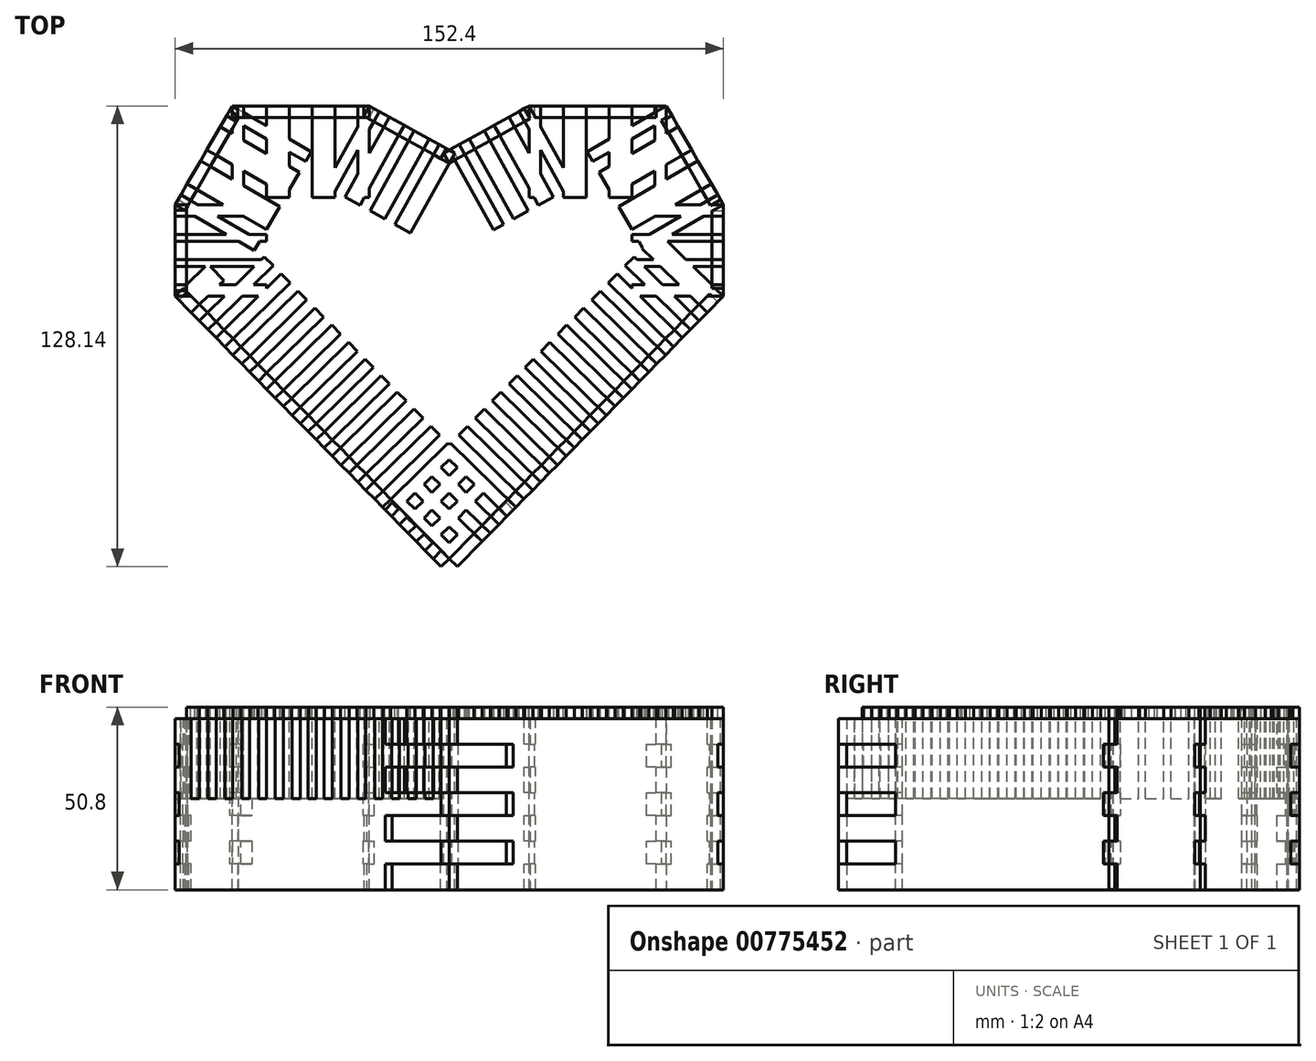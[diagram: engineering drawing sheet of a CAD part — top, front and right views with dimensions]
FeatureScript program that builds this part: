
annotation { "Feature Type Name" : "Feature", "Feature Type Description" : "" }
export const myFeature = defineFeature(function(context is Context, id is Id, definition is map)
    precondition{}
    {
        {
            var Q0;
            Q0=qCreatedBy(makeId("Top.planeOp"),FACE);
            var sketch = newSketch(context, id + "F0", { "sketchPlane" : qUnion([Q0])});
            skLineSegment(sketch, "E0", {"start": v(-76.2, 0) * mm, "end": v(0, -77.54) * mm});
            skLineSegment(sketch, "E1", {"start": v(0, -77.54) * mm, "end": v(76.2, 0) * mm});
            skLineSegment(sketch, "E2", {"start": v(76.2, 0) * mm, "end": v(76.2, 25.4) * mm});
            skLineSegment(sketch, "E3", {"start": v(76.2, 25.4) * mm, "end": v(60.32, 52.9) * mm});
            skLineSegment(sketch, "E4", {"start": v(60.32, 52.9) * mm, "end": v(22.23, 52.9) * mm});
            skLineSegment(sketch, "E5", {"start": v(22.23, 52.9) * mm, "end": v(0, 40.6) * mm});
            skLineSegment(sketch, "E6", {"start": v(0, 40.6) * mm, "end": v(-22.23, 52.9) * mm});
            skLineSegment(sketch, "E7", {"start": v(-22.23, 52.9) * mm, "end": v(-60.33, 52.9) * mm});
            skLineSegment(sketch, "E8", {"start": v(-60.32, 52.9) * mm, "end": v(-76.2, 25.4) * mm});
            skLineSegment(sketch, "E9", {"start": v(-76.2, 25.4) * mm, "end": v(-76.2, 0) * mm});
            skSolve(sketch);
        }
        {
            var Q0;
            Q0=makeQuery(id+"F0.imprint","IMPRINT",FACE,{"disambiguationData":[TD([[makeQuery(id+"F0.imprint","IMPRINT",EDGE,{"derivedFrom":sQuery(id+"F0.wireOp",EDGE,"E0")}),1.0]])]});
            extrude(context, id + "F1", {"entities" : qUnion([Q0]), "depth" : 3.17 * mm, "offsetDistance" : 25.4 * mm});
        }
        {
            var Q0;
            Q0=makeQuery(id+"F1.opExtrude","CAP_FACE",FACE,{"disambiguationData":[OSD([sQuery(id+"F0.wireOp",EDGE,"E0"),sQuery(id+"F0.wireOp",EDGE,"E1"),sQuery(id+"F0.wireOp",EDGE,"E2"),sQuery(id+"F0.wireOp",EDGE,"E3"),sQuery(id+"F0.wireOp",EDGE,"E4"),sQuery(id+"F0.wireOp",EDGE,"E5"),sQuery(id+"F0.wireOp",EDGE,"E6"),sQuery(id+"F0.wireOp",EDGE,"E7"),sQuery(id+"F0.wireOp",EDGE,"E8"),sQuery(id+"F0.wireOp",EDGE,"E9")])],"isStart":false});
            var sketch = newSketch(context, id + "F2", { "sketchPlane" : qUnion([Q0])});
            skLineSegment(sketch, "E10", {"start": v(-22.23, 52.9) * mm, "end": v(-23.76, 50.12) * mm});
            skLineSegment(sketch, "E11", {"start": v(-23.76, 50.12) * mm, "end": v(-1.54, 37.82) * mm});
            skLineSegment(sketch, "E12", {"start": v(-1.54, 37.82) * mm, "end": v(0, 40.6) * mm});
            skLineSegment(sketch, "E13", {"start": v(-76.2, 0) * mm, "end": v(-73.94, 2.23) * mm});
            skLineSegment(sketch, "E14", {"start": v(-73.94, 2.23) * mm, "end": v(2.26, -75.32) * mm});
            skLineSegment(sketch, "E15", {"start": v(2.26, -75.32) * mm, "end": v(0, -77.54) * mm});
            skLineSegment(sketch, "E16", {"start": v(76.2, 25.4) * mm, "end": v(73.03, 25.4) * mm});
            skLineSegment(sketch, "E17", {"start": v(73.03, 25.4) * mm, "end": v(73.03, 0) * mm});
            skLineSegment(sketch, "E18", {"start": v(73.03, 0) * mm, "end": v(76.2, 0) * mm});
            skLineSegment(sketch, "E19", {"start": v(-76.2, 25.4) * mm, "end": v(-73.03, 25.4) * mm});
            skLineSegment(sketch, "E20", {"start": v(-73.03, 25.4) * mm, "end": v(-73.03, 0) * mm});
            skLineSegment(sketch, "E21", {"start": v(-73.03, 0) * mm, "end": v(-76.2, 0) * mm});
            skLineSegment(sketch, "E22", {"start": v(-76.2, 25.4) * mm, "end": v(-73.45, 23.81) * mm});
            skPoint(sketch, "E22.endSnap0", {"position": v(-73.03, 12.7) * mm});
            skLineSegment(sketch, "E23", {"start": v(-73.45, 23.81) * mm, "end": v(-57.58, 51.3) * mm});
            skLineSegment(sketch, "E24", {"start": v(-57.58, 51.3) * mm, "end": v(-60.33, 52.9) * mm});
            skLineSegment(sketch, "E25", {"start": v(-60.33, 52.9) * mm, "end": v(-60.33, 49.72) * mm});
            skLineSegment(sketch, "E26", {"start": v(-60.33, 49.72) * mm, "end": v(-22.23, 49.72) * mm});
            skLineSegment(sketch, "E27", {"start": v(-22.23, 49.72) * mm, "end": v(-22.23, 52.9) * mm});
            skLineSegment(sketch, "E28", {"start": v(0, 40.6) * mm, "end": v(1.54, 37.82) * mm});
            skLineSegment(sketch, "E29", {"start": v(1.54, 37.82) * mm, "end": v(23.76, 50.12) * mm});
            skLineSegment(sketch, "E30", {"start": v(23.76, 50.12) * mm, "end": v(22.23, 52.9) * mm});
            skLineSegment(sketch, "E31", {"start": v(22.23, 52.9) * mm, "end": v(22.23, 49.72) * mm});
            skLineSegment(sketch, "E32", {"start": v(60.32, 49.72) * mm, "end": v(22.23, 49.72) * mm});
            skLineSegment(sketch, "E33", {"start": v(60.32, 49.72) * mm, "end": v(60.32, 52.9) * mm});
            skLineSegment(sketch, "E34", {"start": v(0, -77.54) * mm, "end": v(-2.26, -75.32) * mm});
            skLineSegment(sketch, "E35", {"start": v(-2.26, -75.32) * mm, "end": v(73.94, 2.23) * mm});
            skLineSegment(sketch, "E36", {"start": v(73.94, 2.23) * mm, "end": v(76.2, 0) * mm});
            skLineSegment(sketch, "E37", {"start": v(60.32, 52.9) * mm, "end": v(57.58, 51.3) * mm});
            skLineSegment(sketch, "E38", {"start": v(57.58, 51.3) * mm, "end": v(73.45, 23.81) * mm});
            skLineSegment(sketch, "E39", {"start": v(73.45, 23.81) * mm, "end": v(76.2, 25.4) * mm});
            skLineSegment(sketch, "E40", {"start": v(0, 40.6) * mm, "end": v(1.54, 39.75) * mm});
            skLineSegment(sketch, "E41", {"start": v(1.54, 39.75) * mm, "end": v(0, 36.97) * mm});
            skLineSegment(sketch, "E42", {"start": v(0, 36.97) * mm, "end": v(-1.54, 37.82) * mm});
            skLineSegment(sketch, "E43", {"start": v(1.54, 37.82) * mm, "end": v(0, 36.97) * mm});
            skLineSegment(sketch, "E44", {"start": v(0, 36.97) * mm, "end": v(-1.54, 39.75) * mm});
            skLineSegment(sketch, "E45", {"start": v(-1.54, 39.75) * mm, "end": v(0, 40.6) * mm});
            skSolve(sketch);
        }
        {
            var Q0;
            {var subQ0=sQuery(id+"F2.wireOp",EDGE,"E24");Q0=makeQuery(id+"F2.imprint","IMPRINT",FACE,{"disambiguationData":[TD([[makeQuery(id+"F2.imprint","IMPRINT",EDGE,{"derivedFrom":subQ0}),1.0]])]});}
            var Q1;
            {var subQ5=sQuery(id+"F2.wireOp",EDGE,"E10");Q1=makeQuery(id+"F2.imprint","IMPRINT",FACE,{"disambiguationData":[TD([[makeQuery(id+"F2.imprint","IMPRINT",EDGE,{"derivedFrom":subQ5}),-1.0]])]});}
            var Q2;
            {var subQ0=sQuery(id+"F2.wireOp",EDGE,"E10");Q2=makeQuery(id+"F2.imprint","IMPRINT",FACE,{"disambiguationData":[TD([[makeQuery(id+"F2.imprint","IMPRINT",EDGE,{"derivedFrom":subQ0}),1.0]])]});}
            extrude(context, id + "F3", {"entities" : qUnion([Q0, Q1, Q2]), "oppositeDirection" : true, "depth" : 50.8 * mm, "offsetDistance" : 25.4 * mm});
        }
        {
            var Q0;
            {var subQ5=sQuery(id+"F2.wireOp",EDGE,"E19");Q0=makeQuery(id+"F2.imprint","IMPRINT",FACE,{"disambiguationData":[TD([[makeQuery(id+"F2.imprint","IMPRINT",EDGE,{"derivedFrom":subQ5}),1.0]])]});}
            var Q1;
            {var subQ0=sQuery(id+"F2.wireOp",EDGE,"E19");Q1=makeQuery(id+"F2.imprint","IMPRINT",FACE,{"disambiguationData":[TD([[makeQuery(id+"F2.imprint","IMPRINT",EDGE,{"derivedFrom":subQ0}),-1.0]])]});}
            var Q2;
            Q2=makeQuery(id+"F3.opExtrude","CAP_VERTEX",VERTEX,{"disambiguationData":[OSD([sQuery(id+"F2.wireOp",EDGE,"E25"),sQuery(id+"F2.wireOp",EDGE,"E26")])],"isStart":false});
            extrude(context, id + "F4", {"entities" : qUnion([Q0, Q1]), "endBound" : BoundingType.UP_TO_VERTEX, "oppositeDirection" : true, "depth" : 25.4 * mm, "endBoundEntityVertex" : qUnion([Q2]), "offsetDistance" : 25.4 * mm});
        }
        {
            var Q0;
            {var subQ6=sQuery(id+"F2.wireOp",EDGE,"E13");Q0=makeQuery(id+"F2.imprint","IMPRINT",FACE,{"disambiguationData":[TD([[makeQuery(id+"F2.imprint","IMPRINT",EDGE,{"derivedFrom":subQ6}),1.0]])]});}
            var Q1;
            {var subQ0=sQuery(id+"F2.wireOp",EDGE,"E13");Q1=makeQuery(id+"F2.imprint","IMPRINT",FACE,{"disambiguationData":[TD([[makeQuery(id+"F2.imprint","IMPRINT",EDGE,{"derivedFrom":subQ0}),-1.0]])]});}
            var Q2;
            {var subQ0=sQuery(id+"F2.wireOp",EDGE,"E19");Q2=makeQuery(id+"F2.imprint","IMPRINT",FACE,{"disambiguationData":[TD([[makeQuery(id+"F2.imprint","IMPRINT",EDGE,{"derivedFrom":subQ0}),-1.0]])]});}
            var Q3;
            Q3=makeQuery(id+"F4.opExtrude","CAP_VERTEX",VERTEX,{"disambiguationData":[OSD([sQuery(id+"F0.wireOp",EDGE,"E8"),sQuery(id+"F2.wireOp",EDGE,"E22")])],"isStart":false});
            extrude(context, id + "F5", {"entities" : qUnion([Q0, Q1, Q2]), "endBound" : BoundingType.UP_TO_VERTEX, "oppositeDirection" : true, "depth" : 25.4 * mm, "endBoundEntityVertex" : qUnion([Q3]), "offsetDistance" : 25.4 * mm});
        }
        {
            var Q0;
            {var subQ0=sQuery(id+"F2.wireOp",EDGE,"E21");Q0=makeQuery(id+"F2.imprint","IMPRINT",FACE,{"disambiguationData":[TD([[makeQuery(id+"F2.imprint","IMPRINT",EDGE,{"derivedFrom":subQ0}),1.0]])]});}
            var Q1;
            {var subQ0=sQuery(id+"F2.wireOp",EDGE,"E13");Q1=makeQuery(id+"F2.imprint","IMPRINT",FACE,{"disambiguationData":[TD([[makeQuery(id+"F2.imprint","IMPRINT",EDGE,{"derivedFrom":subQ0}),-1.0]])]});}
            var Q2;
            {var subQ0=sQuery(id+"F2.wireOp",EDGE,"E35");var subQ1=sQuery(id+"F2.wireOp",EDGE,"E14");var subQ2=makeQuery(id+"F2.imprint","INTERSECT",VERTEX,{"derivedFrom":[subQ1,subQ0]});Q2=makeQuery(id+"F2.imprint","IMPRINT",FACE,{"disambiguationData":[TD([[makeQuery(id+"F2.imprint","IMPRINT",EDGE,{"disambiguationData":[TD([[subQ2,-1.0]])],"derivedFrom":subQ1}),-1.0]])]});}
            var Q3;
            Q3=makeQuery(id+"F5.opExtrude","CAP_VERTEX",VERTEX,{"disambiguationData":[OSD([sQuery(id+"F0.wireOp",EDGE,"E9"),sQuery(id+"F2.wireOp",EDGE,"E21")])],"isStart":false});
            extrude(context, id + "F6", {"entities" : qUnion([Q0, Q1, Q2]), "endBound" : BoundingType.UP_TO_VERTEX, "oppositeDirection" : true, "depth" : 25.4 * mm, "endBoundEntityVertex" : qUnion([Q3]), "offsetDistance" : 25.4 * mm});
        }
        {
            var Q0;
            {var subQ0=sQuery(id+"F2.wireOp",EDGE,"E18");Q0=makeQuery(id+"F2.imprint","IMPRINT",FACE,{"disambiguationData":[TD([[makeQuery(id+"F2.imprint","IMPRINT",EDGE,{"derivedFrom":subQ0}),-1.0]])]});}
            var Q1;
            {var subQ0=sQuery(id+"F2.wireOp",EDGE,"E35");var subQ1=sQuery(id+"F2.wireOp",EDGE,"E14");var subQ2=makeQuery(id+"F2.imprint","INTERSECT",VERTEX,{"derivedFrom":[subQ1,subQ0]});Q1=makeQuery(id+"F2.imprint","IMPRINT",FACE,{"disambiguationData":[TD([[makeQuery(id+"F2.imprint","IMPRINT",EDGE,{"disambiguationData":[TD([[subQ2,-1.0]])],"derivedFrom":subQ1}),-1.0]])]});}
            var Q2;
            {var subQ0=sQuery(id+"F2.wireOp",EDGE,"E18");Q2=makeQuery(id+"F2.imprint","IMPRINT",FACE,{"disambiguationData":[TD([[makeQuery(id+"F2.imprint","IMPRINT",EDGE,{"derivedFrom":subQ0}),1.0]])]});}
            var Q3;
            Q3=makeQuery(id+"F6.opExtrude","CAP_VERTEX",VERTEX,{"disambiguationData":[OSD([sQuery(id+"F0.wireOp",EDGE,"E0"),sQuery(id+"F0.wireOp",EDGE,"E1")])],"isStart":false});
            extrude(context, id + "F7", {"entities" : qUnion([Q0, Q1, Q2]), "endBound" : BoundingType.UP_TO_VERTEX, "oppositeDirection" : true, "depth" : 25.4 * mm, "endBoundEntityVertex" : qUnion([Q3]), "offsetDistance" : 25.4 * mm});
        }
        {
            var Q0;
            {var subQ0=sQuery(id+"F2.wireOp",EDGE,"E36");Q0=makeQuery(id+"F2.imprint","IMPRINT",FACE,{"disambiguationData":[TD([[makeQuery(id+"F2.imprint","IMPRINT",EDGE,{"derivedFrom":subQ0}),1.0]])]});}
            var Q1;
            {var subQ0=sQuery(id+"F2.wireOp",EDGE,"E16");Q1=makeQuery(id+"F2.imprint","IMPRINT",FACE,{"disambiguationData":[TD([[makeQuery(id+"F2.imprint","IMPRINT",EDGE,{"derivedFrom":subQ0}),1.0]])]});}
            var Q2;
            {var subQ0=sQuery(id+"F2.wireOp",EDGE,"E18");Q2=makeQuery(id+"F2.imprint","IMPRINT",FACE,{"disambiguationData":[TD([[makeQuery(id+"F2.imprint","IMPRINT",EDGE,{"derivedFrom":subQ0}),1.0]])]});}
            var Q3;
            Q3=makeQuery(id+"F7.opExtrude","CAP_VERTEX",VERTEX,{"disambiguationData":[OSD([sQuery(id+"F2.wireOp",EDGE,"E35"),sQuery(id+"F2.wireOp",EDGE,"E36")])],"isStart":false});
            extrude(context, id + "F8", {"entities" : qUnion([Q0, Q1, Q2]), "endBound" : BoundingType.UP_TO_VERTEX, "oppositeDirection" : true, "depth" : 25.4 * mm, "endBoundEntityVertex" : qUnion([Q3]), "offsetDistance" : 25.4 * mm});
        }
        {
            var Q0;
            {var subQ2=sQuery(id+"F2.wireOp",EDGE,"E16");Q0=makeQuery(id+"F2.imprint","IMPRINT",FACE,{"disambiguationData":[TD([[makeQuery(id+"F2.imprint","IMPRINT",EDGE,{"derivedFrom":subQ2}),-1.0]])]});}
            var Q1;
            {var subQ0=sQuery(id+"F2.wireOp",EDGE,"E16");Q1=makeQuery(id+"F2.imprint","IMPRINT",FACE,{"disambiguationData":[TD([[makeQuery(id+"F2.imprint","IMPRINT",EDGE,{"derivedFrom":subQ0}),1.0]])]});}
            var Q2;
            {var subQ0=sQuery(id+"F2.wireOp",EDGE,"E33");Q2=makeQuery(id+"F2.imprint","IMPRINT",FACE,{"disambiguationData":[TD([[makeQuery(id+"F2.imprint","IMPRINT",EDGE,{"derivedFrom":subQ0}),1.0]])]});}
            var Q3;
            Q3=makeQuery(id+"F8.opExtrude","CAP_VERTEX",VERTEX,{"disambiguationData":[OSD([sQuery(id+"F2.wireOp",EDGE,"E16"),sQuery(id+"F2.wireOp",EDGE,"E17")])],"isStart":false});
            extrude(context, id + "F9", {"entities" : qUnion([Q0, Q1, Q2]), "endBound" : BoundingType.UP_TO_VERTEX, "oppositeDirection" : true, "depth" : 25.4 * mm, "endBoundEntityVertex" : qUnion([Q3]), "offsetDistance" : 25.4 * mm});
        }
        {
            var Q0;
            {var subQ6=sQuery(id+"F2.wireOp",EDGE,"E30");Q0=makeQuery(id+"F2.imprint","IMPRINT",FACE,{"disambiguationData":[TD([[makeQuery(id+"F2.imprint","IMPRINT",EDGE,{"derivedFrom":subQ6}),-1.0]])]});}
            var Q1;
            {var subQ0=sQuery(id+"F2.wireOp",EDGE,"E30");Q1=makeQuery(id+"F2.imprint","IMPRINT",FACE,{"disambiguationData":[TD([[makeQuery(id+"F2.imprint","IMPRINT",EDGE,{"derivedFrom":subQ0}),1.0]])]});}
            var Q2;
            {var subQ0=sQuery(id+"F2.wireOp",EDGE,"E33");Q2=makeQuery(id+"F2.imprint","IMPRINT",FACE,{"disambiguationData":[TD([[makeQuery(id+"F2.imprint","IMPRINT",EDGE,{"derivedFrom":subQ0}),1.0]])]});}
            var Q3;
            Q3=makeQuery(id+"F9.opExtrude","CAP_VERTEX",VERTEX,{"disambiguationData":[OSD([sQuery(id+"F0.wireOp",EDGE,"E3"),sQuery(id+"F2.wireOp",EDGE,"E37")])],"isStart":false});
            extrude(context, id + "F10", {"entities" : qUnion([Q0, Q1, Q2]), "endBound" : BoundingType.UP_TO_VERTEX, "oppositeDirection" : true, "depth" : 25.4 * mm, "endBoundEntityVertex" : qUnion([Q3]), "offsetDistance" : 25.4 * mm});
        }
        {
            var Q0;
            {var subQ4=sQuery(id+"F2.wireOp",EDGE,"E28");Q0=makeQuery(id+"F2.imprint","IMPRINT",FACE,{"disambiguationData":[TD([[makeQuery(id+"F2.imprint","IMPRINT",EDGE,{"derivedFrom":subQ4}),1.0]])]});}
            var Q1;
            {var subQ0=sQuery(id+"F2.wireOp",EDGE,"E30");Q1=makeQuery(id+"F2.imprint","IMPRINT",FACE,{"disambiguationData":[TD([[makeQuery(id+"F2.imprint","IMPRINT",EDGE,{"derivedFrom":subQ0}),1.0]])]});}
            var Q2;
            {var subQ0=sQuery(id+"F2.wireOp",EDGE,"E28");var subQ5=sQuery(id+"F2.wireOp",EDGE,"E41");var subQ7=makeQuery(id+"F2.imprint","INTERSECT",VERTEX,{"derivedFrom":[subQ0,subQ5]});Q2=makeQuery(id+"F2.imprint","IMPRINT",FACE,{"disambiguationData":[TD([[makeQuery(id+"F2.imprint","IMPRINT",EDGE,{"disambiguationData":[TD([[subQ7,-1.0]])],"derivedFrom":subQ5}),-1.0]])]});}
            var Q3;
            {var subQ0=sQuery(id+"F2.wireOp",EDGE,"E45");Q3=makeQuery(id+"F2.imprint","IMPRINT",FACE,{"disambiguationData":[TD([[makeQuery(id+"F2.imprint","IMPRINT",EDGE,{"derivedFrom":subQ0}),-1.0]])]});}
            var Q4;
            {var subQ0=sQuery(id+"F2.wireOp",EDGE,"E43");Q4=makeQuery(id+"F2.imprint","IMPRINT",FACE,{"disambiguationData":[TD([[makeQuery(id+"F2.imprint","IMPRINT",EDGE,{"derivedFrom":subQ0}),-1.0]])]});}
            var Q5;
            {var subQ1=sQuery(id+"F2.wireOp",EDGE,"E31");Q5=makeQuery(id+"F2.imprint","IMPRINT",FACE,{"disambiguationData":[TD([[makeQuery(id+"F2.imprint","IMPRINT",EDGE,{"derivedFrom":subQ1}),-1.0]])]});}
            var Q6;
            Q6=makeQuery(id+"F10.opExtrude","CAP_VERTEX",VERTEX,{"disambiguationData":[OSD([sQuery(id+"F2.wireOp",EDGE,"E31"),sQuery(id+"F2.wireOp",EDGE,"E32")])],"isStart":false});
            extrude(context, id + "F11", {"entities" : qUnion([Q0, Q1, Q2, Q3, Q4, Q5]), "endBound" : BoundingType.UP_TO_VERTEX, "oppositeDirection" : true, "depth" : 25.4 * mm, "endBoundEntityVertex" : qUnion([Q6]), "offsetDistance" : 25.4 * mm});
        }
        {
            var Q0;
            {var subQ4=sQuery(id+"F2.wireOp",EDGE,"E12");Q0=makeQuery(id+"F2.imprint","IMPRINT",FACE,{"disambiguationData":[TD([[makeQuery(id+"F2.imprint","IMPRINT",EDGE,{"derivedFrom":subQ4}),1.0]])]});}
            var Q1;
            {var subQ0=sQuery(id+"F2.wireOp",EDGE,"E10");Q1=makeQuery(id+"F2.imprint","IMPRINT",FACE,{"disambiguationData":[TD([[makeQuery(id+"F2.imprint","IMPRINT",EDGE,{"derivedFrom":subQ0}),1.0]])]});}
            var Q2;
            {var subQ0=sQuery(id+"F2.wireOp",EDGE,"E27");Q2=makeQuery(id+"F2.imprint","IMPRINT",FACE,{"disambiguationData":[TD([[makeQuery(id+"F2.imprint","IMPRINT",EDGE,{"derivedFrom":subQ0}),-1.0]])]});}
            var Q3;
            {var subQ0=sQuery(id+"F2.wireOp",EDGE,"E28");var subQ5=sQuery(id+"F2.wireOp",EDGE,"E41");var subQ7=makeQuery(id+"F2.imprint","INTERSECT",VERTEX,{"derivedFrom":[subQ0,subQ5]});Q3=makeQuery(id+"F2.imprint","IMPRINT",FACE,{"disambiguationData":[TD([[makeQuery(id+"F2.imprint","IMPRINT",EDGE,{"disambiguationData":[TD([[subQ7,-1.0]])],"derivedFrom":subQ5}),-1.0]])]});}
            var Q4;
            {var subQ0=sQuery(id+"F2.wireOp",EDGE,"E42");Q4=makeQuery(id+"F2.imprint","IMPRINT",FACE,{"disambiguationData":[TD([[makeQuery(id+"F2.imprint","IMPRINT",EDGE,{"derivedFrom":subQ0}),-1.0]])]});}
            var Q5;
            {var subQ0=sQuery(id+"F2.wireOp",EDGE,"E40");Q5=makeQuery(id+"F2.imprint","IMPRINT",FACE,{"disambiguationData":[TD([[makeQuery(id+"F2.imprint","IMPRINT",EDGE,{"derivedFrom":subQ0}),-1.0]])]});}
            var Q6;
            Q6=makeQuery(id+"F11.opExtrude","CAP_VERTEX",VERTEX,{"disambiguationData":[OSD([sQuery(id+"F0.wireOp",EDGE,"E5"),sQuery(id+"F2.wireOp",EDGE,"E44"),sQuery(id+"F2.wireOp",EDGE,"E45")])],"isStart":false});
            extrude(context, id + "F12", {"entities" : qUnion([Q0, Q1, Q2, Q3, Q4, Q5]), "endBound" : BoundingType.UP_TO_VERTEX, "oppositeDirection" : true, "depth" : 25.4 * mm, "endBoundEntityVertex" : qUnion([Q6]), "offsetDistance" : 25.4 * mm});
        }
        {
            var Q0;
            Q0=makeQuery(id+"F1.opExtrude","CAP_FACE",FACE,{"disambiguationData":[OSD([sQuery(id+"F0.wireOp",EDGE,"E0"),sQuery(id+"F0.wireOp",EDGE,"E1"),sQuery(id+"F0.wireOp",EDGE,"E2"),sQuery(id+"F0.wireOp",EDGE,"E3"),sQuery(id+"F0.wireOp",EDGE,"E4"),sQuery(id+"F0.wireOp",EDGE,"E5"),sQuery(id+"F0.wireOp",EDGE,"E6"),sQuery(id+"F0.wireOp",EDGE,"E7"),sQuery(id+"F0.wireOp",EDGE,"E8"),sQuery(id+"F0.wireOp",EDGE,"E9")])],"isStart":false});
            var sketch = newSketch(context, id + "F13", { "sketchPlane" : qUnion([Q0])});
            skCircle(sketch, "E46", {"center": v(-22.23, 52.9) * mm, "radius": 3.18 * mm});
            skCircle(sketch, "E47", {"center": v(0, 40.6) * mm, "radius": 3.18 * mm});
            skLineSegment(sketch, "E48", {"start": v(-19.45, 51.36) * mm, "end": v(-20.98, 48.58) * mm});
            skLineSegment(sketch, "E49", {"start": v(-20.98, 48.58) * mm, "end": v(-18.2, 47.04) * mm});
            skLineSegment(sketch, "E50", {"start": v(-18.2, 47.04) * mm, "end": v(-16.67, 49.82) * mm});
            skLineSegment(sketch, "E51", {"start": v(-12.5, 47.52) * mm, "end": v(-14.04, 44.74) * mm});
            skLineSegment(sketch, "E52", {"start": v(-14.04, 44.74) * mm, "end": v(-11.26, 43.2) * mm});
            skLineSegment(sketch, "E53", {"start": v(-11.26, 43.2) * mm, "end": v(-9.72, 45.98) * mm});
            skLineSegment(sketch, "E54", {"start": v(-5.56, 43.67) * mm, "end": v(-7.1, 40.9) * mm});
            skLineSegment(sketch, "E55", {"start": v(-7.1, 40.9) * mm, "end": v(-4.32, 39.36) * mm});
            skLineSegment(sketch, "E56", {"start": v(-4.32, 39.36) * mm, "end": v(-2.78, 42.14) * mm});
            skLineSegment(sketch, "E57", {"start": v(-17.44, 48.43) * mm, "end": v(-13.27, 46.13) * mm, "construction": true});
            skLineSegment(sketch, "E58", {"start": v(-10.5, 44.6) * mm, "end": v(-6.32, 42.28) * mm, "construction": true});
            skSolve(sketch);
        }
        {
            var Q0;
            {var subQ0=sQuery(id+"F13.wireOp",EDGE,"E48");Q0=makeQuery(id+"F13.imprint","IMPRINT",FACE,{"disambiguationData":[TD([[makeQuery(id+"F13.imprint","IMPRINT",EDGE,{"derivedFrom":subQ0}),1.0]])]});}
            var Q1;
            {var subQ0=sQuery(id+"F13.wireOp",EDGE,"E51");Q1=makeQuery(id+"F13.imprint","IMPRINT",FACE,{"disambiguationData":[TD([[makeQuery(id+"F13.imprint","IMPRINT",EDGE,{"derivedFrom":subQ0}),1.0]])]});}
            var Q2;
            {var subQ0=sQuery(id+"F13.wireOp",EDGE,"E54");Q2=makeQuery(id+"F13.imprint","IMPRINT",FACE,{"disambiguationData":[TD([[makeQuery(id+"F13.imprint","IMPRINT",EDGE,{"derivedFrom":subQ0}),1.0]])]});}
            extrude(context, id + "F14", {"entities" : qUnion([Q0, Q1, Q2]), "operationType" : NewBodyOperationType.REMOVE, "oppositeDirection" : true, "depth" : 25.4 * mm, "offsetDistance" : 25.4 * mm});
        }
        {
            var Q0;
            Q0=makeQuery(id+"F1.opExtrude","CAP_FACE",FACE,{"disambiguationData":[OSD([sQuery(id+"F0.wireOp",EDGE,"E0"),sQuery(id+"F0.wireOp",EDGE,"E1"),sQuery(id+"F0.wireOp",EDGE,"E2"),sQuery(id+"F0.wireOp",EDGE,"E3"),sQuery(id+"F0.wireOp",EDGE,"E4"),sQuery(id+"F0.wireOp",EDGE,"E5"),sQuery(id+"F0.wireOp",EDGE,"E6"),sQuery(id+"F0.wireOp",EDGE,"E7"),sQuery(id+"F0.wireOp",EDGE,"E8"),sQuery(id+"F0.wireOp",EDGE,"E9")])],"isStart":false});
            var sketch = newSketch(context, id + "F15", { "sketchPlane" : qUnion([Q0])});
            skCircle(sketch, "E59", {"center": v(-60.33, 52.9) * mm, "radius": 3.18 * mm});
            skCircle(sketch, "E60", {"center": v(-22.23, 52.9) * mm, "radius": 3.18 * mm});
            skLineSegment(sketch, "E61", {"start": v(-57.15, 52.9) * mm, "end": v(-57.15, 49.72) * mm});
            skLineSegment(sketch, "E62", {"start": v(-57.15, 49.72) * mm, "end": v(-50.8, 49.72) * mm});
            skLineSegment(sketch, "E63", {"start": v(-50.8, 49.72) * mm, "end": v(-50.8, 52.9) * mm});
            skLineSegment(sketch, "E64", {"start": v(-44.45, 52.9) * mm, "end": v(-44.45, 49.72) * mm});
            skLineSegment(sketch, "E65", {"start": v(-44.45, 49.72) * mm, "end": v(-38.1, 49.72) * mm});
            skLineSegment(sketch, "E66", {"start": v(-38.1, 49.72) * mm, "end": v(-38.1, 52.9) * mm});
            skLineSegment(sketch, "E67", {"start": v(-31.75, 52.9) * mm, "end": v(-31.75, 49.72) * mm});
            skLineSegment(sketch, "E68", {"start": v(-31.75, 49.72) * mm, "end": v(-25.4, 49.72) * mm});
            skLineSegment(sketch, "E69", {"start": v(-25.4, 49.72) * mm, "end": v(-25.4, 52.9) * mm});
            skLineSegment(sketch, "E70", {"start": v(-50.8, 51.3) * mm, "end": v(-44.45, 51.3) * mm, "construction": true});
            skPoint(sketch, "E70.startSnap0", {"position": v(-50.8, 51.3) * mm});
            skLineSegment(sketch, "E71", {"start": v(-38.1, 51.3) * mm, "end": v(-31.75, 51.3) * mm, "construction": true});
            skSolve(sketch);
        }
        {
            var Q0;
            {var subQ0=sQuery(id+"F15.wireOp",EDGE,"E61");Q0=makeQuery(id+"F15.imprint","IMPRINT",FACE,{"disambiguationData":[TD([[makeQuery(id+"F15.imprint","IMPRINT",EDGE,{"derivedFrom":subQ0}),1.0]])]});}
            var Q1;
            {var subQ0=sQuery(id+"F15.wireOp",EDGE,"E64");Q1=makeQuery(id+"F15.imprint","IMPRINT",FACE,{"disambiguationData":[TD([[makeQuery(id+"F15.imprint","IMPRINT",EDGE,{"derivedFrom":subQ0}),1.0]])]});}
            var Q2;
            {var subQ0=sQuery(id+"F15.wireOp",EDGE,"E67");Q2=makeQuery(id+"F15.imprint","IMPRINT",FACE,{"disambiguationData":[TD([[makeQuery(id+"F15.imprint","IMPRINT",EDGE,{"derivedFrom":subQ0}),1.0]])]});}
            extrude(context, id + "F16", {"entities" : qUnion([Q0, Q1, Q2]), "operationType" : NewBodyOperationType.REMOVE, "oppositeDirection" : true, "depth" : 25.4 * mm, "offsetDistance" : 25.4 * mm});
        }
        {
            var Q0;
            Q0=makeQuery(id+"F1.opExtrude","CAP_FACE",FACE,{"disambiguationData":[OSD([sQuery(id+"F0.wireOp",EDGE,"E0"),sQuery(id+"F0.wireOp",EDGE,"E1"),sQuery(id+"F0.wireOp",EDGE,"E2"),sQuery(id+"F0.wireOp",EDGE,"E3"),sQuery(id+"F0.wireOp",EDGE,"E4"),sQuery(id+"F0.wireOp",EDGE,"E5"),sQuery(id+"F0.wireOp",EDGE,"E6"),sQuery(id+"F0.wireOp",EDGE,"E7"),sQuery(id+"F0.wireOp",EDGE,"E8"),sQuery(id+"F0.wireOp",EDGE,"E9")])],"isStart":false});
            var sketch = newSketch(context, id + "F17", { "sketchPlane" : qUnion([Q0])});
            skCircle(sketch, "E72", {"center": v(-76.2, 25.4) * mm, "radius": 3.18 * mm});
            skCircle(sketch, "E73", {"center": v(-60.33, 52.9) * mm, "radius": 3.18 * mm});
            skLineSegment(sketch, "E74", {"start": v(-74.61, 28.15) * mm, "end": v(-71.86, 26.56) * mm});
            skLineSegment(sketch, "E75", {"start": v(-71.86, 26.56) * mm, "end": v(-70.1, 29.6) * mm});
            skLineSegment(sketch, "E76", {"start": v(-70.1, 29.6) * mm, "end": v(-72.86, 31.19) * mm});
            skLineSegment(sketch, "E77", {"start": v(-69.14, 37.63) * mm, "end": v(-66.4, 36.04) * mm});
            skLineSegment(sketch, "E78", {"start": v(-66.4, 36.04) * mm, "end": v(-64.64, 39.08) * mm});
            skLineSegment(sketch, "E79", {"start": v(-64.64, 39.08) * mm, "end": v(-67.39, 40.67) * mm});
            skLineSegment(sketch, "E80", {"start": v(-63.67, 47.1) * mm, "end": v(-60.92, 45.52) * mm});
            skLineSegment(sketch, "E81", {"start": v(-60.92, 45.52) * mm, "end": v(-59.16, 48.56) * mm});
            skLineSegment(sketch, "E82", {"start": v(-59.16, 48.56) * mm, "end": v(-61.91, 50.15) * mm});
            skLineSegment(sketch, "E83", {"start": v(-71.48, 30.4) * mm, "end": v(-67.76, 36.83) * mm, "construction": true});
            skLineSegment(sketch, "E84", {"start": v(-66.01, 39.87) * mm, "end": v(-62.3, 46.31) * mm, "construction": true});
            skSolve(sketch);
        }
        {
            var Q0;
            {var subQ0=sQuery(id+"F17.wireOp",EDGE,"E74");Q0=makeQuery(id+"F17.imprint","IMPRINT",FACE,{"disambiguationData":[TD([[makeQuery(id+"F17.imprint","IMPRINT",EDGE,{"derivedFrom":subQ0}),1.0]])]});}
            var Q1;
            {var subQ0=sQuery(id+"F17.wireOp",EDGE,"E77");Q1=makeQuery(id+"F17.imprint","IMPRINT",FACE,{"disambiguationData":[TD([[makeQuery(id+"F17.imprint","IMPRINT",EDGE,{"derivedFrom":subQ0}),1.0]])]});}
            var Q2;
            {var subQ0=sQuery(id+"F17.wireOp",EDGE,"E80");Q2=makeQuery(id+"F17.imprint","IMPRINT",FACE,{"disambiguationData":[TD([[makeQuery(id+"F17.imprint","IMPRINT",EDGE,{"derivedFrom":subQ0}),1.0]])]});}
            extrude(context, id + "F18", {"entities" : qUnion([Q0, Q1, Q2]), "operationType" : NewBodyOperationType.REMOVE, "oppositeDirection" : true, "depth" : 25.4 * mm, "offsetDistance" : 25.4 * mm});
        }
        {
            var Q0;
            Q0=makeQuery(id+"F1.opExtrude","CAP_FACE",FACE,{"disambiguationData":[OSD([sQuery(id+"F0.wireOp",EDGE,"E0"),sQuery(id+"F0.wireOp",EDGE,"E1"),sQuery(id+"F0.wireOp",EDGE,"E2"),sQuery(id+"F0.wireOp",EDGE,"E3"),sQuery(id+"F0.wireOp",EDGE,"E4"),sQuery(id+"F0.wireOp",EDGE,"E5"),sQuery(id+"F0.wireOp",EDGE,"E6"),sQuery(id+"F0.wireOp",EDGE,"E7"),sQuery(id+"F0.wireOp",EDGE,"E8"),sQuery(id+"F0.wireOp",EDGE,"E9")])],"isStart":false});
            var sketch = newSketch(context, id + "F19", { "sketchPlane" : qUnion([Q0])});
            skCircle(sketch, "E85", {"center": v(-76.2, 25.4) * mm, "radius": 3.18 * mm});
            skCircle(sketch, "E86", {"center": v(-76.2, 0) * mm, "radius": 3.18 * mm});
            skLineSegment(sketch, "E87", {"start": v(-76.2, 3.18) * mm, "end": v(-73.03, 3.18) * mm});
            skLineSegment(sketch, "E88", {"start": v(-73.03, 3.18) * mm, "end": v(-73.03, 8.22) * mm});
            skLineSegment(sketch, "E89", {"start": v(-73.03, 8.22) * mm, "end": v(-76.2, 8.22) * mm});
            skLineSegment(sketch, "E90", {"start": v(-76.2, 10.18) * mm, "end": v(-73.03, 10.18) * mm});
            skLineSegment(sketch, "E91", {"start": v(-73.03, 10.18) * mm, "end": v(-73.03, 15.22) * mm});
            skLineSegment(sketch, "E92", {"start": v(-73.03, 15.22) * mm, "end": v(-76.2, 15.22) * mm});
            skLineSegment(sketch, "E93", {"start": v(-76.2, 17.18) * mm, "end": v(-73.03, 17.18) * mm});
            skLineSegment(sketch, "E94", {"start": v(-73.03, 17.18) * mm, "end": v(-73.03, 22.22) * mm});
            skLineSegment(sketch, "E95", {"start": v(-73.03, 22.22) * mm, "end": v(-76.2, 22.22) * mm});
            skLineSegment(sketch, "E96", {"start": v(-74.61, 8.22) * mm, "end": v(-74.61, 10.18) * mm, "construction": true});
            skLineSegment(sketch, "E97", {"start": v(-74.61, 15.22) * mm, "end": v(-74.61, 17.18) * mm, "construction": true});
            skSolve(sketch);
        }
        {
            var Q0;
            {var subQ0=sQuery(id+"F19.wireOp",EDGE,"E87");Q0=makeQuery(id+"F19.imprint","IMPRINT",FACE,{"disambiguationData":[TD([[makeQuery(id+"F19.imprint","IMPRINT",EDGE,{"derivedFrom":subQ0}),1.0]])]});}
            var Q1;
            {var subQ0=sQuery(id+"F19.wireOp",EDGE,"E90");Q1=makeQuery(id+"F19.imprint","IMPRINT",FACE,{"disambiguationData":[TD([[makeQuery(id+"F19.imprint","IMPRINT",EDGE,{"derivedFrom":subQ0}),1.0]])]});}
            var Q2;
            {var subQ0=sQuery(id+"F19.wireOp",EDGE,"E93");Q2=makeQuery(id+"F19.imprint","IMPRINT",FACE,{"disambiguationData":[TD([[makeQuery(id+"F19.imprint","IMPRINT",EDGE,{"derivedFrom":subQ0}),1.0]])]});}
            extrude(context, id + "F20", {"entities" : qUnion([Q0, Q1, Q2]), "operationType" : NewBodyOperationType.REMOVE, "oppositeDirection" : true, "depth" : 25.4 * mm, "offsetDistance" : 25.4 * mm});
        }
        {
            var Q0;
            {var subQ8=sQuery(id+"F13.wireOp",EDGE,"E48");Q0=makeQuery(id+"F13.imprint","IMPRINT",FACE,{"disambiguationData":[TD([[makeQuery(id+"F13.imprint","IMPRINT",EDGE,{"derivedFrom":subQ8}),-1.0]])]});}
            var sketch = newSketch(context, id + "F21", { "sketchPlane" : qUnion([Q0])});
            skCircle(sketch, "E98", {"center": v(-76.2, 0) * mm, "radius": 3.18 * mm});
            skCircle(sketch, "E99", {"center": v(0, -77.54) * mm, "radius": 3.18 * mm});
            skLineSegment(sketch, "E100", {"start": v(-76.2, 0) * mm, "end": v(0, -77.54) * mm});
            skLineSegment(sketch, "E101", {"start": v(-38.1, -38.77) * mm, "end": v(-24.6, -25.5) * mm, "construction": true});
            skLineSegment(sketch, "E102", {"start": v(-39.21, -37.64) * mm, "end": v(-36.95, -35.41) * mm});
            skLineSegment(sketch, "E103", {"start": v(-36.95, -35.41) * mm, "end": v(-34.72, -37.68) * mm});
            skLineSegment(sketch, "E104", {"start": v(-34.72, -37.68) * mm, "end": v(-36.99, -39.9) * mm});
            skLineSegment(sketch, "E105", {"start": v(-34.76, -42.17) * mm, "end": v(-32.5, -39.94) * mm});
            skLineSegment(sketch, "E106", {"start": v(-32.5, -39.94) * mm, "end": v(-30.27, -42.2) * mm});
            skLineSegment(sketch, "E107", {"start": v(-30.27, -42.2) * mm, "end": v(-32.54, -44.43) * mm});
            skLineSegment(sketch, "E108.1.0.0", {"start": v(-30.09, -46.93) * mm, "end": v(-27.82, -44.7) * mm});
            skLineSegment(sketch, "E108.1.0.1", {"start": v(-27.82, -44.7) * mm, "end": v(-25.6, -46.97) * mm});
            skLineSegment(sketch, "E108.1.0.2", {"start": v(-25.6, -46.97) * mm, "end": v(-27.86, -49.2) * mm});
            skLineSegment(sketch, "E108.2.0.0", {"start": v(-25.41, -51.68) * mm, "end": v(-23.15, -49.46) * mm});
            skLineSegment(sketch, "E108.2.0.1", {"start": v(-23.15, -49.46) * mm, "end": v(-20.92, -51.72) * mm});
            skLineSegment(sketch, "E108.2.0.2", {"start": v(-20.92, -51.72) * mm, "end": v(-23.18, -53.95) * mm});
            skLineSegment(sketch, "E108.direction1", {"start": v(-34.76, -42.17) * mm, "end": v(-30.09, -46.93) * mm, "construction": true});
            skLineSegment(sketch, "E109.0.3.0", {"start": v(-20.73, -56.44) * mm, "end": v(-18.47, -54.22) * mm});
            skLineSegment(sketch, "E109.3.3.0", {"start": v(-18.47, -54.22) * mm, "end": v(-16.24, -56.48) * mm});
            skLineSegment(sketch, "E109.6.3.0", {"start": v(-16.24, -56.48) * mm, "end": v(-18.5, -58.7) * mm});
            skLineSegment(sketch, "E109.0.4.0", {"start": v(-16.06, -61.2) * mm, "end": v(-13.8, -58.98) * mm});
            skLineSegment(sketch, "E109.3.4.0", {"start": v(-13.8, -58.98) * mm, "end": v(-11.57, -61.24) * mm});
            skLineSegment(sketch, "E109.6.4.0", {"start": v(-11.57, -61.24) * mm, "end": v(-13.83, -63.47) * mm});
            skLineSegment(sketch, "E109.0.5.0", {"start": v(-11.38, -65.96) * mm, "end": v(-9.12, -63.73) * mm});
            skLineSegment(sketch, "E109.3.5.0", {"start": v(-9.12, -63.73) * mm, "end": v(-6.9, -66) * mm});
            skLineSegment(sketch, "E109.6.5.0", {"start": v(-6.9, -66) * mm, "end": v(-9.16, -68.22) * mm});
            skLineSegment(sketch, "E109.0.6.0", {"start": v(-6.7, -70.72) * mm, "end": v(-4.44, -68.5) * mm});
            skLineSegment(sketch, "E109.3.6.0", {"start": v(-4.44, -68.5) * mm, "end": v(-2.22, -70.76) * mm});
            skLineSegment(sketch, "E109.6.6.0", {"start": v(-2.22, -70.76) * mm, "end": v(-4.48, -72.98) * mm});
            skLineSegment(sketch, "E110.MirrorCS", {"start": v(-41.44, -35.37) * mm, "end": v(-39.17, -33.15) * mm});
            skLineSegment(sketch, "E111.MirrorCS", {"start": v(-39.17, -33.15) * mm, "end": v(-41.4, -30.88) * mm});
            skLineSegment(sketch, "E112.MirrorCS", {"start": v(-41.4, -30.88) * mm, "end": v(-43.66, -33.1) * mm});
            skLineSegment(sketch, "E113.MirrorCS", {"start": v(-46.11, -30.62) * mm, "end": v(-43.85, -28.4) * mm});
            skLineSegment(sketch, "E114.MirrorCS", {"start": v(-43.85, -28.4) * mm, "end": v(-46.07, -26.13) * mm});
            skLineSegment(sketch, "E115.MirrorCS", {"start": v(-46.07, -26.13) * mm, "end": v(-48.34, -28.35) * mm});
            skLineSegment(sketch, "E116.MirrorCS", {"start": v(-50.79, -25.86) * mm, "end": v(-48.53, -23.63) * mm});
            skLineSegment(sketch, "E117.MirrorCS", {"start": v(-48.53, -23.63) * mm, "end": v(-50.75, -21.37) * mm});
            skLineSegment(sketch, "E118.MirrorCS", {"start": v(-50.75, -21.37) * mm, "end": v(-53.02, -23.6) * mm});
            skLineSegment(sketch, "E119.MirrorCS", {"start": v(-55.47, -21.1) * mm, "end": v(-53.2, -18.87) * mm});
            skLineSegment(sketch, "E120.MirrorCS", {"start": v(-53.2, -18.87) * mm, "end": v(-55.43, -16.6) * mm});
            skLineSegment(sketch, "E121.MirrorCS", {"start": v(-55.43, -16.6) * mm, "end": v(-57.7, -18.83) * mm});
            skLineSegment(sketch, "E122.MirrorCS", {"start": v(-60.14, -16.34) * mm, "end": v(-57.88, -14.12) * mm});
            skLineSegment(sketch, "E123.MirrorCS", {"start": v(-57.88, -14.12) * mm, "end": v(-60.1, -11.85) * mm});
            skLineSegment(sketch, "E124.MirrorCS", {"start": v(-60.1, -11.85) * mm, "end": v(-62.37, -14.08) * mm});
            skLineSegment(sketch, "E125.MirrorCS", {"start": v(-64.82, -11.58) * mm, "end": v(-62.55, -9.36) * mm});
            skLineSegment(sketch, "E126.MirrorCS", {"start": v(-62.55, -9.36) * mm, "end": v(-64.78, -7.1) * mm});
            skLineSegment(sketch, "E127.MirrorCS", {"start": v(-64.78, -7.1) * mm, "end": v(-67.04, -9.32) * mm});
            skLineSegment(sketch, "E128.MirrorCS", {"start": v(-69.5, -6.82) * mm, "end": v(-67.23, -4.6) * mm});
            skLineSegment(sketch, "E129.MirrorCS", {"start": v(-67.23, -4.6) * mm, "end": v(-69.45, -2.33) * mm});
            skLineSegment(sketch, "E130.MirrorCS", {"start": v(-69.45, -2.33) * mm, "end": v(-71.72, -4.56) * mm});
            skSolve(sketch);
        }
        {
            var Q0;
            {var subQ0=sQuery(id+"F21.wireOp",EDGE,"E128.MirrorCS");Q0=makeQuery(id+"F21.imprint","IMPRINT",FACE,{"disambiguationData":[TD([[makeQuery(id+"F21.imprint","IMPRINT",EDGE,{"derivedFrom":subQ0}),1.0]])]});}
            var Q1;
            {var subQ0=sQuery(id+"F21.wireOp",EDGE,"E125.MirrorCS");Q1=makeQuery(id+"F21.imprint","IMPRINT",FACE,{"disambiguationData":[TD([[makeQuery(id+"F21.imprint","IMPRINT",EDGE,{"derivedFrom":subQ0}),1.0]])]});}
            var Q2;
            {var subQ0=sQuery(id+"F21.wireOp",EDGE,"E122.MirrorCS");Q2=makeQuery(id+"F21.imprint","IMPRINT",FACE,{"disambiguationData":[TD([[makeQuery(id+"F21.imprint","IMPRINT",EDGE,{"derivedFrom":subQ0}),1.0]])]});}
            var Q3;
            {var subQ0=sQuery(id+"F21.wireOp",EDGE,"E119.MirrorCS");Q3=makeQuery(id+"F21.imprint","IMPRINT",FACE,{"disambiguationData":[TD([[makeQuery(id+"F21.imprint","IMPRINT",EDGE,{"derivedFrom":subQ0}),1.0]])]});}
            var Q4;
            {var subQ0=sQuery(id+"F21.wireOp",EDGE,"E116.MirrorCS");Q4=makeQuery(id+"F21.imprint","IMPRINT",FACE,{"disambiguationData":[TD([[makeQuery(id+"F21.imprint","IMPRINT",EDGE,{"derivedFrom":subQ0}),1.0]])]});}
            var Q5;
            {var subQ0=sQuery(id+"F21.wireOp",EDGE,"E113.MirrorCS");Q5=makeQuery(id+"F21.imprint","IMPRINT",FACE,{"disambiguationData":[TD([[makeQuery(id+"F21.imprint","IMPRINT",EDGE,{"derivedFrom":subQ0}),1.0]])]});}
            var Q6;
            {var subQ0=sQuery(id+"F21.wireOp",EDGE,"E110.MirrorCS");Q6=makeQuery(id+"F21.imprint","IMPRINT",FACE,{"disambiguationData":[TD([[makeQuery(id+"F21.imprint","IMPRINT",EDGE,{"derivedFrom":subQ0}),1.0]])]});}
            var Q7;
            {var subQ0=sQuery(id+"F21.wireOp",EDGE,"E102");Q7=makeQuery(id+"F21.imprint","IMPRINT",FACE,{"disambiguationData":[TD([[makeQuery(id+"F21.imprint","IMPRINT",EDGE,{"derivedFrom":subQ0}),-1.0]])]});}
            var Q8;
            {var subQ0=sQuery(id+"F21.wireOp",EDGE,"E105");Q8=makeQuery(id+"F21.imprint","IMPRINT",FACE,{"disambiguationData":[TD([[makeQuery(id+"F21.imprint","IMPRINT",EDGE,{"derivedFrom":subQ0}),-1.0]])]});}
            var Q9;
            {var subQ0=sQuery(id+"F21.wireOp",EDGE,"E108.1.0.0");Q9=makeQuery(id+"F21.imprint","IMPRINT",FACE,{"disambiguationData":[TD([[makeQuery(id+"F21.imprint","IMPRINT",EDGE,{"derivedFrom":subQ0}),-1.0]])]});}
            var Q10;
            {var subQ0=sQuery(id+"F21.wireOp",EDGE,"E108.2.0.0");Q10=makeQuery(id+"F21.imprint","IMPRINT",FACE,{"disambiguationData":[TD([[makeQuery(id+"F21.imprint","IMPRINT",EDGE,{"derivedFrom":subQ0}),-1.0]])]});}
            var Q11;
            {var subQ0=sQuery(id+"F21.wireOp",EDGE,"E109.0.3.0");Q11=makeQuery(id+"F21.imprint","IMPRINT",FACE,{"disambiguationData":[TD([[makeQuery(id+"F21.imprint","IMPRINT",EDGE,{"derivedFrom":subQ0}),-1.0]])]});}
            var Q12;
            {var subQ0=sQuery(id+"F21.wireOp",EDGE,"E109.0.4.0");Q12=makeQuery(id+"F21.imprint","IMPRINT",FACE,{"disambiguationData":[TD([[makeQuery(id+"F21.imprint","IMPRINT",EDGE,{"derivedFrom":subQ0}),-1.0]])]});}
            var Q13;
            {var subQ0=sQuery(id+"F21.wireOp",EDGE,"E109.0.5.0");Q13=makeQuery(id+"F21.imprint","IMPRINT",FACE,{"disambiguationData":[TD([[makeQuery(id+"F21.imprint","IMPRINT",EDGE,{"derivedFrom":subQ0}),-1.0]])]});}
            var Q14;
            {var subQ0=sQuery(id+"F21.wireOp",EDGE,"E109.0.6.0");Q14=makeQuery(id+"F21.imprint","IMPRINT",FACE,{"disambiguationData":[TD([[makeQuery(id+"F21.imprint","IMPRINT",EDGE,{"derivedFrom":subQ0}),-1.0]])]});}
            extrude(context, id + "F22", {"entities" : qUnion([Q0, Q1, Q2, Q3, Q4, Q5, Q6, Q7, Q8, Q9, Q10, Q11, Q12, Q13, Q14]), "operationType" : NewBodyOperationType.REMOVE, "oppositeDirection" : true, "depth" : 25.4 * mm, "offsetDistance" : 25.4 * mm});
        }
        {
            var Q0;
            Q0=makeQuery(id+"F1.opExtrude","CAP_VERTEX",VERTEX,{"disambiguationData":[OSD([sQuery(id+"F0.wireOp",EDGE,"E5"),sQuery(id+"F0.wireOp",EDGE,"E6")])],"isStart":false});
            var Q1;
            Q1=makeQuery(id+"F1.opExtrude","CAP_VERTEX",VERTEX,{"disambiguationData":[OSD([sQuery(id+"F0.wireOp",EDGE,"E0"),sQuery(id+"F0.wireOp",EDGE,"E1")])],"isStart":false});
            var Q2;
            Q2=makeQuery(id+"F1.opExtrude","CAP_VERTEX",VERTEX,{"disambiguationData":[OSD([sQuery(id+"F0.wireOp",EDGE,"E0"),sQuery(id+"F0.wireOp",EDGE,"E1")])],"isStart":true});
            cPlane(context, id + "F23", {"entities" : qUnion([Q0, Q1, Q2]), "cplaneType" : CPlaneType.THREE_POINT, "offset" : 25.4 * mm, "width" : 152.4 * mm, "height" : 152.4 * mm});
        }
        {
            var Q0;
            Q0=makeQuery(id+"F6.opExtrude","SWEPT_FACE",FACE,{"disambiguationData":[OSD([sQuery(id+"F0.wireOp",EDGE,"E0")])]});
            var sketch = newSketch(context, id + "F24", { "sketchPlane" : qUnion([Q0])});
            skLineSegment(sketch, "E131.0.0", {"start": v(48.91, 3.17) * mm, "end": v(48.91, 0) * mm});
            skLineSegment(sketch, "E131.0.1", {"start": v(48.91, 0) * mm, "end": v(55.3, 0) * mm});
            skLineSegment(sketch, "E131.0.2", {"start": v(55.3, 0) * mm, "end": v(55.3, 3.18) * mm});
            skLineSegment(sketch, "E131.0.3", {"start": v(55.3, 3.18) * mm, "end": v(48.91, 3.18) * mm});
            skPoint(sketch, "E132.0", {"position": v(43.99, 0) * mm});
            skLineSegment(sketch, "E133.0.0", {"start": v(42.24, 3.17) * mm, "end": v(42.24, 0) * mm});
            skLineSegment(sketch, "E133.0.1", {"start": v(42.24, 0) * mm, "end": v(45.74, 0) * mm});
            skLineSegment(sketch, "E133.0.2", {"start": v(45.74, 0) * mm, "end": v(45.74, 3.17) * mm});
            skLineSegment(sketch, "E133.0.3", {"start": v(45.74, 3.18) * mm, "end": v(42.24, 3.18) * mm});
            skLineSegment(sketch, "E134.0.0", {"start": v(35.57, 3.17) * mm, "end": v(35.57, 0) * mm});
            skLineSegment(sketch, "E134.0.1", {"start": v(35.57, 0) * mm, "end": v(39.07, 0) * mm});
            skLineSegment(sketch, "E134.0.2", {"start": v(39.07, 0) * mm, "end": v(39.07, 3.17) * mm});
            skLineSegment(sketch, "E134.0.3", {"start": v(39.07, 3.18) * mm, "end": v(35.57, 3.18) * mm});
            skLineSegment(sketch, "E135.0.0", {"start": v(28.9, 3.17) * mm, "end": v(28.9, 0) * mm});
            skLineSegment(sketch, "E135.0.1", {"start": v(28.9, 0) * mm, "end": v(32.4, 0) * mm});
            skLineSegment(sketch, "E135.0.2", {"start": v(32.4, 0) * mm, "end": v(32.4, 3.17) * mm});
            skLineSegment(sketch, "E135.0.3", {"start": v(32.4, 3.18) * mm, "end": v(28.9, 3.18) * mm});
            skLineSegment(sketch, "E136.0.0", {"start": v(22.23, 3.17) * mm, "end": v(22.23, 0) * mm});
            skLineSegment(sketch, "E136.0.1", {"start": v(22.23, 0) * mm, "end": v(25.72, 0) * mm});
            skLineSegment(sketch, "E136.0.2", {"start": v(25.72, 0) * mm, "end": v(25.72, 3.17) * mm});
            skLineSegment(sketch, "E136.0.3", {"start": v(25.72, 3.18) * mm, "end": v(22.23, 3.18) * mm});
            skLineSegment(sketch, "E137.0.0", {"start": v(15.56, 3.17) * mm, "end": v(15.56, 0) * mm});
            skLineSegment(sketch, "E137.0.1", {"start": v(15.56, 0) * mm, "end": v(19.05, 0) * mm});
            skLineSegment(sketch, "E137.0.2", {"start": v(19.05, 0) * mm, "end": v(19.05, 3.17) * mm});
            skLineSegment(sketch, "E137.0.3", {"start": v(19.05, 3.18) * mm, "end": v(15.56, 3.18) * mm});
            skLineSegment(sketch, "E138.0.0", {"start": v(8.89, 3.17) * mm, "end": v(8.89, 0) * mm});
            skLineSegment(sketch, "E138.0.1", {"start": v(8.89, 0) * mm, "end": v(12.38, 0) * mm});
            skLineSegment(sketch, "E138.0.2", {"start": v(12.38, 0) * mm, "end": v(12.38, 3.17) * mm});
            skLineSegment(sketch, "E138.0.3", {"start": v(12.38, 3.18) * mm, "end": v(8.89, 3.18) * mm});
            skLineSegment(sketch, "E139.0.0", {"start": v(2.54, 3.17) * mm, "end": v(2.54, 0) * mm});
            skLineSegment(sketch, "E139.0.1", {"start": v(2.54, 0) * mm, "end": v(5.71, 0) * mm});
            skLineSegment(sketch, "E139.0.2", {"start": v(5.71, 0) * mm, "end": v(5.71, 3.17) * mm});
            skLineSegment(sketch, "E139.0.3", {"start": v(5.71, 3.18) * mm, "end": v(2.54, 3.18) * mm});
            skLineSegment(sketch, "E140.0.0", {"start": v(-3.81, 3.17) * mm, "end": v(-3.81, 0) * mm});
            skLineSegment(sketch, "E140.0.1", {"start": v(-3.81, 0) * mm, "end": v(-0.64, 0) * mm});
            skLineSegment(sketch, "E140.0.2", {"start": v(-0.64, 0) * mm, "end": v(-0.64, 3.17) * mm});
            skLineSegment(sketch, "E140.0.3", {"start": v(-0.64, 3.18) * mm, "end": v(-3.81, 3.18) * mm});
            skLineSegment(sketch, "E141.0.0", {"start": v(-10.48, 3.17) * mm, "end": v(-10.48, 0) * mm});
            skLineSegment(sketch, "E141.0.1", {"start": v(-10.48, 0) * mm, "end": v(-6.99, 0) * mm});
            skLineSegment(sketch, "E141.0.2", {"start": v(-6.99, 0) * mm, "end": v(-6.99, 3.17) * mm});
            skLineSegment(sketch, "E141.0.3", {"start": v(-6.99, 3.18) * mm, "end": v(-10.48, 3.18) * mm});
            skLineSegment(sketch, "E142.0.0", {"start": v(-17.16, 3.17) * mm, "end": v(-17.16, 0) * mm});
            skLineSegment(sketch, "E142.0.1", {"start": v(-17.16, 0) * mm, "end": v(-13.66, 0) * mm});
            skLineSegment(sketch, "E142.0.2", {"start": v(-13.66, 0) * mm, "end": v(-13.66, 3.17) * mm});
            skLineSegment(sketch, "E142.0.3", {"start": v(-13.66, 3.18) * mm, "end": v(-17.16, 3.18) * mm});
            skLineSegment(sketch, "E143.0.0", {"start": v(-23.83, 3.17) * mm, "end": v(-23.83, 0) * mm});
            skLineSegment(sketch, "E143.0.1", {"start": v(-23.83, 0) * mm, "end": v(-20.33, 0) * mm});
            skLineSegment(sketch, "E143.0.2", {"start": v(-20.33, 0) * mm, "end": v(-20.33, 3.17) * mm});
            skLineSegment(sketch, "E143.0.3", {"start": v(-20.33, 3.18) * mm, "end": v(-23.83, 3.18) * mm});
            skLineSegment(sketch, "E144.0.0", {"start": v(-43.84, 3.17) * mm, "end": v(-43.84, 0) * mm});
            skLineSegment(sketch, "E144.0.1", {"start": v(-43.84, 0) * mm, "end": v(-40.34, 0) * mm});
            skLineSegment(sketch, "E144.0.2", {"start": v(-40.34, 0) * mm, "end": v(-40.34, 3.17) * mm});
            skLineSegment(sketch, "E144.0.3", {"start": v(-40.34, 3.18) * mm, "end": v(-43.84, 3.18) * mm});
            skLineSegment(sketch, "E145.0.0", {"start": v(-37.17, 3.17) * mm, "end": v(-37.17, 0) * mm});
            skLineSegment(sketch, "E145.0.1", {"start": v(-37.17, 0) * mm, "end": v(-33.67, 0) * mm});
            skLineSegment(sketch, "E145.0.2", {"start": v(-33.67, 0) * mm, "end": v(-33.67, 3.17) * mm});
            skLineSegment(sketch, "E145.0.3", {"start": v(-33.67, 3.18) * mm, "end": v(-37.17, 3.18) * mm});
            skLineSegment(sketch, "E146.0.0", {"start": v(-30.5, 3.17) * mm, "end": v(-30.5, 0) * mm});
            skLineSegment(sketch, "E146.0.1", {"start": v(-30.5, 0) * mm, "end": v(-27, 0) * mm});
            skLineSegment(sketch, "E146.0.2", {"start": v(-27, 0) * mm, "end": v(-27, 3.17) * mm});
            skLineSegment(sketch, "E146.0.3", {"start": v(-27, 3.18) * mm, "end": v(-30.5, 3.18) * mm});
            skLineSegment(sketch, "E147.0.0", {"start": v(-53.4, 0) * mm, "end": v(-47.02, 0) * mm});
            skLineSegment(sketch, "E147.0.1", {"start": v(-47.02, 0) * mm, "end": v(-47.02, 3.17) * mm});
            skLineSegment(sketch, "E147.0.2", {"start": v(-47.02, 3.18) * mm, "end": v(-53.4, 3.18) * mm});
            skLineSegment(sketch, "E147.0.3", {"start": v(-53.4, 3.18) * mm, "end": v(-53.4, 0) * mm});
            skSolve(sketch);
        }
        {
            var Q0;
            Q0=qSketchRegion(id+"F24",true);
            extrude(context, id + "F25", {"entities" : qUnion([Q0]), "operationType" : NewBodyOperationType.REMOVE, "endBound" : BoundingType.SYMMETRIC, "oppositeDirection" : true, "depth" : 25.4 * mm, "offsetDistance" : 25.4 * mm});
        }
        {
            var Q0;
            Q0=makeQuery(id+"F3.opExtrude","SWEPT_FACE",FACE,{"disambiguationData":[OSD([sQuery(id+"F0.wireOp",EDGE,"E7")])]});
            var sketch = newSketch(context, id + "F26", { "sketchPlane" : qUnion([Q0])});
            skLineSegment(sketch, "E148.0.0", {"start": v(57.15, 3.17) * mm, "end": v(57.15, 0) * mm});
            skLineSegment(sketch, "E148.0.1", {"start": v(57.15, 0) * mm, "end": v(60.32, 0) * mm});
            skLineSegment(sketch, "E148.0.2", {"start": v(60.32, 0) * mm, "end": v(60.32, 3.18) * mm});
            skLineSegment(sketch, "E148.0.3", {"start": v(60.32, 3.18) * mm, "end": v(57.15, 3.18) * mm});
            skLineSegment(sketch, "E149.0.0", {"start": v(44.45, 0) * mm, "end": v(50.8, 0) * mm});
            skLineSegment(sketch, "E149.0.1", {"start": v(50.8, 0) * mm, "end": v(50.8, 3.17) * mm});
            skLineSegment(sketch, "E149.0.2", {"start": v(50.8, 3.18) * mm, "end": v(44.45, 3.18) * mm});
            skLineSegment(sketch, "E149.0.3", {"start": v(44.45, 3.17) * mm, "end": v(44.45, 0) * mm});
            skLineSegment(sketch, "E150.0.0", {"start": v(31.75, 0) * mm, "end": v(38.1, 0) * mm});
            skLineSegment(sketch, "E150.0.1", {"start": v(38.1, 0) * mm, "end": v(38.1, 3.17) * mm});
            skLineSegment(sketch, "E150.0.2", {"start": v(38.1, 3.18) * mm, "end": v(31.75, 3.18) * mm});
            skLineSegment(sketch, "E150.0.3", {"start": v(31.75, 3.17) * mm, "end": v(31.75, 0) * mm});
            skLineSegment(sketch, "E151.0.0", {"start": v(22.23, 0) * mm, "end": v(25.4, 0) * mm});
            skLineSegment(sketch, "E151.0.1", {"start": v(25.4, 0) * mm, "end": v(25.4, 3.17) * mm});
            skLineSegment(sketch, "E151.0.2", {"start": v(25.4, 3.18) * mm, "end": v(22.23, 3.18) * mm});
            skLineSegment(sketch, "E151.0.3", {"start": v(22.23, 3.18) * mm, "end": v(22.23, 0) * mm});
            skSolve(sketch);
        }
        {
            var Q0;
            Q0=qSketchRegion(id+"F26",true);
            extrude(context, id + "F27", {"entities" : qUnion([Q0]), "operationType" : NewBodyOperationType.REMOVE, "oppositeDirection" : true, "depth" : 25.4 * mm, "offsetDistance" : 25.4 * mm});
        }
        {
            var Q0;
            Q0=makeQuery(id+"F4.opExtrude","SWEPT_FACE",FACE,{"disambiguationData":[OSD([sQuery(id+"F0.wireOp",EDGE,"E8")])]});
            var sketch = newSketch(context, id + "F28", { "sketchPlane" : qUnion([Q0])});
            skLineSegment(sketch, "E152.0.0", {"start": v(12.93, 3.17) * mm, "end": v(12.93, 0) * mm});
            skLineSegment(sketch, "E152.0.1", {"start": v(12.93, 0) * mm, "end": v(16.1, 0) * mm});
            skLineSegment(sketch, "E152.0.2", {"start": v(16.1, 0) * mm, "end": v(16.1, 3.18) * mm});
            skLineSegment(sketch, "E152.0.3", {"start": v(16.1, 3.18) * mm, "end": v(12.93, 3.18) * mm});
            skLineSegment(sketch, "E153.0.0", {"start": v(1.98, 0) * mm, "end": v(9.42, 0) * mm});
            skLineSegment(sketch, "E153.0.1", {"start": v(9.42, 0) * mm, "end": v(9.42, 3.17) * mm});
            skLineSegment(sketch, "E153.0.2", {"start": v(9.42, 3.18) * mm, "end": v(1.98, 3.18) * mm});
            skLineSegment(sketch, "E153.0.3", {"start": v(1.98, 3.17) * mm, "end": v(1.98, 0) * mm});
            skLineSegment(sketch, "E154.0.0", {"start": v(-8.96, 0) * mm, "end": v(-1.53, 0) * mm});
            skLineSegment(sketch, "E154.0.1", {"start": v(-1.53, 0) * mm, "end": v(-1.53, 3.17) * mm});
            skLineSegment(sketch, "E154.0.2", {"start": v(-1.53, 3.18) * mm, "end": v(-8.96, 3.18) * mm});
            skLineSegment(sketch, "E154.0.3", {"start": v(-8.96, 3.17) * mm, "end": v(-8.96, 0) * mm});
            skLineSegment(sketch, "E155.0.0", {"start": v(-15.65, 0) * mm, "end": v(-12.47, 0) * mm});
            skLineSegment(sketch, "E155.0.1", {"start": v(-12.47, 0) * mm, "end": v(-12.47, 3.17) * mm});
            skLineSegment(sketch, "E155.0.2", {"start": v(-12.47, 3.18) * mm, "end": v(-15.65, 3.18) * mm});
            skLineSegment(sketch, "E155.0.3", {"start": v(-15.65, 3.18) * mm, "end": v(-15.65, 0) * mm});
            skSolve(sketch);
        }
        {
            var Q0;
            Q0=qSketchRegion(id+"F28",true);
            extrude(context, id + "F29", {"entities" : qUnion([Q0]), "operationType" : NewBodyOperationType.REMOVE, "oppositeDirection" : true, "depth" : 25.4 * mm, "offsetDistance" : 25.4 * mm});
        }
        {
            var Q0;
            Q0=makeQuery(id+"F5.opExtrude","SWEPT_FACE",FACE,{"disambiguationData":[OSD([sQuery(id+"F0.wireOp",EDGE,"E9")])]});
            var sketch = newSketch(context, id + "F30", { "sketchPlane" : qUnion([Q0])});
            skLineSegment(sketch, "E156.0.0", {"start": v(-3.17, 3.17) * mm, "end": v(-3.17, 0) * mm});
            skLineSegment(sketch, "E156.0.1", {"start": v(-3.17, 0) * mm, "end": v(0, 0) * mm});
            skLineSegment(sketch, "E156.0.2", {"start": v(0, 0) * mm, "end": v(0, 3.18) * mm});
            skLineSegment(sketch, "E156.0.3", {"start": v(0, 3.18) * mm, "end": v(-3.17, 3.18) * mm});
            skPoint(sketch, "E157.0", {"position": v(-10.18, 1.59) * mm});
            skLineSegment(sketch, "E158.0.0", {"start": v(-10.18, 0) * mm, "end": v(-8.22, 0) * mm});
            skLineSegment(sketch, "E158.0.1", {"start": v(-8.22, 0) * mm, "end": v(-8.22, 3.17) * mm});
            skLineSegment(sketch, "E158.0.2", {"start": v(-8.22, 3.18) * mm, "end": v(-10.18, 3.18) * mm});
            skLineSegment(sketch, "E158.0.3", {"start": v(-10.18, 3.17) * mm, "end": v(-10.18, 0) * mm});
            skLineSegment(sketch, "E159.0.0", {"start": v(-17.18, 0) * mm, "end": v(-15.22, 0) * mm});
            skLineSegment(sketch, "E159.0.1", {"start": v(-15.22, 0) * mm, "end": v(-15.22, 3.17) * mm});
            skLineSegment(sketch, "E159.0.2", {"start": v(-15.22, 3.18) * mm, "end": v(-17.18, 3.18) * mm});
            skLineSegment(sketch, "E159.0.3", {"start": v(-17.18, 3.17) * mm, "end": v(-17.18, 0) * mm});
            skLineSegment(sketch, "E160.0.0", {"start": v(-25.4, 0) * mm, "end": v(-22.22, 0) * mm});
            skLineSegment(sketch, "E160.0.1", {"start": v(-22.22, 0) * mm, "end": v(-22.22, 3.17) * mm});
            skLineSegment(sketch, "E160.0.2", {"start": v(-22.22, 3.18) * mm, "end": v(-25.4, 3.18) * mm});
            skLineSegment(sketch, "E160.0.3", {"start": v(-25.4, 3.18) * mm, "end": v(-25.4, 0) * mm});
            skSolve(sketch);
        }
        {
            var Q0;
            Q0=qSketchRegion(id+"F30",true);
            extrude(context, id + "F31", {"entities" : qUnion([Q0]), "operationType" : NewBodyOperationType.REMOVE, "oppositeDirection" : true, "depth" : 25.4 * mm, "offsetDistance" : 25.4 * mm});
        }
        {
            var Q0;
            Q0=makeQuery(id+"F6.opExtrude","SWEPT_FACE",FACE,{"disambiguationData":[OSD([sQuery(id+"F0.wireOp",EDGE,"E0")])]});
            var sketch = newSketch(context, id + "F32", { "sketchPlane" : qUnion([Q0])});
            skLineSegment(sketch, "E161.0.0", {"start": v(42.24, 3.17) * mm, "end": v(42.24, 0) * mm});
            skLineSegment(sketch, "E161.0.1", {"start": v(42.24, 0) * mm, "end": v(45.74, 0) * mm});
            skLineSegment(sketch, "E161.0.2", {"start": v(45.74, 0) * mm, "end": v(45.74, 3.17) * mm});
            skLineSegment(sketch, "E161.0.3", {"start": v(45.74, 3.18) * mm, "end": v(42.24, 3.18) * mm});
            skLineSegment(sketch, "E162.0.0", {"start": v(35.57, 3.17) * mm, "end": v(35.57, 0) * mm});
            skLineSegment(sketch, "E162.0.1", {"start": v(35.57, 0) * mm, "end": v(39.07, 0) * mm});
            skLineSegment(sketch, "E162.0.2", {"start": v(39.07, 0) * mm, "end": v(39.07, 3.17) * mm});
            skLineSegment(sketch, "E162.0.3", {"start": v(39.07, 3.18) * mm, "end": v(35.57, 3.18) * mm});
            skLineSegment(sketch, "E163.0.0", {"start": v(28.9, 3.17) * mm, "end": v(28.9, 0) * mm});
            skLineSegment(sketch, "E163.0.1", {"start": v(28.9, 0) * mm, "end": v(32.4, 0) * mm});
            skLineSegment(sketch, "E163.0.2", {"start": v(32.4, 0) * mm, "end": v(32.4, 3.17) * mm});
            skLineSegment(sketch, "E163.0.3", {"start": v(32.4, 3.18) * mm, "end": v(28.9, 3.18) * mm});
            skLineSegment(sketch, "E164.0.0", {"start": v(22.23, 3.17) * mm, "end": v(22.23, 0) * mm});
            skLineSegment(sketch, "E164.0.1", {"start": v(22.23, 0) * mm, "end": v(25.72, 0) * mm});
            skLineSegment(sketch, "E164.0.2", {"start": v(25.72, 0) * mm, "end": v(25.72, 3.17) * mm});
            skLineSegment(sketch, "E164.0.3", {"start": v(25.72, 3.18) * mm, "end": v(22.23, 3.18) * mm});
            skLineSegment(sketch, "E165.0.0", {"start": v(15.56, 3.17) * mm, "end": v(15.56, 0) * mm});
            skLineSegment(sketch, "E165.0.1", {"start": v(15.56, 0) * mm, "end": v(19.05, 0) * mm});
            skLineSegment(sketch, "E165.0.2", {"start": v(19.05, 0) * mm, "end": v(19.05, 3.17) * mm});
            skLineSegment(sketch, "E165.0.3", {"start": v(19.05, 3.18) * mm, "end": v(15.56, 3.18) * mm});
            skLineSegment(sketch, "E166.0.0", {"start": v(8.89, 3.17) * mm, "end": v(8.89, 0) * mm});
            skLineSegment(sketch, "E166.0.1", {"start": v(8.89, 0) * mm, "end": v(12.38, 0) * mm});
            skLineSegment(sketch, "E166.0.2", {"start": v(12.38, 0) * mm, "end": v(12.38, 3.17) * mm});
            skLineSegment(sketch, "E166.0.3", {"start": v(12.38, 3.18) * mm, "end": v(8.89, 3.18) * mm});
            skLineSegment(sketch, "E167.0.0", {"start": v(2.54, 3.17) * mm, "end": v(2.54, 0) * mm});
            skLineSegment(sketch, "E167.0.1", {"start": v(2.54, 0) * mm, "end": v(5.71, 0) * mm});
            skLineSegment(sketch, "E167.0.2", {"start": v(5.71, 0) * mm, "end": v(5.71, 3.17) * mm});
            skLineSegment(sketch, "E167.0.3", {"start": v(5.71, 3.18) * mm, "end": v(2.54, 3.18) * mm});
            skLineSegment(sketch, "E168.0.0", {"start": v(-3.81, 3.17) * mm, "end": v(-3.81, 0) * mm});
            skLineSegment(sketch, "E168.0.1", {"start": v(-3.81, 0) * mm, "end": v(-0.64, 0) * mm});
            skLineSegment(sketch, "E168.0.2", {"start": v(-0.64, 0) * mm, "end": v(-0.64, 3.17) * mm});
            skLineSegment(sketch, "E168.0.3", {"start": v(-0.64, 3.18) * mm, "end": v(-3.81, 3.18) * mm});
            skLineSegment(sketch, "E169.0.0", {"start": v(-10.48, 3.17) * mm, "end": v(-10.48, 0) * mm});
            skLineSegment(sketch, "E169.0.1", {"start": v(-10.48, 0) * mm, "end": v(-6.99, 0) * mm});
            skLineSegment(sketch, "E169.0.2", {"start": v(-6.99, 0) * mm, "end": v(-6.99, 3.17) * mm});
            skLineSegment(sketch, "E169.0.3", {"start": v(-6.99, 3.18) * mm, "end": v(-10.48, 3.18) * mm});
            skLineSegment(sketch, "E170.0.0", {"start": v(-17.16, 3.17) * mm, "end": v(-17.16, 0) * mm});
            skLineSegment(sketch, "E170.0.1", {"start": v(-17.16, 0) * mm, "end": v(-13.66, 0) * mm});
            skLineSegment(sketch, "E170.0.2", {"start": v(-13.66, 0) * mm, "end": v(-13.66, 3.17) * mm});
            skLineSegment(sketch, "E170.0.3", {"start": v(-13.66, 3.18) * mm, "end": v(-17.16, 3.18) * mm});
            skLineSegment(sketch, "E171.0.0", {"start": v(-23.83, 3.17) * mm, "end": v(-23.83, 0) * mm});
            skLineSegment(sketch, "E171.0.1", {"start": v(-23.83, 0) * mm, "end": v(-20.33, 0) * mm});
            skLineSegment(sketch, "E171.0.2", {"start": v(-20.33, 0) * mm, "end": v(-20.33, 3.17) * mm});
            skLineSegment(sketch, "E171.0.3", {"start": v(-20.33, 3.18) * mm, "end": v(-23.83, 3.18) * mm});
            skLineSegment(sketch, "E172.0.0", {"start": v(-30.5, 3.17) * mm, "end": v(-30.5, 0) * mm});
            skLineSegment(sketch, "E172.0.1", {"start": v(-30.5, 0) * mm, "end": v(-27, 0) * mm});
            skLineSegment(sketch, "E172.0.2", {"start": v(-27, 0) * mm, "end": v(-27, 3.17) * mm});
            skLineSegment(sketch, "E172.0.3", {"start": v(-27, 3.18) * mm, "end": v(-30.5, 3.18) * mm});
            skLineSegment(sketch, "E173.0.0", {"start": v(-37.17, 3.17) * mm, "end": v(-37.17, 0) * mm});
            skLineSegment(sketch, "E173.0.1", {"start": v(-37.17, 0) * mm, "end": v(-33.67, 0) * mm});
            skLineSegment(sketch, "E173.0.2", {"start": v(-33.67, 0) * mm, "end": v(-33.67, 3.17) * mm});
            skLineSegment(sketch, "E173.0.3", {"start": v(-33.67, 3.18) * mm, "end": v(-37.17, 3.18) * mm});
            skLineSegment(sketch, "E174.0.0", {"start": v(-43.84, 3.17) * mm, "end": v(-43.84, 0) * mm});
            skLineSegment(sketch, "E174.0.1", {"start": v(-43.84, 0) * mm, "end": v(-40.34, 0) * mm});
            skLineSegment(sketch, "E174.0.2", {"start": v(-40.34, 0) * mm, "end": v(-40.34, 3.17) * mm});
            skLineSegment(sketch, "E174.0.3", {"start": v(-40.34, 3.18) * mm, "end": v(-43.84, 3.18) * mm});
            skSolve(sketch);
        }
        {
            var Q0;
            Q0=qSketchRegion(id+"F32",true);
            extrude(context, id + "F33", {"entities" : qUnion([Q0]), "operationType" : NewBodyOperationType.REMOVE, "oppositeDirection" : true, "depth" : 25.4 * mm, "offsetDistance" : 25.4 * mm});
        }
        {
            var Q0;
            Q0=makeQuery(id+"F7.opExtrude","SWEPT_FACE",FACE,{"disambiguationData":[OSD([sQuery(id+"F0.wireOp",EDGE,"E1")])]});
            var sketch = newSketch(context, id + "F34", { "sketchPlane" : qUnion([Q0])});
            skLineSegment(sketch, "E175.0.0", {"start": v(47.02, 3.17) * mm, "end": v(47.02, 0) * mm});
            skLineSegment(sketch, "E175.0.1", {"start": v(47.02, 0) * mm, "end": v(53.4, 0) * mm});
            skLineSegment(sketch, "E175.0.2", {"start": v(53.4, 0) * mm, "end": v(53.4, 3.18) * mm});
            skLineSegment(sketch, "E175.0.3", {"start": v(53.4, 3.18) * mm, "end": v(47.02, 3.18) * mm});
            skLineSegment(sketch, "E176.0.0", {"start": v(43.84, 0) * mm, "end": v(43.84, 3.17) * mm});
            skLineSegment(sketch, "E176.0.1", {"start": v(43.84, 3.18) * mm, "end": v(40.34, 3.18) * mm});
            skLineSegment(sketch, "E176.0.2", {"start": v(40.34, 3.17) * mm, "end": v(40.34, 0) * mm});
            skLineSegment(sketch, "E176.0.3", {"start": v(40.34, 0) * mm, "end": v(43.84, 0) * mm});
            skLineSegment(sketch, "E177.0.0", {"start": v(37.17, 0) * mm, "end": v(37.17, 3.17) * mm});
            skLineSegment(sketch, "E177.0.1", {"start": v(37.17, 3.18) * mm, "end": v(33.67, 3.18) * mm});
            skLineSegment(sketch, "E177.0.2", {"start": v(33.67, 3.17) * mm, "end": v(33.67, 0) * mm});
            skLineSegment(sketch, "E177.0.3", {"start": v(33.67, 0) * mm, "end": v(37.17, 0) * mm});
            skLineSegment(sketch, "E178.0.0", {"start": v(30.5, 0) * mm, "end": v(30.5, 3.17) * mm});
            skLineSegment(sketch, "E178.0.1", {"start": v(30.5, 3.18) * mm, "end": v(27, 3.18) * mm});
            skLineSegment(sketch, "E178.0.2", {"start": v(27, 3.17) * mm, "end": v(27, 0) * mm});
            skLineSegment(sketch, "E178.0.3", {"start": v(27, 0) * mm, "end": v(30.5, 0) * mm});
            skLineSegment(sketch, "E179.0.0", {"start": v(23.83, 0) * mm, "end": v(23.83, 3.17) * mm});
            skLineSegment(sketch, "E179.0.1", {"start": v(23.83, 3.18) * mm, "end": v(20.33, 3.18) * mm});
            skLineSegment(sketch, "E179.0.2", {"start": v(20.33, 3.17) * mm, "end": v(20.33, 0) * mm});
            skLineSegment(sketch, "E179.0.3", {"start": v(20.33, 0) * mm, "end": v(23.83, 0) * mm});
            skLineSegment(sketch, "E180.0.0", {"start": v(17.16, 0) * mm, "end": v(17.16, 3.17) * mm});
            skLineSegment(sketch, "E180.0.1", {"start": v(17.16, 3.18) * mm, "end": v(13.66, 3.18) * mm});
            skLineSegment(sketch, "E180.0.2", {"start": v(13.66, 3.17) * mm, "end": v(13.66, 0) * mm});
            skLineSegment(sketch, "E180.0.3", {"start": v(13.66, 0) * mm, "end": v(17.16, 0) * mm});
            skLineSegment(sketch, "E181.0.0", {"start": v(-55.3, 0) * mm, "end": v(-48.91, 0) * mm});
            skLineSegment(sketch, "E181.0.1", {"start": v(-48.91, 0) * mm, "end": v(-48.91, 3.17) * mm});
            skLineSegment(sketch, "E181.0.2", {"start": v(-48.91, 3.18) * mm, "end": v(-55.3, 3.18) * mm});
            skLineSegment(sketch, "E181.0.3", {"start": v(-55.3, 3.18) * mm, "end": v(-55.3, 0) * mm});
            skLineSegment(sketch, "E182.0.0", {"start": v(-45.74, 0) * mm, "end": v(-42.24, 0) * mm});
            skLineSegment(sketch, "E182.0.1", {"start": v(-42.24, 0) * mm, "end": v(-42.24, 3.17) * mm});
            skLineSegment(sketch, "E182.0.2", {"start": v(-42.24, 3.18) * mm, "end": v(-45.74, 3.18) * mm});
            skLineSegment(sketch, "E182.0.3", {"start": v(-45.74, 3.17) * mm, "end": v(-45.74, 0) * mm});
            skLineSegment(sketch, "E183.0.0", {"start": v(-39.07, 0) * mm, "end": v(-35.57, 0) * mm});
            skLineSegment(sketch, "E183.0.1", {"start": v(-35.57, 0) * mm, "end": v(-35.57, 3.17) * mm});
            skLineSegment(sketch, "E183.0.2", {"start": v(-35.57, 3.18) * mm, "end": v(-39.07, 3.18) * mm});
            skLineSegment(sketch, "E183.0.3", {"start": v(-39.07, 3.17) * mm, "end": v(-39.07, 0) * mm});
            skLineSegment(sketch, "E184.0.0", {"start": v(-32.4, 0) * mm, "end": v(-28.9, 0) * mm});
            skLineSegment(sketch, "E184.0.1", {"start": v(-28.9, 0) * mm, "end": v(-28.9, 3.17) * mm});
            skLineSegment(sketch, "E184.0.2", {"start": v(-28.9, 3.18) * mm, "end": v(-32.4, 3.18) * mm});
            skLineSegment(sketch, "E184.0.3", {"start": v(-32.4, 3.17) * mm, "end": v(-32.4, 0) * mm});
            skLineSegment(sketch, "E185.0.0", {"start": v(-25.72, 0) * mm, "end": v(-22.23, 0) * mm});
            skLineSegment(sketch, "E185.0.1", {"start": v(-22.23, 0) * mm, "end": v(-22.23, 3.17) * mm});
            skLineSegment(sketch, "E185.0.2", {"start": v(-22.23, 3.18) * mm, "end": v(-25.72, 3.18) * mm});
            skLineSegment(sketch, "E185.0.3", {"start": v(-25.72, 3.17) * mm, "end": v(-25.72, 0) * mm});
            skLineSegment(sketch, "E186.0.0", {"start": v(-19.05, 0) * mm, "end": v(-15.56, 0) * mm});
            skLineSegment(sketch, "E186.0.1", {"start": v(-15.56, 0) * mm, "end": v(-15.56, 3.17) * mm});
            skLineSegment(sketch, "E186.0.2", {"start": v(-15.56, 3.18) * mm, "end": v(-19.05, 3.18) * mm});
            skLineSegment(sketch, "E186.0.3", {"start": v(-19.05, 3.17) * mm, "end": v(-19.05, 0) * mm});
            skPoint(sketch, "E187.0", {"position": v(-8.89, 1.59) * mm});
            skLineSegment(sketch, "E188.0.0", {"start": v(-5.71, 0) * mm, "end": v(-2.54, 0) * mm});
            skLineSegment(sketch, "E188.0.1", {"start": v(-2.54, 0) * mm, "end": v(-2.54, 3.17) * mm});
            skLineSegment(sketch, "E188.0.2", {"start": v(-2.54, 3.18) * mm, "end": v(-5.71, 3.18) * mm});
            skLineSegment(sketch, "E188.0.3", {"start": v(-5.71, 3.17) * mm, "end": v(-5.71, 0) * mm});
            skLineSegment(sketch, "E189.0.0", {"start": v(-12.38, 0) * mm, "end": v(-8.89, 0) * mm});
            skLineSegment(sketch, "E189.0.1", {"start": v(-8.89, 0) * mm, "end": v(-8.89, 3.17) * mm});
            skLineSegment(sketch, "E189.0.2", {"start": v(-8.89, 3.18) * mm, "end": v(-12.38, 3.18) * mm});
            skLineSegment(sketch, "E189.0.3", {"start": v(-12.38, 3.17) * mm, "end": v(-12.38, 0) * mm});
            skLineSegment(sketch, "E190.0.0", {"start": v(3.81, 0) * mm, "end": v(3.81, 3.17) * mm});
            skLineSegment(sketch, "E190.0.1", {"start": v(3.81, 3.18) * mm, "end": v(0.64, 3.18) * mm});
            skLineSegment(sketch, "E190.0.2", {"start": v(0.64, 3.17) * mm, "end": v(0.64, 0) * mm});
            skLineSegment(sketch, "E190.0.3", {"start": v(0.64, 0) * mm, "end": v(3.81, 0) * mm});
            skLineSegment(sketch, "E191.0.0", {"start": v(10.48, 0) * mm, "end": v(10.48, 3.17) * mm});
            skLineSegment(sketch, "E191.0.1", {"start": v(10.48, 3.18) * mm, "end": v(6.99, 3.18) * mm});
            skLineSegment(sketch, "E191.0.2", {"start": v(6.99, 3.17) * mm, "end": v(6.99, 0) * mm});
            skLineSegment(sketch, "E191.0.3", {"start": v(6.99, 0) * mm, "end": v(10.48, 0) * mm});
            skSolve(sketch);
        }
        {
            var Q0;
            Q0=qSketchRegion(id+"F34",true);
            extrude(context, id + "F35", {"entities" : qUnion([Q0]), "operationType" : NewBodyOperationType.REMOVE, "oppositeDirection" : true, "depth" : 25.4 * mm, "offsetDistance" : 25.4 * mm});
        }
        {
            var Q0;
            Q0=makeQuery(id+"F8.opExtrude","SWEPT_FACE",FACE,{"disambiguationData":[OSD([sQuery(id+"F0.wireOp",EDGE,"E2")])]});
            var sketch = newSketch(context, id + "F36", { "sketchPlane" : qUnion([Q0])});
            skLineSegment(sketch, "E192.0.0", {"start": v(22.23, 3.17) * mm, "end": v(22.23, 0) * mm});
            skLineSegment(sketch, "E192.0.1", {"start": v(22.23, 0) * mm, "end": v(25.4, 0) * mm});
            skLineSegment(sketch, "E192.0.2", {"start": v(25.4, 0) * mm, "end": v(25.4, 3.18) * mm});
            skLineSegment(sketch, "E192.0.3", {"start": v(25.4, 3.18) * mm, "end": v(22.23, 3.18) * mm});
            skLineSegment(sketch, "E193.0.0", {"start": v(15.22, 3.17) * mm, "end": v(15.22, 0) * mm});
            skLineSegment(sketch, "E193.0.1", {"start": v(15.22, 0) * mm, "end": v(17.18, 0) * mm});
            skLineSegment(sketch, "E193.0.2", {"start": v(17.18, 0) * mm, "end": v(17.18, 3.17) * mm});
            skLineSegment(sketch, "E193.0.3", {"start": v(17.18, 3.18) * mm, "end": v(15.22, 3.18) * mm});
            skLineSegment(sketch, "E194.0.0", {"start": v(8.22, 3.17) * mm, "end": v(8.22, 0) * mm});
            skLineSegment(sketch, "E194.0.1", {"start": v(8.22, 0) * mm, "end": v(10.18, 0) * mm});
            skLineSegment(sketch, "E194.0.2", {"start": v(10.18, 0) * mm, "end": v(10.18, 3.17) * mm});
            skLineSegment(sketch, "E194.0.3", {"start": v(10.18, 3.18) * mm, "end": v(8.22, 3.18) * mm});
            skLineSegment(sketch, "E195.0.0", {"start": v(0, 3.17) * mm, "end": v(0, -47.62) * mm});
            skLineSegment(sketch, "E195.0.1", {"start": v(0, -47.63) * mm, "end": v(25.4, -47.63) * mm});
            skLineSegment(sketch, "E195.0.2", {"start": v(25.4, -47.62) * mm, "end": v(25.4, 3.17) * mm});
            skLineSegment(sketch, "E195.0.3", {"start": v(25.4, 3.18) * mm, "end": v(0, 3.18) * mm});
            skLineSegment(sketch, "E196.0.0", {"start": v(3.18, 0) * mm, "end": v(3.18, 3.17) * mm});
            skLineSegment(sketch, "E196.0.1", {"start": v(3.18, 3.18) * mm, "end": v(0, 3.18) * mm});
            skLineSegment(sketch, "E196.0.2", {"start": v(0, 3.18) * mm, "end": v(0, 0) * mm});
            skLineSegment(sketch, "E196.0.3", {"start": v(0, 0) * mm, "end": v(3.18, 0) * mm});
            skSolve(sketch);
        }
        {
            var Q0;
            Q0=makeQuery(id+"F36.imprint","IMPRINT",FACE,{"disambiguationData":[TD([[makeQuery(id+"F36.imprint","IMPRINT",EDGE,{"derivedFrom":sQuery(id+"F36.wireOp",EDGE,"E196.0.0")}),1.0]])]});
            var Q1;
            {var subQ0=sQuery(id+"F36.wireOp",EDGE,"E194.0.0");Q1=makeQuery(id+"F36.imprint","IMPRINT",FACE,{"disambiguationData":[TD([[makeQuery(id+"F36.imprint","IMPRINT",EDGE,{"derivedFrom":subQ0}),1.0]])]});}
            var Q2;
            {var subQ0=sQuery(id+"F36.wireOp",EDGE,"E193.0.0");Q2=makeQuery(id+"F36.imprint","IMPRINT",FACE,{"disambiguationData":[TD([[makeQuery(id+"F36.imprint","IMPRINT",EDGE,{"derivedFrom":subQ0}),1.0]])]});}
            var Q3;
            {var subQ0=sQuery(id+"F36.wireOp",EDGE,"E192.0.0");Q3=makeQuery(id+"F36.imprint","IMPRINT",FACE,{"disambiguationData":[TD([[makeQuery(id+"F36.imprint","IMPRINT",EDGE,{"derivedFrom":subQ0}),1.0]])]});}
            extrude(context, id + "F37", {"entities" : qUnion([Q0, Q1, Q2, Q3]), "operationType" : NewBodyOperationType.REMOVE, "oppositeDirection" : true, "depth" : 25.4 * mm, "offsetDistance" : 25.4 * mm});
        }
        {
            var Q0;
            Q0=makeQuery(id+"F9.opExtrude","SWEPT_FACE",FACE,{"disambiguationData":[OSD([sQuery(id+"F0.wireOp",EDGE,"E3")])]});
            var sketch = newSketch(context, id + "F38", { "sketchPlane" : qUnion([Q0])});
            skLineSegment(sketch, "E197.0.0", {"start": v(12.47, 3.17) * mm, "end": v(12.47, 0) * mm});
            skLineSegment(sketch, "E197.0.1", {"start": v(12.47, 0) * mm, "end": v(15.65, 0) * mm});
            skLineSegment(sketch, "E197.0.2", {"start": v(15.65, 0) * mm, "end": v(15.65, 3.18) * mm});
            skLineSegment(sketch, "E197.0.3", {"start": v(15.65, 3.18) * mm, "end": v(12.47, 3.18) * mm});
            skLineSegment(sketch, "E198.0.0", {"start": v(1.53, 3.17) * mm, "end": v(1.53, 0) * mm});
            skLineSegment(sketch, "E198.0.1", {"start": v(1.53, 0) * mm, "end": v(8.96, 0) * mm});
            skLineSegment(sketch, "E198.0.2", {"start": v(8.96, 0) * mm, "end": v(8.96, 3.17) * mm});
            skLineSegment(sketch, "E198.0.3", {"start": v(8.96, 3.18) * mm, "end": v(1.53, 3.18) * mm});
            skLineSegment(sketch, "E199.0.0", {"start": v(-9.42, 3.17) * mm, "end": v(-9.42, 0) * mm});
            skLineSegment(sketch, "E199.0.1", {"start": v(-9.42, 0) * mm, "end": v(-1.98, 0) * mm});
            skLineSegment(sketch, "E199.0.2", {"start": v(-1.98, 0) * mm, "end": v(-1.98, 3.17) * mm});
            skLineSegment(sketch, "E199.0.3", {"start": v(-1.98, 3.18) * mm, "end": v(-9.42, 3.18) * mm});
            skLineSegment(sketch, "E200.0.0", {"start": v(-12.93, 0) * mm, "end": v(-12.93, 3.17) * mm});
            skLineSegment(sketch, "E200.0.1", {"start": v(-12.93, 3.18) * mm, "end": v(-16.1, 3.18) * mm});
            skLineSegment(sketch, "E200.0.2", {"start": v(-16.1, 3.18) * mm, "end": v(-16.1, 0) * mm});
            skLineSegment(sketch, "E200.0.3", {"start": v(-16.1, 0) * mm, "end": v(-12.93, 0) * mm});
            skSolve(sketch);
        }
        {
            var Q0;
            {var subQ3=sQuery(id+"F38.wireOp",EDGE,"E197.0.0");Q0=makeQuery(id+"F38.imprint","IMPRINT",FACE,{"disambiguationData":[TD([[makeQuery(id+"F38.imprint","IMPRINT",EDGE,{"derivedFrom":subQ3}),-1.0]])]});}
            var sketch = newSketch(context, id + "F39", { "sketchPlane" : qUnion([Q0])});
            skLineSegment(sketch, "E201.0.0", {"start": v(12.47, 3.18) * mm, "end": v(12.47, 0) * mm});
            skLineSegment(sketch, "E201.0.1", {"start": v(12.47, 0) * mm, "end": v(15.65, 0) * mm});
            skLineSegment(sketch, "E201.0.2", {"start": v(15.65, 0) * mm, "end": v(15.65, 3.17) * mm});
            skLineSegment(sketch, "E201.0.3", {"start": v(15.65, 3.18) * mm, "end": v(12.47, 3.18) * mm});
            skLineSegment(sketch, "E202.0.0", {"start": v(1.53, 0) * mm, "end": v(8.96, 0) * mm});
            skLineSegment(sketch, "E202.0.1", {"start": v(8.96, 0) * mm, "end": v(8.96, 3.18) * mm});
            skLineSegment(sketch, "E202.0.2", {"start": v(8.96, 3.18) * mm, "end": v(1.53, 3.18) * mm});
            skLineSegment(sketch, "E202.0.3", {"start": v(1.53, 3.18) * mm, "end": v(1.53, 0) * mm});
            skLineSegment(sketch, "E203.0.0", {"start": v(-9.42, 0) * mm, "end": v(-1.98, 0) * mm});
            skLineSegment(sketch, "E203.0.1", {"start": v(-1.98, 0) * mm, "end": v(-1.98, 3.18) * mm});
            skLineSegment(sketch, "E203.0.2", {"start": v(-1.98, 3.18) * mm, "end": v(-9.42, 3.18) * mm});
            skLineSegment(sketch, "E203.0.3", {"start": v(-9.42, 3.18) * mm, "end": v(-9.42, 0) * mm});
            skLineSegment(sketch, "E204.0.0", {"start": v(-16.1, 3.17) * mm, "end": v(-16.1, 0) * mm});
            skLineSegment(sketch, "E204.0.1", {"start": v(-16.1, 0) * mm, "end": v(-12.93, 0) * mm});
            skLineSegment(sketch, "E204.0.2", {"start": v(-12.93, 0) * mm, "end": v(-12.93, 3.18) * mm});
            skLineSegment(sketch, "E204.0.3", {"start": v(-12.93, 3.18) * mm, "end": v(-16.1, 3.18) * mm});
            skSolve(sketch);
        }
        {
            var Q0;
            Q0=qSketchRegion(id+"F39",true);
            extrude(context, id + "F40", {"entities" : qUnion([Q0]), "operationType" : NewBodyOperationType.REMOVE, "oppositeDirection" : true, "depth" : 25.4 * mm, "offsetDistance" : 25.4 * mm});
        }
        {
            var Q0;
            Q0=makeQuery(id+"F10.opExtrude","SWEPT_FACE",FACE,{"disambiguationData":[OSD([sQuery(id+"F0.wireOp",EDGE,"E4")])]});
            var sketch = newSketch(context, id + "F41", { "sketchPlane" : qUnion([Q0])});
            skLineSegment(sketch, "E205.0.0", {"start": v(-25.4, 3.17) * mm, "end": v(-25.4, 0) * mm});
            skLineSegment(sketch, "E205.0.1", {"start": v(-25.4, 0) * mm, "end": v(-22.23, 0) * mm});
            skLineSegment(sketch, "E205.0.2", {"start": v(-22.23, 0) * mm, "end": v(-22.23, 3.18) * mm});
            skLineSegment(sketch, "E205.0.3", {"start": v(-22.23, 3.18) * mm, "end": v(-25.4, 3.18) * mm});
            skLineSegment(sketch, "E206.0.0", {"start": v(-38.1, 3.17) * mm, "end": v(-38.1, 0) * mm});
            skLineSegment(sketch, "E206.0.1", {"start": v(-38.1, 0) * mm, "end": v(-31.75, 0) * mm});
            skLineSegment(sketch, "E206.0.2", {"start": v(-31.75, 0) * mm, "end": v(-31.75, 3.17) * mm});
            skLineSegment(sketch, "E206.0.3", {"start": v(-31.75, 3.18) * mm, "end": v(-38.1, 3.18) * mm});
            skLineSegment(sketch, "E207.0.0", {"start": v(-50.8, 3.17) * mm, "end": v(-50.8, 0) * mm});
            skLineSegment(sketch, "E207.0.1", {"start": v(-50.8, 0) * mm, "end": v(-44.45, 0) * mm});
            skLineSegment(sketch, "E207.0.2", {"start": v(-44.45, 0) * mm, "end": v(-44.45, 3.17) * mm});
            skLineSegment(sketch, "E207.0.3", {"start": v(-44.45, 3.18) * mm, "end": v(-50.8, 3.18) * mm});
            skLineSegment(sketch, "E208.0.0", {"start": v(-57.15, 0) * mm, "end": v(-57.15, 3.17) * mm});
            skLineSegment(sketch, "E208.0.1", {"start": v(-57.15, 3.18) * mm, "end": v(-60.32, 3.18) * mm});
            skLineSegment(sketch, "E208.0.2", {"start": v(-60.33, 3.18) * mm, "end": v(-60.33, 0) * mm});
            skLineSegment(sketch, "E208.0.3", {"start": v(-60.32, 0) * mm, "end": v(-57.15, 0) * mm});
            skSolve(sketch);
        }
        {
            var Q0;
            Q0=qSketchRegion(id+"F41",true);
            extrude(context, id + "F42", {"entities" : qUnion([Q0]), "operationType" : NewBodyOperationType.REMOVE, "oppositeDirection" : true, "depth" : 25.4 * mm, "offsetDistance" : 25.4 * mm});
        }
        {
            var Q0;
            Q0=makeQuery(id+"F11.opExtrude","SWEPT_FACE",FACE,{"disambiguationData":[OSD([sQuery(id+"F0.wireOp",EDGE,"E5"),sQuery(id+"F2.wireOp",EDGE,"E45")])]});
            var sketch = newSketch(context, id + "F43", { "sketchPlane" : qUnion([Q0])});
            skLineSegment(sketch, "E209.0.0", {"start": v(-22.83, 3.17) * mm, "end": v(-22.83, 0) * mm});
            skLineSegment(sketch, "E209.0.1", {"start": v(-22.83, 0) * mm, "end": v(-19.66, 0) * mm});
            skLineSegment(sketch, "E209.0.2", {"start": v(-19.66, 0) * mm, "end": v(-19.66, 3.18) * mm});
            skLineSegment(sketch, "E209.0.3", {"start": v(-19.66, 3.18) * mm, "end": v(-22.83, 3.18) * mm});
            skLineSegment(sketch, "E210.0.0", {"start": v(-30.77, 3.17) * mm, "end": v(-30.77, 0) * mm});
            skLineSegment(sketch, "E210.0.1", {"start": v(-30.77, 0) * mm, "end": v(-26, 0) * mm});
            skLineSegment(sketch, "E210.0.2", {"start": v(-26, 0) * mm, "end": v(-26, 3.17) * mm});
            skLineSegment(sketch, "E210.0.3", {"start": v(-26, 3.18) * mm, "end": v(-30.77, 3.18) * mm});
            skLineSegment(sketch, "E211.0.0", {"start": v(-38.7, 3.17) * mm, "end": v(-38.7, 0) * mm});
            skLineSegment(sketch, "E211.0.1", {"start": v(-38.7, 0) * mm, "end": v(-33.94, 0) * mm});
            skLineSegment(sketch, "E211.0.2", {"start": v(-33.94, 0) * mm, "end": v(-33.94, 3.17) * mm});
            skLineSegment(sketch, "E211.0.3", {"start": v(-33.94, 3.18) * mm, "end": v(-38.7, 3.18) * mm});
            skLineSegment(sketch, "E212.0.0", {"start": v(-41.88, 0) * mm, "end": v(-41.88, 3.17) * mm});
            skLineSegment(sketch, "E212.0.1", {"start": v(-41.88, 3.18) * mm, "end": v(-45.06, 3.18) * mm});
            skLineSegment(sketch, "E212.0.2", {"start": v(-45.06, 3.18) * mm, "end": v(-45.06, 0) * mm});
            skLineSegment(sketch, "E212.0.3", {"start": v(-45.06, 0) * mm, "end": v(-41.88, 0) * mm});
            skSolve(sketch);
        }
        {
            var Q0;
            Q0=qSketchRegion(id+"F43",true);
            extrude(context, id + "F44", {"entities" : qUnion([Q0]), "operationType" : NewBodyOperationType.REMOVE, "oppositeDirection" : true, "depth" : 25.4 * mm, "offsetDistance" : 25.4 * mm});
        }
        {
            var Q0;
            Q0=makeQuery(id+"F12.opExtrude","SWEPT_FACE",FACE,{"disambiguationData":[OSD([sQuery(id+"F0.wireOp",EDGE,"E6"),sQuery(id+"F2.wireOp",EDGE,"E40")])]});
            var sketch = newSketch(context, id + "F45", { "sketchPlane" : qUnion([Q0])});
            skLineSegment(sketch, "E213.0.0", {"start": v(41.88, 3.17) * mm, "end": v(41.88, 0) * mm});
            skLineSegment(sketch, "E213.0.1", {"start": v(41.88, 0) * mm, "end": v(45.06, 0) * mm});
            skLineSegment(sketch, "E213.0.2", {"start": v(45.06, 0) * mm, "end": v(45.06, 3.18) * mm});
            skLineSegment(sketch, "E213.0.3", {"start": v(45.06, 3.18) * mm, "end": v(41.88, 3.18) * mm});
            skLineSegment(sketch, "E214.0.0", {"start": v(33.94, 0) * mm, "end": v(38.7, 0) * mm});
            skLineSegment(sketch, "E214.0.1", {"start": v(38.7, 0) * mm, "end": v(38.7, 3.17) * mm});
            skLineSegment(sketch, "E214.0.2", {"start": v(38.7, 3.18) * mm, "end": v(33.94, 3.18) * mm});
            skLineSegment(sketch, "E214.0.3", {"start": v(33.94, 3.17) * mm, "end": v(33.94, 0) * mm});
            skLineSegment(sketch, "E215.0.0", {"start": v(26, 0) * mm, "end": v(30.77, 0) * mm});
            skLineSegment(sketch, "E215.0.1", {"start": v(30.77, 0) * mm, "end": v(30.77, 3.17) * mm});
            skLineSegment(sketch, "E215.0.2", {"start": v(30.77, 3.18) * mm, "end": v(26, 3.18) * mm});
            skLineSegment(sketch, "E215.0.3", {"start": v(26, 3.17) * mm, "end": v(26, 0) * mm});
            skLineSegment(sketch, "E216.0.0", {"start": v(19.66, 0) * mm, "end": v(22.83, 0) * mm});
            skLineSegment(sketch, "E216.0.1", {"start": v(22.83, 0) * mm, "end": v(22.83, 3.17) * mm});
            skLineSegment(sketch, "E216.0.2", {"start": v(22.83, 3.18) * mm, "end": v(19.66, 3.18) * mm});
            skLineSegment(sketch, "E216.0.3", {"start": v(19.66, 3.18) * mm, "end": v(19.66, 0) * mm});
            skSolve(sketch);
        }
        {
            var Q0;
            Q0=qSketchRegion(id+"F45",true);
            extrude(context, id + "F46", {"entities" : qUnion([Q0]), "operationType" : NewBodyOperationType.REMOVE, "oppositeDirection" : true, "depth" : 25.4 * mm, "offsetDistance" : 25.4 * mm});
        }
        {
            var Q0;
            Q0=makeQuery(id+"F6.opExtrude","CAP_FACE",FACE,{"disambiguationData":[OSD([sQuery(id+"F0.wireOp",EDGE,"E0"),sQuery(id+"F0.wireOp",EDGE,"E1"),sQuery(id+"F2.wireOp",EDGE,"E13"),sQuery(id+"F2.wireOp",EDGE,"E14")])],"isStart":false});
            var sketch = newSketch(context, id + "F47", { "sketchPlane" : qUnion([Q0])});
            skLineSegment(sketch, "E217", {"start": v(0, 73.01) * mm, "end": v(-2.26, 75.24) * mm});
            skLineSegment(sketch, "E218.0", {"start": v(-73.94, -2.23) * mm, "end": v(2.23, 75.28) * mm});
            skLineSegment(sketch, "E219.0", {"start": v(-2.23, 75.28) * mm, "end": v(73.94, -2.23) * mm});
            skSolve(sketch);
        }
        {
            var Q0;
            Q0=makeQuery(id+"F6.opExtrude","SWEPT_FACE",FACE,{"disambiguationData":[OSD([sQuery(id+"F0.wireOp",EDGE,"E0")])]});
            var sketch = newSketch(context, id + "F48", { "sketchPlane" : qUnion([Q0])});
            skLineSegment(sketch, "E220.bottom", {"start": v(55.3, -40.48) * mm, "end": v(52.08, -40.48) * mm});
            skLineSegment(sketch, "E220.top", {"start": v(55.3, -34.13) * mm, "end": v(52.08, -34.13) * mm});
            skLineSegment(sketch, "E220.left", {"start": v(55.3, -40.48) * mm, "end": v(55.3, -34.13) * mm});
            skLineSegment(sketch, "E220.right", {"start": v(52.08, -40.48) * mm, "end": v(52.08, -34.13) * mm});
            skLineSegment(sketch, "E221.bottom", {"start": v(55.3, -26.99) * mm, "end": v(52.08, -26.99) * mm});
            skLineSegment(sketch, "E221.top", {"start": v(55.3, -20.64) * mm, "end": v(52.08, -20.64) * mm});
            skLineSegment(sketch, "E221.left", {"start": v(55.3, -26.99) * mm, "end": v(55.3, -20.64) * mm});
            skLineSegment(sketch, "E221.right", {"start": v(52.08, -26.99) * mm, "end": v(52.08, -20.64) * mm});
            skLineSegment(sketch, "E222.bottom", {"start": v(55.3, -13.5) * mm, "end": v(52.08, -13.5) * mm});
            skLineSegment(sketch, "E222.top", {"start": v(55.3, -7.14) * mm, "end": v(52.08, -7.14) * mm});
            skLineSegment(sketch, "E222.left", {"start": v(55.3, -13.5) * mm, "end": v(55.3, -7.14) * mm});
            skLineSegment(sketch, "E222.right", {"start": v(52.08, -13.5) * mm, "end": v(52.08, -7.14) * mm});
            skLineSegment(sketch, "E223", {"start": v(53.7, -34.13) * mm, "end": v(53.7, -26.99) * mm, "construction": true});
            skLineSegment(sketch, "E224", {"start": v(53.7, -20.64) * mm, "end": v(53.7, -13.5) * mm, "construction": true});
            skLineSegment(sketch, "E225", {"start": v(53.7, -7.14) * mm, "end": v(53.7, 0) * mm, "construction": true});
            skLineSegment(sketch, "E226", {"start": v(53.7, -47.63) * mm, "end": v(53.7, -40.48) * mm, "construction": true});
            skSolve(sketch);
        }
        {
            var Q0;
            Q0=makeQuery(id+"F48.imprint","IMPRINT",FACE,{"disambiguationData":[TD([[makeQuery(id+"F48.imprint","IMPRINT",EDGE,{"derivedFrom":sQuery(id+"F48.wireOp",EDGE,"E220.bottom")}),-1.0]])]});
            var Q1;
            Q1=makeQuery(id+"F48.imprint","IMPRINT",FACE,{"disambiguationData":[TD([[makeQuery(id+"F48.imprint","IMPRINT",EDGE,{"derivedFrom":sQuery(id+"F48.wireOp",EDGE,"E221.bottom")}),-1.0]])]});
            var Q2;
            Q2=makeQuery(id+"F48.imprint","IMPRINT",FACE,{"disambiguationData":[TD([[makeQuery(id+"F48.imprint","IMPRINT",EDGE,{"derivedFrom":sQuery(id+"F48.wireOp",EDGE,"E222.bottom")}),-1.0]])]});
            extrude(context, id + "F49", {"entities" : qUnion([Q0, Q1, Q2]), "operationType" : NewBodyOperationType.REMOVE, "oppositeDirection" : true, "depth" : 25.4 * mm, "offsetDistance" : 25.4 * mm});
        }
        {
            var Q0;
            Q0=makeQuery(id+"F7.opExtrude","CAP_FACE",FACE,{"disambiguationData":[OSD([sQuery(id+"F0.wireOp",EDGE,"E0"),sQuery(id+"F0.wireOp",EDGE,"E1"),sQuery(id+"F2.wireOp",EDGE,"E35"),sQuery(id+"F2.wireOp",EDGE,"E36")])],"isStart":false});
            var sketch = newSketch(context, id + "F50", { "sketchPlane" : qUnion([Q0])});
            skLineSegment(sketch, "E227.0.0", {"start": v(76.2, 0) * mm, "end": v(0, 77.54) * mm});
            skLineSegment(sketch, "E227.0.1", {"start": v(0, 77.54) * mm, "end": v(-2.23, 75.28) * mm});
            skLineSegment(sketch, "E227.0.2", {"start": v(-2.23, 75.28) * mm, "end": v(73.94, -2.23) * mm});
            skLineSegment(sketch, "E227.0.3", {"start": v(73.94, -2.23) * mm, "end": v(76.2, 0) * mm});
            skLineSegment(sketch, "E228.0.0", {"start": v(0, 77.54) * mm, "end": v(-76.2, 0) * mm});
            skLineSegment(sketch, "E228.0.1", {"start": v(-76.2, 0) * mm, "end": v(-73.94, -2.23) * mm});
            skLineSegment(sketch, "E228.0.2", {"start": v(-73.94, -2.23) * mm, "end": v(2.23, 75.28) * mm});
            skLineSegment(sketch, "E228.0.3", {"start": v(2.23, 75.28) * mm, "end": v(0, 77.54) * mm});
            skLineSegment(sketch, "E229", {"start": v(0, 73.01) * mm, "end": v(2.26, 75.24) * mm});
            skSolve(sketch);
        }
        {
            var Q0;
            Q0=makeQuery(id+"F7.opExtrude","SWEPT_FACE",FACE,{"disambiguationData":[OSD([sQuery(id+"F0.wireOp",EDGE,"E1")])]});
            var sketch = newSketch(context, id + "F51", { "sketchPlane" : qUnion([Q0])});
            skLineSegment(sketch, "E230.0.0", {"start": v(-52.13, -47.62) * mm, "end": v(-52.13, -40.48) * mm});
            skLineSegment(sketch, "E230.0.1", {"start": v(-52.08, -40.48) * mm, "end": v(-55.3, -40.48) * mm});
            skLineSegment(sketch, "E230.0.2", {"start": v(-55.3, -40.48) * mm, "end": v(-55.3, -47.62) * mm});
            skLineSegment(sketch, "E230.0.3", {"start": v(-55.3, -47.63) * mm, "end": v(-52.08, -47.63) * mm});
            skLineSegment(sketch, "E231.0.0", {"start": v(-55.3, -34.13) * mm, "end": v(-52.08, -34.13) * mm});
            skLineSegment(sketch, "E231.0.1", {"start": v(-52.13, -34.13) * mm, "end": v(-52.13, -26.99) * mm});
            skLineSegment(sketch, "E231.0.2", {"start": v(-52.08, -26.99) * mm, "end": v(-55.3, -26.99) * mm});
            skLineSegment(sketch, "E231.0.3", {"start": v(-55.3, -26.99) * mm, "end": v(-55.3, -34.13) * mm});
            skLineSegment(sketch, "E232.0.0", {"start": v(-55.3, -20.64) * mm, "end": v(-52.08, -20.64) * mm});
            skLineSegment(sketch, "E232.0.1", {"start": v(-52.13, -20.64) * mm, "end": v(-52.13, -13.5) * mm});
            skLineSegment(sketch, "E232.0.2", {"start": v(-52.08, -13.5) * mm, "end": v(-55.3, -13.5) * mm});
            skLineSegment(sketch, "E232.0.3", {"start": v(-55.3, -13.5) * mm, "end": v(-55.3, -20.64) * mm});
            skLineSegment(sketch, "E233.0.0", {"start": v(-55.3, -7.14) * mm, "end": v(-52.08, -7.14) * mm});
            skLineSegment(sketch, "E233.0.1", {"start": v(-52.13, -7.14) * mm, "end": v(-52.13, 0) * mm});
            skLineSegment(sketch, "E233.0.2", {"start": v(-52.08, 0) * mm, "end": v(-55.3, 0) * mm});
            skLineSegment(sketch, "E233.0.3", {"start": v(-55.3, 0) * mm, "end": v(-55.3, -7.14) * mm});
            skPoint(sketch, "E234.0", {"position": v(-52.08, -47.62) * mm});
            skLineSegment(sketch, "E235", {"start": v(-52.08, -47.62) * mm, "end": v(-52.08, 0) * mm});
            skSolve(sketch);
        }
        {
            var Q0;
            {var subQ2=sQuery(id+"F51.wireOp",EDGE,"E233.0.1");Q0=makeQuery(id+"F51.imprint","IMPRINT",FACE,{"disambiguationData":[TD([[makeQuery(id+"F51.imprint","IMPRINT",EDGE,{"derivedFrom":subQ2}),1.0]])]});}
            var Q1;
            {var subQ3=sQuery(id+"F51.wireOp",EDGE,"E233.0.1");Q1=makeQuery(id+"F51.imprint","IMPRINT",FACE,{"disambiguationData":[TD([[makeQuery(id+"F51.imprint","IMPRINT",EDGE,{"derivedFrom":subQ3}),-1.0]])]});}
            var Q2;
            {var subQ3=sQuery(id+"F51.wireOp",EDGE,"E232.0.1");Q2=makeQuery(id+"F51.imprint","IMPRINT",FACE,{"disambiguationData":[TD([[makeQuery(id+"F51.imprint","IMPRINT",EDGE,{"derivedFrom":subQ3}),1.0]])]});}
            var Q3;
            {var subQ3=sQuery(id+"F51.wireOp",EDGE,"E232.0.1");Q3=makeQuery(id+"F51.imprint","IMPRINT",FACE,{"disambiguationData":[TD([[makeQuery(id+"F51.imprint","IMPRINT",EDGE,{"derivedFrom":subQ3}),-1.0]])]});}
            var Q4;
            {var subQ3=sQuery(id+"F51.wireOp",EDGE,"E231.0.1");Q4=makeQuery(id+"F51.imprint","IMPRINT",FACE,{"disambiguationData":[TD([[makeQuery(id+"F51.imprint","IMPRINT",EDGE,{"derivedFrom":subQ3}),1.0]])]});}
            var Q5;
            {var subQ3=sQuery(id+"F51.wireOp",EDGE,"E231.0.1");Q5=makeQuery(id+"F51.imprint","IMPRINT",FACE,{"disambiguationData":[TD([[makeQuery(id+"F51.imprint","IMPRINT",EDGE,{"derivedFrom":subQ3}),-1.0]])]});}
            var Q6;
            {var subQ0=sQuery(id+"F51.wireOp",EDGE,"E230.0.0");Q6=makeQuery(id+"F51.imprint","IMPRINT",FACE,{"disambiguationData":[TD([[makeQuery(id+"F51.imprint","IMPRINT",EDGE,{"derivedFrom":subQ0}),1.0]])]});}
            var Q7;
            {var subQ0=sQuery(id+"F51.wireOp",EDGE,"E230.0.0");Q7=makeQuery(id+"F51.imprint","IMPRINT",FACE,{"disambiguationData":[TD([[makeQuery(id+"F51.imprint","IMPRINT",EDGE,{"derivedFrom":subQ0}),-1.0]])]});}
            extrude(context, id + "F52", {"entities" : qUnion([Q0, Q1, Q2, Q3, Q4, Q5, Q6, Q7]), "operationType" : NewBodyOperationType.REMOVE, "oppositeDirection" : true, "depth" : 25.4 * mm, "offsetDistance" : 25.4 * mm});
        }
        {
            var Q0;
            {var subQ0=sQuery(id+"F50.wireOp",EDGE,"E227.0.3");Q0=makeQuery(id+"F50.imprint","IMPRINT",FACE,{"disambiguationData":[TD([[makeQuery(id+"F50.imprint","IMPRINT",EDGE,{"derivedFrom":subQ0}),1.0]])]});}
            var sketch = newSketch(context, id + "F53", { "sketchPlane" : qUnion([Q0])});
            skLineSegment(sketch, "E236.0.0", {"start": v(73.03, -25.4) * mm, "end": v(76.2, -25.4) * mm});
            skLineSegment(sketch, "E236.0.1", {"start": v(76.2, -25.4) * mm, "end": v(76.2, 0) * mm});
            skLineSegment(sketch, "E236.0.2", {"start": v(76.2, 0) * mm, "end": v(73.03, 0) * mm});
            skLineSegment(sketch, "E236.0.3", {"start": v(73.03, 0) * mm, "end": v(73.03, -25.4) * mm});
            skLineSegment(sketch, "E237.0.0", {"start": v(2.26, 75.24) * mm, "end": v(0, 73.01) * mm});
            skLineSegment(sketch, "E237.0.1", {"start": v(0, 73.01) * mm, "end": v(73.94, -2.23) * mm});
            skLineSegment(sketch, "E237.0.2", {"start": v(73.94, -2.23) * mm, "end": v(76.2, 0) * mm});
            skLineSegment(sketch, "E237.0.3", {"start": v(76.2, 0) * mm, "end": v(2.26, 75.24) * mm});
            skLineSegment(sketch, "E238", {"start": v(72.38, -0.64) * mm, "end": v(74.64, 1.59) * mm});
            skSolve(sketch);
        }
        {
            var Q0;
            Q0=makeQuery(id+"F7.opExtrude","SWEPT_FACE",FACE,{"disambiguationData":[OSD([sQuery(id+"F0.wireOp",EDGE,"E1")])]});
            var sketch = newSketch(context, id + "F54", { "sketchPlane" : qUnion([Q0])});
            skLineSegment(sketch, "E239.0", {"start": v(53.4, -40.48) * mm, "end": v(-55.3, -40.48) * mm});
            skLineSegment(sketch, "E240.0", {"start": v(53.4, -34.13) * mm, "end": v(-55.3, -34.13) * mm});
            skLineSegment(sketch, "E241.0", {"start": v(53.4, -26.99) * mm, "end": v(-55.3, -26.99) * mm});
            skLineSegment(sketch, "E242.0.0", {"start": v(-55.3, -34.13) * mm, "end": v(-52.13, -34.13) * mm});
            skLineSegment(sketch, "E242.0.1", {"start": v(-52.13, -34.13) * mm, "end": v(-52.13, -26.99) * mm});
            skLineSegment(sketch, "E242.0.2", {"start": v(-52.13, -26.99) * mm, "end": v(-55.3, -26.99) * mm});
            skLineSegment(sketch, "E242.0.3", {"start": v(-55.3, -26.99) * mm, "end": v(-55.3, -34.13) * mm});
            skLineSegment(sketch, "E243.0.0", {"start": v(-52.13, -47.62) * mm, "end": v(-52.13, -40.48) * mm});
            skLineSegment(sketch, "E243.0.1", {"start": v(-52.13, -40.48) * mm, "end": v(-55.3, -40.48) * mm});
            skLineSegment(sketch, "E243.0.2", {"start": v(-55.3, -40.48) * mm, "end": v(-55.3, -47.62) * mm});
            skLineSegment(sketch, "E243.0.3", {"start": v(-55.3, -47.63) * mm, "end": v(53.4, -47.63) * mm});
            skLineSegment(sketch, "E244.0.0", {"start": v(-55.3, -20.64) * mm, "end": v(53.4, -20.64) * mm});
            skLineSegment(sketch, "E244.0.1", {"start": v(-52.13, -20.64) * mm, "end": v(-52.13, -13.5) * mm});
            skLineSegment(sketch, "E244.0.2", {"start": v(53.4, -13.5) * mm, "end": v(-55.3, -13.5) * mm});
            skLineSegment(sketch, "E244.0.3", {"start": v(-55.3, -13.5) * mm, "end": v(-55.3, -20.64) * mm});
            skLineSegment(sketch, "E245.0.0", {"start": v(-55.3, -7.14) * mm, "end": v(53.4, -7.14) * mm});
            skLineSegment(sketch, "E245.0.1", {"start": v(-52.13, -7.14) * mm, "end": v(-52.13, 0) * mm});
            skLineSegment(sketch, "E245.0.2", {"start": v(53.4, 0) * mm, "end": v(-55.3, 0) * mm});
            skLineSegment(sketch, "E245.0.3", {"start": v(-55.3, 0) * mm, "end": v(-55.3, -7.14) * mm});
            skLineSegment(sketch, "E246.0", {"start": v(53.4, -47.62) * mm, "end": v(53.4, 0) * mm});
            skPoint(sketch, "E247.0", {"position": v(51.18, -47.62) * mm});
            skLineSegment(sketch, "E248", {"start": v(51.18, -47.62) * mm, "end": v(51.18, 0) * mm});
            skSolve(sketch);
        }
        {
            var Q0;
            {var subQ0=sQuery(id+"F54.wireOp",EDGE,"E246.0");var subQ1=sQuery(id+"F54.wireOp",EDGE,"E239.0");var subQ2=makeQuery(id+"F54.imprint","INTERSECT",VERTEX,{"derivedFrom":[subQ1,subQ0]});Q0=makeQuery(id+"F54.imprint","IMPRINT",FACE,{"disambiguationData":[TD([[makeQuery(id+"F54.imprint","IMPRINT",EDGE,{"disambiguationData":[TD([[subQ2,-1.0]])],"derivedFrom":subQ1}),-1.0]])]});}
            var Q1;
            {var subQ0=sQuery(id+"F54.wireOp",EDGE,"E246.0");var subQ1=sQuery(id+"F54.wireOp",EDGE,"E241.0");var subQ2=makeQuery(id+"F54.imprint","INTERSECT",VERTEX,{"derivedFrom":[subQ1,subQ0]});Q1=makeQuery(id+"F54.imprint","IMPRINT",FACE,{"disambiguationData":[TD([[makeQuery(id+"F54.imprint","IMPRINT",EDGE,{"disambiguationData":[TD([[subQ2,-1.0]])],"derivedFrom":subQ1}),-1.0]])]});}
            var Q2;
            {var subQ0=sQuery(id+"F54.wireOp",EDGE,"E246.0");var subQ1=sQuery(id+"F54.wireOp",EDGE,"E244.0.2");var subQ2=makeQuery(id+"F54.imprint","INTERSECT",VERTEX,{"derivedFrom":[subQ1,subQ0]});Q2=makeQuery(id+"F54.imprint","IMPRINT",FACE,{"disambiguationData":[TD([[makeQuery(id+"F54.imprint","IMPRINT",EDGE,{"disambiguationData":[TD([[subQ2,-1.0]])],"derivedFrom":subQ1}),-1.0]])]});}
            extrude(context, id + "F55", {"entities" : qUnion([Q0, Q1, Q2]), "operationType" : NewBodyOperationType.REMOVE, "oppositeDirection" : true, "depth" : 25.4 * mm, "offsetDistance" : 25.4 * mm});
        }
        {
            var Q0;
            {var subQ4=sQuery(id+"F53.wireOp",EDGE,"E236.0.0");Q0=makeQuery(id+"F53.imprint","IMPRINT",FACE,{"disambiguationData":[TD([[makeQuery(id+"F53.imprint","IMPRINT",EDGE,{"derivedFrom":subQ4}),1.0]])]});}
            var sketch = newSketch(context, id + "F56", { "sketchPlane" : qUnion([Q0])});
            skLineSegment(sketch, "E249.0.0", {"start": v(73.94, -2.23) * mm, "end": v(73.03, -1.3) * mm});
            skLineSegment(sketch, "E249.0.1", {"start": v(73.03, -1.3) * mm, "end": v(73.03, -25.4) * mm});
            skLineSegment(sketch, "E249.0.2", {"start": v(73.03, -25.4) * mm, "end": v(76.2, -25.4) * mm});
            skLineSegment(sketch, "E249.0.3", {"start": v(76.2, -25.4) * mm, "end": v(76.2, 0) * mm});
            skLineSegment(sketch, "E249.0.4", {"start": v(76.2, 0) * mm, "end": v(73.94, -2.23) * mm});
            skLineSegment(sketch, "E250.0.0", {"start": v(76.2, 0) * mm, "end": v(73.03, 0) * mm});
            skLineSegment(sketch, "E250.0.1", {"start": v(73.03, 0) * mm, "end": v(73.03, -1.3) * mm});
            skLineSegment(sketch, "E250.0.2", {"start": v(73.03, -1.3) * mm, "end": v(73.94, -2.23) * mm});
            skLineSegment(sketch, "E250.0.3", {"start": v(73.94, -2.23) * mm, "end": v(76.2, 0) * mm});
            skLineSegment(sketch, "E251", {"start": v(73.03, -2.23) * mm, "end": v(76.2, -2.23) * mm});
            skSolve(sketch);
        }
        {
            var Q0;
            Q0=makeQuery(id+"F8.opExtrude","SWEPT_FACE",FACE,{"disambiguationData":[OSD([sQuery(id+"F0.wireOp",EDGE,"E2")])]});
            var sketch = newSketch(context, id + "F57", { "sketchPlane" : qUnion([Q0])});
            skLineSegment(sketch, "E252.0.0", {"start": v(2.23, -47.62) * mm, "end": v(2.23, -40.48) * mm});
            skLineSegment(sketch, "E252.0.1", {"start": v(2.23, -40.48) * mm, "end": v(0, -40.48) * mm});
            skLineSegment(sketch, "E252.0.2", {"start": v(0, -40.48) * mm, "end": v(0, -47.62) * mm});
            skLineSegment(sketch, "E252.0.3", {"start": v(0, -47.63) * mm, "end": v(2.23, -47.63) * mm});
            skLineSegment(sketch, "E253.0.0", {"start": v(0, -34.13) * mm, "end": v(2.23, -34.13) * mm});
            skLineSegment(sketch, "E253.0.1", {"start": v(2.23, -34.13) * mm, "end": v(2.23, -26.99) * mm});
            skLineSegment(sketch, "E253.0.2", {"start": v(2.23, -26.99) * mm, "end": v(0, -26.99) * mm});
            skLineSegment(sketch, "E253.0.3", {"start": v(0, -26.99) * mm, "end": v(0, -34.13) * mm});
            skLineSegment(sketch, "E254.0.0", {"start": v(0, -20.64) * mm, "end": v(2.23, -20.64) * mm});
            skLineSegment(sketch, "E254.0.1", {"start": v(2.23, -20.64) * mm, "end": v(2.23, -13.5) * mm});
            skLineSegment(sketch, "E254.0.2", {"start": v(2.23, -13.5) * mm, "end": v(0, -13.5) * mm});
            skLineSegment(sketch, "E254.0.3", {"start": v(0, -13.5) * mm, "end": v(0, -20.64) * mm});
            skLineSegment(sketch, "E255.0.0", {"start": v(0, -7.14) * mm, "end": v(2.23, -7.14) * mm});
            skLineSegment(sketch, "E255.0.1", {"start": v(2.23, -7.14) * mm, "end": v(2.23, 0) * mm});
            skLineSegment(sketch, "E255.0.2", {"start": v(2.23, 0) * mm, "end": v(0, 0) * mm});
            skLineSegment(sketch, "E255.0.3", {"start": v(0, 0) * mm, "end": v(0, -7.14) * mm});
            skSolve(sketch);
        }
        {
            var Q0;
            Q0=qSketchRegion(id+"F57",true);
            extrude(context, id + "F58", {"entities" : qUnion([Q0]), "operationType" : NewBodyOperationType.REMOVE, "oppositeDirection" : true, "depth" : 25.4 * mm, "offsetDistance" : 25.4 * mm});
        }
        {
            var Q0;
            {var subQ5=sQuery(id+"F56.wireOp",EDGE,"E249.0.2");Q0=makeQuery(id+"F56.imprint","IMPRINT",FACE,{"disambiguationData":[TD([[makeQuery(id+"F56.imprint","IMPRINT",EDGE,{"derivedFrom":subQ5}),1.0]])]});}
            var sketch = newSketch(context, id + "F59", { "sketchPlane" : qUnion([Q0])});
            skLineSegment(sketch, "E256.0.0", {"start": v(73.94, -2.23) * mm, "end": v(73.03, -2.23) * mm});
            skLineSegment(sketch, "E256.0.1", {"start": v(73.03, -2.23) * mm, "end": v(73.03, -25.4) * mm});
            skLineSegment(sketch, "E256.0.2", {"start": v(73.03, -25.4) * mm, "end": v(76.2, -25.4) * mm});
            skLineSegment(sketch, "E256.0.3", {"start": v(76.2, -25.4) * mm, "end": v(76.2, -2.23) * mm});
            skLineSegment(sketch, "E256.0.4", {"start": v(76.2, -2.23) * mm, "end": v(73.94, -2.23) * mm});
            skLineSegment(sketch, "E257.0.0", {"start": v(60.32, -52.9) * mm, "end": v(76.2, -25.4) * mm});
            skLineSegment(sketch, "E257.0.1", {"start": v(76.2, -25.4) * mm, "end": v(73.45, -23.81) * mm});
            skLineSegment(sketch, "E257.0.2", {"start": v(73.45, -23.81) * mm, "end": v(57.58, -51.3) * mm});
            skLineSegment(sketch, "E257.0.3", {"start": v(57.58, -51.3) * mm, "end": v(60.32, -52.9) * mm});
            skLineSegment(sketch, "E258", {"start": v(73.03, -23.81) * mm, "end": v(76.2, -23.81) * mm});
            skSolve(sketch);
        }
        {
            var Q0;
            Q0=makeQuery(id+"F8.opExtrude","SWEPT_FACE",FACE,{"disambiguationData":[OSD([sQuery(id+"F0.wireOp",EDGE,"E2")])]});
            var sketch = newSketch(context, id + "F60", { "sketchPlane" : qUnion([Q0])});
            skLineSegment(sketch, "E259.0.0", {"start": v(2.23, -47.62) * mm, "end": v(2.23, -40.48) * mm});
            skLineSegment(sketch, "E259.0.1", {"start": v(25.4, -40.48) * mm, "end": v(2.23, -40.48) * mm});
            skLineSegment(sketch, "E259.0.2", {"start": v(0, -40.48) * mm, "end": v(0, -47.62) * mm});
            skLineSegment(sketch, "E259.0.3", {"start": v(2.23, -47.63) * mm, "end": v(25.4, -47.63) * mm});
            skLineSegment(sketch, "E260.0.0", {"start": v(0, -34.13) * mm, "end": v(25.4, -34.13) * mm});
            skLineSegment(sketch, "E260.0.1", {"start": v(2.23, -34.13) * mm, "end": v(2.23, -26.99) * mm});
            skLineSegment(sketch, "E260.0.2", {"start": v(25.4, -26.99) * mm, "end": v(0, -26.99) * mm});
            skLineSegment(sketch, "E260.0.3", {"start": v(0, -26.99) * mm, "end": v(0, -34.13) * mm});
            skLineSegment(sketch, "E261.0.0", {"start": v(0, -20.64) * mm, "end": v(25.4, -20.64) * mm});
            skLineSegment(sketch, "E261.0.1", {"start": v(2.23, -20.64) * mm, "end": v(2.23, -13.5) * mm});
            skLineSegment(sketch, "E261.0.2", {"start": v(25.4, -13.5) * mm, "end": v(0, -13.5) * mm});
            skLineSegment(sketch, "E261.0.3", {"start": v(0, -13.5) * mm, "end": v(0, -20.64) * mm});
            skLineSegment(sketch, "E262.0.0", {"start": v(0, -7.14) * mm, "end": v(25.4, -7.14) * mm});
            skLineSegment(sketch, "E262.0.2", {"start": v(25.4, 0) * mm, "end": v(2.23, 0) * mm});
            skLineSegment(sketch, "E262.0.3", {"start": v(0, 0) * mm, "end": v(0, -7.14) * mm});
            skLineSegment(sketch, "E263.0", {"start": v(25.4, -47.62) * mm, "end": v(25.4, 0) * mm});
            skPoint(sketch, "E264.orphan", {"position": v(2.23, -7.14) * mm});
            skPoint(sketch, "E265.0", {"position": v(23.81, -47.62) * mm});
            skLineSegment(sketch, "E266", {"start": v(23.81, -47.62) * mm, "end": v(23.81, 0) * mm});
            skSolve(sketch);
        }
        {
            var Q0;
            {var subQ0=sQuery(id+"F60.wireOp",EDGE,"E263.0");var subQ1=sQuery(id+"F60.wireOp",EDGE,"E261.0.2");var subQ2=makeQuery(id+"F60.imprint","INTERSECT",VERTEX,{"derivedFrom":[subQ1,subQ0]});Q0=makeQuery(id+"F60.imprint","IMPRINT",FACE,{"disambiguationData":[TD([[makeQuery(id+"F60.imprint","IMPRINT",EDGE,{"disambiguationData":[TD([[subQ2,-1.0]])],"derivedFrom":subQ1}),-1.0]])]});}
            var Q1;
            {var subQ0=sQuery(id+"F60.wireOp",EDGE,"E263.0");var subQ1=sQuery(id+"F60.wireOp",EDGE,"E260.0.2");var subQ2=makeQuery(id+"F60.imprint","INTERSECT",VERTEX,{"derivedFrom":[subQ1,subQ0]});Q1=makeQuery(id+"F60.imprint","IMPRINT",FACE,{"disambiguationData":[TD([[makeQuery(id+"F60.imprint","IMPRINT",EDGE,{"disambiguationData":[TD([[subQ2,-1.0]])],"derivedFrom":subQ1}),-1.0]])]});}
            var Q2;
            {var subQ0=sQuery(id+"F60.wireOp",EDGE,"E263.0");var subQ1=sQuery(id+"F60.wireOp",EDGE,"E259.0.1");var subQ2=makeQuery(id+"F60.imprint","INTERSECT",VERTEX,{"derivedFrom":[subQ1,subQ0]});Q2=makeQuery(id+"F60.imprint","IMPRINT",FACE,{"disambiguationData":[TD([[makeQuery(id+"F60.imprint","IMPRINT",EDGE,{"disambiguationData":[TD([[subQ2,-1.0]])],"derivedFrom":subQ1}),-1.0]])]});}
            extrude(context, id + "F61", {"entities" : qUnion([Q0, Q1, Q2]), "operationType" : NewBodyOperationType.REMOVE, "oppositeDirection" : true, "depth" : 25.4 * mm, "offsetDistance" : 25.4 * mm});
        }
        {
            var Q0;
            {var subQ3=sQuery(id+"F38.wireOp",EDGE,"E197.0.0");Q0=makeQuery(id+"F38.imprint","IMPRINT",FACE,{"disambiguationData":[TD([[makeQuery(id+"F38.imprint","IMPRINT",EDGE,{"derivedFrom":subQ3}),-1.0]])]});}
            var sketch = newSketch(context, id + "F62", { "sketchPlane" : qUnion([Q0])});
            skLineSegment(sketch, "E267.0.0", {"start": v(-14.52, -34.13) * mm, "end": v(-14.52, -26.99) * mm});
            skLineSegment(sketch, "E267.0.1", {"start": v(-14.52, -26.99) * mm, "end": v(-16.1, -26.99) * mm});
            skLineSegment(sketch, "E267.0.2", {"start": v(-16.1, -26.99) * mm, "end": v(-16.1, -34.13) * mm});
            skLineSegment(sketch, "E267.0.3", {"start": v(-16.1, -34.13) * mm, "end": v(-14.52, -34.13) * mm});
            skLineSegment(sketch, "E268.0.0", {"start": v(-14.52, -47.62) * mm, "end": v(-14.52, -40.48) * mm});
            skLineSegment(sketch, "E268.0.1", {"start": v(-14.52, -40.48) * mm, "end": v(-16.1, -40.48) * mm});
            skLineSegment(sketch, "E268.0.2", {"start": v(-16.1, -40.48) * mm, "end": v(-16.1, -47.62) * mm});
            skLineSegment(sketch, "E268.0.3", {"start": v(-16.1, -47.63) * mm, "end": v(-14.52, -47.63) * mm});
            skLineSegment(sketch, "E269.0.0", {"start": v(-14.52, -20.64) * mm, "end": v(-14.52, -13.5) * mm});
            skLineSegment(sketch, "E269.0.1", {"start": v(-14.52, -13.5) * mm, "end": v(-16.1, -13.5) * mm});
            skLineSegment(sketch, "E269.0.2", {"start": v(-16.1, -13.5) * mm, "end": v(-16.1, -20.64) * mm});
            skLineSegment(sketch, "E269.0.3", {"start": v(-16.1, -20.64) * mm, "end": v(-14.52, -20.64) * mm});
            skLineSegment(sketch, "E270.0.0", {"start": v(-16.1, -7.14) * mm, "end": v(-14.52, -7.14) * mm});
            skLineSegment(sketch, "E270.0.1", {"start": v(-14.52, -7.14) * mm, "end": v(-14.52, 0) * mm});
            skLineSegment(sketch, "E270.0.2", {"start": v(-14.52, 0) * mm, "end": v(-16.1, 0) * mm});
            skLineSegment(sketch, "E270.0.3", {"start": v(-16.1, 0) * mm, "end": v(-16.1, -7.14) * mm});
            skSolve(sketch);
        }
        {
            var Q0;
            Q0=qSketchRegion(id+"F62",true);
            extrude(context, id + "F63", {"entities" : qUnion([Q0]), "operationType" : NewBodyOperationType.REMOVE, "oppositeDirection" : true, "depth" : 25.4 * mm, "offsetDistance" : 25.4 * mm});
        }
        {
            var Q0;
            Q0=makeQuery(id+"F9.opExtrude","CAP_FACE",FACE,{"disambiguationData":[OSD([sQuery(id+"F0.wireOp",EDGE,"E3"),sQuery(id+"F2.wireOp",EDGE,"E37"),sQuery(id+"F2.wireOp",EDGE,"E38"),sQuery(id+"F2.wireOp",EDGE,"E39")])],"isStart":false});
            var sketch = newSketch(context, id + "F64", { "sketchPlane" : qUnion([Q0])});
            skLineSegment(sketch, "E271", {"start": v(58.95, -48.93) * mm, "end": v(61.7, -50.52) * mm});
            skLineSegment(sketch, "E272.0", {"start": v(57.58, -51.3) * mm, "end": v(72.66, -25.19) * mm});
            skLineSegment(sketch, "E273.0.0", {"start": v(75.4, -26.77) * mm, "end": v(72.66, -25.19) * mm});
            skLineSegment(sketch, "E273.0.1", {"start": v(72.66, -25.19) * mm, "end": v(57.58, -51.3) * mm});
            skLineSegment(sketch, "E273.0.2", {"start": v(57.58, -51.3) * mm, "end": v(60.32, -52.9) * mm});
            skLineSegment(sketch, "E273.0.3", {"start": v(60.32, -52.9) * mm, "end": v(75.4, -26.77) * mm});
            skLineSegment(sketch, "E274.0.0", {"start": v(60.32, -52.9) * mm, "end": v(60.32, -49.72) * mm});
            skLineSegment(sketch, "E274.0.1", {"start": v(60.32, -49.72) * mm, "end": v(22.23, -49.72) * mm});
            skLineSegment(sketch, "E274.0.2", {"start": v(22.23, -49.72) * mm, "end": v(22.23, -52.9) * mm});
            skLineSegment(sketch, "E274.0.3", {"start": v(22.23, -52.9) * mm, "end": v(60.32, -52.9) * mm});
            skSolve(sketch);
        }
        {
            var Q0;
            {var subQ3=sQuery(id+"F38.wireOp",EDGE,"E197.0.0");Q0=makeQuery(id+"F38.imprint","IMPRINT",FACE,{"disambiguationData":[TD([[makeQuery(id+"F38.imprint","IMPRINT",EDGE,{"derivedFrom":subQ3}),-1.0]])]});}
            var sketch = newSketch(context, id + "F65", { "sketchPlane" : qUnion([Q0])});
            skLineSegment(sketch, "E275.0.0", {"start": v(-12.93, 0) * mm, "end": v(-16.1, 0) * mm});
            skLineSegment(sketch, "E275.0.1", {"start": v(-16.1, 0) * mm, "end": v(-16.1, -47.62) * mm});
            skLineSegment(sketch, "E275.0.2", {"start": v(-16.1, -47.63) * mm, "end": v(15.65, -47.63) * mm});
            skLineSegment(sketch, "E275.0.3", {"start": v(15.65, -47.62) * mm, "end": v(15.65, 0) * mm});
            skLineSegment(sketch, "E275.0.4", {"start": v(15.65, 0) * mm, "end": v(12.47, 0) * mm});
            skLineSegment(sketch, "E275.0.5", {"start": v(12.47, 0) * mm, "end": v(12.47, 3.18) * mm});
            skLineSegment(sketch, "E275.0.6", {"start": v(12.47, 3.18) * mm, "end": v(8.96, 3.18) * mm});
            skLineSegment(sketch, "E275.0.7", {"start": v(8.96, 3.18) * mm, "end": v(8.96, 0) * mm});
            skLineSegment(sketch, "E275.0.8", {"start": v(8.96, 0) * mm, "end": v(1.53, 0) * mm});
            skLineSegment(sketch, "E275.0.9", {"start": v(1.53, 0) * mm, "end": v(1.53, 3.18) * mm});
            skLineSegment(sketch, "E275.0.10", {"start": v(1.53, 3.18) * mm, "end": v(-1.98, 3.18) * mm});
            skLineSegment(sketch, "E275.0.11", {"start": v(-1.98, 3.18) * mm, "end": v(-1.98, 0) * mm});
            skLineSegment(sketch, "E275.0.12", {"start": v(-1.98, 0) * mm, "end": v(-9.42, 0) * mm});
            skLineSegment(sketch, "E275.0.13", {"start": v(-9.42, 0) * mm, "end": v(-9.42, 3.18) * mm});
            skLineSegment(sketch, "E275.0.14", {"start": v(-9.42, 3.18) * mm, "end": v(-12.93, 3.18) * mm});
            skLineSegment(sketch, "E275.0.15", {"start": v(-12.93, 3.18) * mm, "end": v(-12.93, 0) * mm});
            skLineSegment(sketch, "E276.0.0", {"start": v(15.65, -34.13) * mm, "end": v(-15.9, -34.13) * mm});
            skLineSegment(sketch, "E276.0.1", {"start": v(-17.48, -34.13) * mm, "end": v(-17.48, -40.48) * mm});
            skLineSegment(sketch, "E276.0.2", {"start": v(-15.9, -40.48) * mm, "end": v(15.65, -40.48) * mm});
            skLineSegment(sketch, "E276.0.3", {"start": v(-15.9, -40.48) * mm, "end": v(-15.9, -34.13) * mm});
            skLineSegment(sketch, "E277.0.0", {"start": v(15.65, -20.64) * mm, "end": v(-17.48, -20.64) * mm});
            skLineSegment(sketch, "E277.0.1", {"start": v(-17.48, -20.64) * mm, "end": v(-17.48, -26.99) * mm});
            skLineSegment(sketch, "E277.0.2", {"start": v(-17.48, -26.99) * mm, "end": v(15.65, -26.99) * mm});
            skLineSegment(sketch, "E277.0.3", {"start": v(-15.9, -26.99) * mm, "end": v(-15.9, -20.64) * mm});
            skLineSegment(sketch, "E278.0.0", {"start": v(15.65, -7.14) * mm, "end": v(-15.9, -7.14) * mm});
            skLineSegment(sketch, "E278.0.1", {"start": v(-17.48, -7.14) * mm, "end": v(-17.48, -13.5) * mm});
            skLineSegment(sketch, "E278.0.2", {"start": v(-15.9, -13.5) * mm, "end": v(15.65, -13.5) * mm});
            skLineSegment(sketch, "E278.0.3", {"start": v(-15.9, -13.5) * mm, "end": v(-15.9, -7.14) * mm});
            skPoint(sketch, "E279.0", {"position": v(12.9, -47.62) * mm});
            skLineSegment(sketch, "E280", {"start": v(12.9, -47.62) * mm, "end": v(12.9, 0) * mm});
            skPoint(sketch, "E281.orphan", {"position": v(12.9, 14.3) * mm});
            skSolve(sketch);
        }
        {
            var Q0;
            {var subQ0=sQuery(id+"F65.wireOp",EDGE,"E276.0.0");var subQ1=sQuery(id+"F65.wireOp",EDGE,"E275.0.3");var subQ2=makeQuery(id+"F65.imprint","INTERSECT",VERTEX,{"derivedFrom":[subQ1,subQ0]});Q0=makeQuery(id+"F65.imprint","IMPRINT",FACE,{"disambiguationData":[TD([[makeQuery(id+"F65.imprint","IMPRINT",EDGE,{"disambiguationData":[TD([[subQ2,1.0]])],"derivedFrom":subQ1}),1.0]])]});}
            var Q1;
            {var subQ0=sQuery(id+"F65.wireOp",EDGE,"E277.0.0");var subQ1=sQuery(id+"F65.wireOp",EDGE,"E275.0.3");var subQ2=makeQuery(id+"F65.imprint","INTERSECT",VERTEX,{"derivedFrom":[subQ1,subQ0]});Q1=makeQuery(id+"F65.imprint","IMPRINT",FACE,{"disambiguationData":[TD([[makeQuery(id+"F65.imprint","IMPRINT",EDGE,{"disambiguationData":[TD([[subQ2,1.0]])],"derivedFrom":subQ1}),1.0]])]});}
            var Q2;
            {var subQ0=sQuery(id+"F65.wireOp",EDGE,"E278.0.0");var subQ1=sQuery(id+"F65.wireOp",EDGE,"E275.0.3");var subQ2=makeQuery(id+"F65.imprint","INTERSECT",VERTEX,{"derivedFrom":[subQ1,subQ0]});Q2=makeQuery(id+"F65.imprint","IMPRINT",FACE,{"disambiguationData":[TD([[makeQuery(id+"F65.imprint","IMPRINT",EDGE,{"disambiguationData":[TD([[subQ2,1.0]])],"derivedFrom":subQ1}),1.0]])]});}
            extrude(context, id + "F66", {"entities" : qUnion([Q0, Q1, Q2]), "operationType" : NewBodyOperationType.REMOVE, "oppositeDirection" : true, "depth" : 25.4 * mm, "offsetDistance" : 25.4 * mm});
        }
        {
            var Q0;
            Q0=makeQuery(id+"F10.opExtrude","SWEPT_FACE",FACE,{"disambiguationData":[OSD([sQuery(id+"F0.wireOp",EDGE,"E4")])]});
            var sketch = newSketch(context, id + "F67", { "sketchPlane" : qUnion([Q0])});
            skLineSegment(sketch, "E282.0.0", {"start": v(-57.58, -47.62) * mm, "end": v(-57.58, -40.48) * mm});
            skLineSegment(sketch, "E282.0.1", {"start": v(-57.58, -40.48) * mm, "end": v(-60.32, -40.48) * mm});
            skLineSegment(sketch, "E282.0.2", {"start": v(-60.33, -40.48) * mm, "end": v(-60.33, -47.62) * mm});
            skLineSegment(sketch, "E282.0.3", {"start": v(-60.32, -47.63) * mm, "end": v(-57.58, -47.63) * mm});
            skLineSegment(sketch, "E283.0.0", {"start": v(-60.32, -34.13) * mm, "end": v(-57.58, -34.13) * mm});
            skLineSegment(sketch, "E283.0.1", {"start": v(-57.58, -34.13) * mm, "end": v(-57.58, -26.99) * mm});
            skLineSegment(sketch, "E283.0.2", {"start": v(-57.58, -26.99) * mm, "end": v(-60.32, -26.99) * mm});
            skLineSegment(sketch, "E283.0.3", {"start": v(-60.33, -26.99) * mm, "end": v(-60.33, -34.13) * mm});
            skLineSegment(sketch, "E284.0.0", {"start": v(-60.32, -20.64) * mm, "end": v(-57.58, -20.64) * mm});
            skLineSegment(sketch, "E284.0.1", {"start": v(-57.58, -20.64) * mm, "end": v(-57.58, -13.5) * mm});
            skLineSegment(sketch, "E284.0.2", {"start": v(-57.58, -13.5) * mm, "end": v(-60.32, -13.5) * mm});
            skLineSegment(sketch, "E284.0.3", {"start": v(-60.33, -13.5) * mm, "end": v(-60.33, -20.64) * mm});
            skLineSegment(sketch, "E285.0.0", {"start": v(-60.32, -7.14) * mm, "end": v(-57.58, -7.14) * mm});
            skLineSegment(sketch, "E285.0.1", {"start": v(-57.58, -7.14) * mm, "end": v(-57.58, 0) * mm});
            skLineSegment(sketch, "E285.0.2", {"start": v(-57.58, 0) * mm, "end": v(-60.32, 0) * mm});
            skLineSegment(sketch, "E285.0.3", {"start": v(-60.33, 0) * mm, "end": v(-60.33, -7.14) * mm});
            skSolve(sketch);
        }
        {
            var Q0;
            Q0=qSketchRegion(id+"F67",true);
            extrude(context, id + "F68", {"entities" : qUnion([Q0]), "operationType" : NewBodyOperationType.REMOVE, "oppositeDirection" : true, "depth" : 25.4 * mm, "offsetDistance" : 25.4 * mm});
        }
        {
            var Q0;
            {var subQ4=sQuery(id+"F64.wireOp",EDGE,"E273.0.2");Q0=makeQuery(id+"F64.imprint","IMPRINT",FACE,{"disambiguationData":[TD([[makeQuery(id+"F64.imprint","IMPRINT",EDGE,{"derivedFrom":subQ4}),1.0]])]});}
            var sketch = newSketch(context, id + "F69", { "sketchPlane" : qUnion([Q0])});
            skLineSegment(sketch, "E286.0.0", {"start": v(22.23, -52.9) * mm, "end": v(23.76, -50.12) * mm});
            skLineSegment(sketch, "E286.0.1", {"start": v(23.76, -50.12) * mm, "end": v(0, -36.97) * mm});
            skLineSegment(sketch, "E286.0.2", {"start": v(0, -36.97) * mm, "end": v(-1.54, -39.75) * mm});
            skLineSegment(sketch, "E286.0.3", {"start": v(-1.54, -39.75) * mm, "end": v(22.23, -52.9) * mm});
            skLineSegment(sketch, "E287.0.0", {"start": v(22.23, -49.72) * mm, "end": v(22.23, -52.9) * mm});
            skLineSegment(sketch, "E287.0.1", {"start": v(22.23, -52.9) * mm, "end": v(60.32, -52.9) * mm});
            skLineSegment(sketch, "E287.0.2", {"start": v(60.32, -52.9) * mm, "end": v(57.58, -51.3) * mm});
            skLineSegment(sketch, "E287.0.3", {"start": v(57.58, -51.3) * mm, "end": v(58.5, -49.72) * mm});
            skLineSegment(sketch, "E287.0.4", {"start": v(58.5, -49.72) * mm, "end": v(22.23, -49.72) * mm});
            skLineSegment(sketch, "E288", {"start": v(23.76, -49.72) * mm, "end": v(23.76, -52.9) * mm});
            skSolve(sketch);
        }
        {
            var Q0;
            Q0=makeQuery(id+"F10.opExtrude","SWEPT_FACE",FACE,{"disambiguationData":[OSD([sQuery(id+"F0.wireOp",EDGE,"E4")])]});
            var sketch = newSketch(context, id + "F70", { "sketchPlane" : qUnion([Q0])});
            skLineSegment(sketch, "E289.0.0", {"start": v(-57.58, -40.48) * mm, "end": v(-57.58, -47.62) * mm});
            skLineSegment(sketch, "E289.0.1", {"start": v(-57.58, -47.63) * mm, "end": v(-22.23, -47.63) * mm});
            skLineSegment(sketch, "E289.0.2", {"start": v(-22.23, -47.62) * mm, "end": v(-22.23, 0) * mm});
            skLineSegment(sketch, "E289.0.3", {"start": v(-22.23, 0) * mm, "end": v(-25.4, 0) * mm});
            skLineSegment(sketch, "E289.0.4", {"start": v(-25.4, 0) * mm, "end": v(-25.4, 3.18) * mm});
            skLineSegment(sketch, "E289.0.5", {"start": v(-25.4, 3.18) * mm, "end": v(-31.75, 3.18) * mm});
            skLineSegment(sketch, "E289.0.6", {"start": v(-31.75, 3.18) * mm, "end": v(-31.75, 0) * mm});
            skLineSegment(sketch, "E289.0.7", {"start": v(-31.75, 0) * mm, "end": v(-38.1, 0) * mm});
            skLineSegment(sketch, "E289.0.8", {"start": v(-38.1, 0) * mm, "end": v(-38.1, 3.18) * mm});
            skLineSegment(sketch, "E289.0.9", {"start": v(-38.1, 3.18) * mm, "end": v(-44.45, 3.18) * mm});
            skLineSegment(sketch, "E289.0.10", {"start": v(-44.45, 3.18) * mm, "end": v(-44.45, 0) * mm});
            skLineSegment(sketch, "E289.0.11", {"start": v(-44.45, 0) * mm, "end": v(-50.8, 0) * mm});
            skLineSegment(sketch, "E289.0.12", {"start": v(-50.8, 0) * mm, "end": v(-50.8, 3.18) * mm});
            skLineSegment(sketch, "E289.0.13", {"start": v(-50.8, 3.18) * mm, "end": v(-57.15, 3.18) * mm});
            skLineSegment(sketch, "E289.0.14", {"start": v(-57.15, 3.18) * mm, "end": v(-57.15, 0) * mm});
            skLineSegment(sketch, "E289.0.15", {"start": v(-57.15, 0) * mm, "end": v(-57.58, 0) * mm});
            skLineSegment(sketch, "E289.0.16", {"start": v(-57.58, 0) * mm, "end": v(-57.58, -7.14) * mm});
            skLineSegment(sketch, "E289.0.17", {"start": v(-22.23, -7.14) * mm, "end": v(-57.58, -7.14) * mm});
            skLineSegment(sketch, "E289.0.18", {"start": v(-60.33, -7.14) * mm, "end": v(-60.33, -13.5) * mm});
            skLineSegment(sketch, "E289.0.19", {"start": v(-60.32, -13.5) * mm, "end": v(-22.23, -13.5) * mm});
            skLineSegment(sketch, "E289.0.20", {"start": v(-57.58, -13.5) * mm, "end": v(-57.58, -20.64) * mm});
            skLineSegment(sketch, "E289.0.21", {"start": v(-22.23, -20.64) * mm, "end": v(-57.58, -20.64) * mm});
            skLineSegment(sketch, "E289.0.22", {"start": v(-60.33, -20.64) * mm, "end": v(-60.33, -26.99) * mm});
            skLineSegment(sketch, "E289.0.23", {"start": v(-57.58, -26.99) * mm, "end": v(-22.23, -26.99) * mm});
            skLineSegment(sketch, "E289.0.24", {"start": v(-57.58, -26.99) * mm, "end": v(-57.58, -34.13) * mm});
            skLineSegment(sketch, "E289.0.25", {"start": v(-22.23, -34.13) * mm, "end": v(-57.58, -34.13) * mm});
            skLineSegment(sketch, "E289.0.26", {"start": v(-60.33, -34.13) * mm, "end": v(-60.33, -40.48) * mm});
            skLineSegment(sketch, "E289.0.27", {"start": v(-60.32, -40.48) * mm, "end": v(-22.23, -40.48) * mm});
            skPoint(sketch, "E290.0", {"position": v(-23.76, -47.62) * mm});
            skLineSegment(sketch, "E291", {"start": v(-23.76, -47.62) * mm, "end": v(-23.76, 0) * mm});
            skSolve(sketch);
        }
        {
            var Q0;
            {var subQ0=sQuery(id+"F70.wireOp",EDGE,"E289.0.25");var subQ1=sQuery(id+"F70.wireOp",EDGE,"E289.0.2");var subQ2=makeQuery(id+"F70.imprint","INTERSECT",VERTEX,{"derivedFrom":[subQ1,subQ0]});Q0=makeQuery(id+"F70.imprint","IMPRINT",FACE,{"disambiguationData":[TD([[makeQuery(id+"F70.imprint","IMPRINT",EDGE,{"disambiguationData":[TD([[subQ2,1.0]])],"derivedFrom":subQ1}),1.0]])]});}
            var Q1;
            {var subQ0=sQuery(id+"F70.wireOp",EDGE,"E289.0.21");var subQ1=sQuery(id+"F70.wireOp",EDGE,"E289.0.2");var subQ2=makeQuery(id+"F70.imprint","INTERSECT",VERTEX,{"derivedFrom":[subQ1,subQ0]});Q1=makeQuery(id+"F70.imprint","IMPRINT",FACE,{"disambiguationData":[TD([[makeQuery(id+"F70.imprint","IMPRINT",EDGE,{"disambiguationData":[TD([[subQ2,1.0]])],"derivedFrom":subQ1}),1.0]])]});}
            var Q2;
            {var subQ0=sQuery(id+"F70.wireOp",EDGE,"E289.0.17");var subQ1=sQuery(id+"F70.wireOp",EDGE,"E289.0.2");var subQ2=makeQuery(id+"F70.imprint","INTERSECT",VERTEX,{"derivedFrom":[subQ1,subQ0]});Q2=makeQuery(id+"F70.imprint","IMPRINT",FACE,{"disambiguationData":[TD([[makeQuery(id+"F70.imprint","IMPRINT",EDGE,{"disambiguationData":[TD([[subQ2,1.0]])],"derivedFrom":subQ1}),1.0]])]});}
            extrude(context, id + "F71", {"entities" : qUnion([Q0, Q1, Q2]), "operationType" : NewBodyOperationType.REMOVE, "oppositeDirection" : true, "depth" : 25.4 * mm, "offsetDistance" : 25.4 * mm});
        }
        {
            var Q0;
            Q0=makeQuery(id+"F11.opExtrude","SWEPT_FACE",FACE,{"disambiguationData":[OSD([sQuery(id+"F0.wireOp",EDGE,"E5"),sQuery(id+"F2.wireOp",EDGE,"E45")])]});
            var sketch = newSketch(context, id + "F72", { "sketchPlane" : qUnion([Q0])});
            skLineSegment(sketch, "E292.0.0", {"start": v(-45.06, -7.14) * mm, "end": v(-43.52, -7.14) * mm});
            skLineSegment(sketch, "E292.0.1", {"start": v(-43.52, -7.14) * mm, "end": v(-43.52, 0) * mm});
            skLineSegment(sketch, "E292.0.2", {"start": v(-43.52, 0) * mm, "end": v(-45.06, 0) * mm});
            skLineSegment(sketch, "E292.0.3", {"start": v(-45.06, 0) * mm, "end": v(-45.06, -7.14) * mm});
            skLineSegment(sketch, "E292.1.0", {"start": v(-45.06, -20.64) * mm, "end": v(-43.52, -20.64) * mm});
            skLineSegment(sketch, "E292.1.1", {"start": v(-43.52, -20.64) * mm, "end": v(-43.52, -13.5) * mm});
            skLineSegment(sketch, "E292.1.2", {"start": v(-43.52, -13.5) * mm, "end": v(-45.06, -13.5) * mm});
            skLineSegment(sketch, "E292.1.3", {"start": v(-45.06, -13.5) * mm, "end": v(-45.06, -20.64) * mm});
            skLineSegment(sketch, "E292.2.0", {"start": v(-45.06, -34.13) * mm, "end": v(-43.52, -34.13) * mm});
            skLineSegment(sketch, "E292.2.1", {"start": v(-43.52, -34.13) * mm, "end": v(-43.52, -26.99) * mm});
            skLineSegment(sketch, "E292.2.2", {"start": v(-43.52, -26.99) * mm, "end": v(-45.06, -26.99) * mm});
            skLineSegment(sketch, "E292.2.3", {"start": v(-45.06, -26.99) * mm, "end": v(-45.06, -34.13) * mm});
            skLineSegment(sketch, "E292.3.0", {"start": v(-43.52, -47.62) * mm, "end": v(-43.52, -40.48) * mm});
            skLineSegment(sketch, "E292.3.1", {"start": v(-43.52, -40.48) * mm, "end": v(-45.06, -40.48) * mm});
            skLineSegment(sketch, "E292.3.2", {"start": v(-45.06, -40.48) * mm, "end": v(-45.06, -47.62) * mm});
            skLineSegment(sketch, "E292.3.3", {"start": v(-45.06, -47.63) * mm, "end": v(-43.52, -47.63) * mm});
            skSolve(sketch);
        }
        {
            var Q0;
            Q0=qSketchRegion(id+"F72",true);
            extrude(context, id + "F73", {"entities" : qUnion([Q0]), "operationType" : NewBodyOperationType.REMOVE, "oppositeDirection" : true, "depth" : 25.4 * mm, "offsetDistance" : 25.4 * mm});
        }
        {
            var Q0;
            {var subQ1=sQuery(id+"F69.wireOp",EDGE,"E286.0.2");Q0=makeQuery(id+"F69.imprint","IMPRINT",FACE,{"disambiguationData":[TD([[makeQuery(id+"F69.imprint","IMPRINT",EDGE,{"derivedFrom":subQ1}),1.0]])]});}
            var sketch = newSketch(context, id + "F74", { "sketchPlane" : qUnion([Q0])});
            skLineSegment(sketch, "E293.0", {"start": v(-23.76, -50.12) * mm, "end": v(0, -36.97) * mm});
            skLineSegment(sketch, "E294.0.0", {"start": v(0, -36.97) * mm, "end": v(-1.54, -39.75) * mm});
            skLineSegment(sketch, "E294.0.1", {"start": v(-1.54, -39.75) * mm, "end": v(22.23, -52.9) * mm});
            skLineSegment(sketch, "E294.0.2", {"start": v(22.23, -52.9) * mm, "end": v(22.23, -49.72) * mm});
            skLineSegment(sketch, "E294.0.3", {"start": v(22.23, -49.72) * mm, "end": v(23.04, -49.72) * mm});
            skLineSegment(sketch, "E294.0.4", {"start": v(23.04, -49.72) * mm, "end": v(0, -36.97) * mm});
            skLineSegment(sketch, "E294.1.0", {"start": v(-22.23, -52.9) * mm, "end": v(1.54, -39.75) * mm});
            skLineSegment(sketch, "E294.1.1", {"start": v(1.54, -39.75) * mm, "end": v(0, -36.97) * mm});
            skLineSegment(sketch, "E294.1.2", {"start": v(0, -36.97) * mm, "end": v(-23.76, -50.12) * mm});
            skLineSegment(sketch, "E294.1.3", {"start": v(-23.76, -50.12) * mm, "end": v(-22.23, -52.9) * mm});
            skLineSegment(sketch, "E295", {"start": v(2.35, -38.27) * mm, "end": v(0.82, -41.05) * mm});
            skSolve(sketch);
        }
        {
            var Q0;
            Q0=makeQuery(id+"F11.opExtrude","SWEPT_FACE",FACE,{"disambiguationData":[OSD([sQuery(id+"F0.wireOp",EDGE,"E5"),sQuery(id+"F2.wireOp",EDGE,"E45")])]});
            var sketch = newSketch(context, id + "F75", { "sketchPlane" : qUnion([Q0])});
            skLineSegment(sketch, "E296.0.0", {"start": v(-17.9, -7.14) * mm, "end": v(-43.52, -7.14) * mm});
            skLineSegment(sketch, "E296.0.1", {"start": v(-45.06, -7.14) * mm, "end": v(-45.06, -13.5) * mm});
            skLineSegment(sketch, "E296.0.2", {"start": v(-43.52, -13.5) * mm, "end": v(-17.9, -13.5) * mm});
            skLineSegment(sketch, "E296.0.3", {"start": v(-43.52, -13.5) * mm, "end": v(-43.52, -20.64) * mm});
            skLineSegment(sketch, "E296.0.4", {"start": v(-17.9, -20.64) * mm, "end": v(-43.52, -20.64) * mm});
            skLineSegment(sketch, "E296.0.5", {"start": v(-45.06, -20.64) * mm, "end": v(-45.06, -26.99) * mm});
            skLineSegment(sketch, "E296.0.6", {"start": v(-45.06, -26.99) * mm, "end": v(-17.9, -26.99) * mm});
            skLineSegment(sketch, "E296.0.7", {"start": v(-43.52, -26.99) * mm, "end": v(-43.52, -34.13) * mm});
            skLineSegment(sketch, "E296.0.8", {"start": v(-17.9, -34.13) * mm, "end": v(-45.06, -34.13) * mm});
            skLineSegment(sketch, "E296.0.9", {"start": v(-45.06, -34.13) * mm, "end": v(-45.06, -40.48) * mm});
            skLineSegment(sketch, "E296.0.10", {"start": v(-43.52, -40.48) * mm, "end": v(-17.9, -40.48) * mm});
            skLineSegment(sketch, "E296.0.11", {"start": v(-43.52, -40.48) * mm, "end": v(-43.52, -47.62) * mm});
            skLineSegment(sketch, "E296.0.12", {"start": v(-43.52, -47.63) * mm, "end": v(-17.9, -47.63) * mm});
            skLineSegment(sketch, "E296.0.13", {"start": v(-17.9, -47.62) * mm, "end": v(-17.9, 3.17) * mm});
            skLineSegment(sketch, "E296.0.14", {"start": v(-17.9, 3.18) * mm, "end": v(-19.66, 3.18) * mm});
            skLineSegment(sketch, "E296.0.15", {"start": v(-19.66, 3.18) * mm, "end": v(-19.66, 0) * mm});
            skLineSegment(sketch, "E296.0.16", {"start": v(-19.66, 0) * mm, "end": v(-22.83, 0) * mm});
            skLineSegment(sketch, "E296.0.17", {"start": v(-22.83, 0) * mm, "end": v(-22.83, 3.18) * mm});
            skLineSegment(sketch, "E296.0.18", {"start": v(-22.83, 3.18) * mm, "end": v(-26, 3.18) * mm});
            skLineSegment(sketch, "E296.0.19", {"start": v(-26, 3.18) * mm, "end": v(-26, 0) * mm});
            skLineSegment(sketch, "E296.0.20", {"start": v(-26, 0) * mm, "end": v(-30.77, 0) * mm});
            skLineSegment(sketch, "E296.0.21", {"start": v(-30.77, 0) * mm, "end": v(-30.77, 3.18) * mm});
            skLineSegment(sketch, "E296.0.22", {"start": v(-30.77, 3.18) * mm, "end": v(-33.94, 3.18) * mm});
            skLineSegment(sketch, "E296.0.23", {"start": v(-33.94, 3.18) * mm, "end": v(-33.94, 0) * mm});
            skLineSegment(sketch, "E296.0.24", {"start": v(-33.94, 0) * mm, "end": v(-38.7, 0) * mm});
            skLineSegment(sketch, "E296.0.25", {"start": v(-38.7, 0) * mm, "end": v(-38.7, 3.18) * mm});
            skLineSegment(sketch, "E296.0.26", {"start": v(-38.7, 3.18) * mm, "end": v(-41.88, 3.18) * mm});
            skLineSegment(sketch, "E296.0.27", {"start": v(-41.88, 3.18) * mm, "end": v(-41.88, 0) * mm});
            skLineSegment(sketch, "E296.0.28", {"start": v(-41.88, 0) * mm, "end": v(-43.52, 0) * mm});
            skLineSegment(sketch, "E296.0.29", {"start": v(-43.52, 0) * mm, "end": v(-43.52, -7.14) * mm});
            skPoint(sketch, "E297.0", {"position": v(-20.59, -47.62) * mm});
            skLineSegment(sketch, "E298", {"start": v(-20.59, -47.62) * mm, "end": v(-20.59, 0) * mm});
            skSolve(sketch);
        }
        {
            var Q0;
            {var subQ0=sQuery(id+"F75.wireOp",EDGE,"E296.0.13");var subQ1=sQuery(id+"F75.wireOp",EDGE,"E296.0.8");var subQ2=makeQuery(id+"F75.imprint","INTERSECT",VERTEX,{"derivedFrom":[subQ1,subQ0]});Q0=makeQuery(id+"F75.imprint","IMPRINT",FACE,{"disambiguationData":[TD([[makeQuery(id+"F75.imprint","IMPRINT",EDGE,{"disambiguationData":[TD([[subQ2,-1.0]])],"derivedFrom":subQ1}),1.0]])]});}
            var Q1;
            {var subQ0=sQuery(id+"F75.wireOp",EDGE,"E296.0.13");var subQ1=sQuery(id+"F75.wireOp",EDGE,"E296.0.4");var subQ2=makeQuery(id+"F75.imprint","INTERSECT",VERTEX,{"derivedFrom":[subQ1,subQ0]});Q1=makeQuery(id+"F75.imprint","IMPRINT",FACE,{"disambiguationData":[TD([[makeQuery(id+"F75.imprint","IMPRINT",EDGE,{"disambiguationData":[TD([[subQ2,-1.0]])],"derivedFrom":subQ1}),1.0]])]});}
            var Q2;
            {var subQ0=sQuery(id+"F75.wireOp",EDGE,"E296.0.13");var subQ1=sQuery(id+"F75.wireOp",EDGE,"E296.0.0");var subQ2=makeQuery(id+"F75.imprint","INTERSECT",VERTEX,{"derivedFrom":[subQ1,subQ0]});Q2=makeQuery(id+"F75.imprint","IMPRINT",FACE,{"disambiguationData":[TD([[makeQuery(id+"F75.imprint","IMPRINT",EDGE,{"disambiguationData":[TD([[subQ2,-1.0]])],"derivedFrom":subQ1}),1.0]])]});}
            extrude(context, id + "F76", {"entities" : qUnion([Q0, Q1, Q2]), "operationType" : NewBodyOperationType.REMOVE, "oppositeDirection" : true, "depth" : 25.4 * mm, "offsetDistance" : 25.4 * mm});
        }
        {
            var Q0;
            Q0=makeQuery(id+"F12.opExtrude","SWEPT_FACE",FACE,{"disambiguationData":[OSD([sQuery(id+"F0.wireOp",EDGE,"E6"),sQuery(id+"F2.wireOp",EDGE,"E40")])]});
            var sketch = newSketch(context, id + "F77", { "sketchPlane" : qUnion([Q0])});
            skLineSegment(sketch, "E299.0.0", {"start": v(20.59, -7.14) * mm, "end": v(17.9, -7.14) * mm});
            skLineSegment(sketch, "E299.0.1", {"start": v(17.9, -7.14) * mm, "end": v(17.9, 3.17) * mm});
            skLineSegment(sketch, "E299.0.2", {"start": v(17.9, 3.18) * mm, "end": v(20.59, 3.18) * mm});
            skLineSegment(sketch, "E299.0.3", {"start": v(20.59, 3.17) * mm, "end": v(20.59, -7.14) * mm});
            skLineSegment(sketch, "E299.1.0", {"start": v(20.59, -20.64) * mm, "end": v(17.9, -20.64) * mm});
            skLineSegment(sketch, "E299.1.1", {"start": v(17.9, -20.64) * mm, "end": v(17.9, -13.5) * mm});
            skLineSegment(sketch, "E299.1.2", {"start": v(17.9, -13.5) * mm, "end": v(20.59, -13.5) * mm});
            skLineSegment(sketch, "E299.1.3", {"start": v(20.59, -13.5) * mm, "end": v(20.59, -20.64) * mm});
            skLineSegment(sketch, "E299.2.0", {"start": v(20.59, -34.13) * mm, "end": v(17.9, -34.13) * mm});
            skLineSegment(sketch, "E299.2.1", {"start": v(17.9, -34.13) * mm, "end": v(17.9, -26.99) * mm});
            skLineSegment(sketch, "E299.2.2", {"start": v(17.9, -26.99) * mm, "end": v(20.59, -26.99) * mm});
            skLineSegment(sketch, "E299.2.3", {"start": v(20.59, -26.99) * mm, "end": v(20.59, -34.13) * mm});
            skLineSegment(sketch, "E299.3.0", {"start": v(17.9, -47.62) * mm, "end": v(17.9, -40.48) * mm});
            skLineSegment(sketch, "E299.3.1", {"start": v(17.9, -40.48) * mm, "end": v(20.59, -40.48) * mm});
            skLineSegment(sketch, "E299.3.2", {"start": v(20.59, -40.48) * mm, "end": v(20.59, -47.62) * mm});
            skLineSegment(sketch, "E299.3.3", {"start": v(20.59, -47.63) * mm, "end": v(17.9, -47.63) * mm});
            skSolve(sketch);
        }
        {
            var Q0;
            Q0=qSketchRegion(id+"F77",true);
            extrude(context, id + "F78", {"entities" : qUnion([Q0]), "operationType" : NewBodyOperationType.REMOVE, "oppositeDirection" : true, "depth" : 25.4 * mm, "offsetDistance" : 25.4 * mm});
        }
        {
            var Q0;
            {var subQ4=sQuery(id+"F74.wireOp",EDGE,"E294.0.0");Q0=makeQuery(id+"F74.imprint","IMPRINT",FACE,{"disambiguationData":[TD([[makeQuery(id+"F74.imprint","IMPRINT",EDGE,{"derivedFrom":subQ4}),-1.0]])]});}
            var sketch = newSketch(context, id + "F79", { "sketchPlane" : qUnion([Q0])});
            skLineSegment(sketch, "E300.0.0", {"start": v(-1.54, -39.75) * mm, "end": v(0, -36.97) * mm});
            skLineSegment(sketch, "E300.0.1", {"start": v(0, -36.97) * mm, "end": v(-23.76, -50.12) * mm});
            skLineSegment(sketch, "E300.0.2", {"start": v(-23.76, -50.12) * mm, "end": v(-22.23, -52.9) * mm});
            skLineSegment(sketch, "E300.0.3", {"start": v(-22.23, -52.9) * mm, "end": v(0, -40.6) * mm});
            skLineSegment(sketch, "E300.0.4", {"start": v(0, -40.6) * mm, "end": v(-1.54, -39.75) * mm});
            skLineSegment(sketch, "E301.0.0", {"start": v(-22.23, -49.72) * mm, "end": v(-60.33, -49.72) * mm});
            skLineSegment(sketch, "E301.0.1", {"start": v(-60.33, -49.72) * mm, "end": v(-60.33, -52.9) * mm});
            skLineSegment(sketch, "E301.0.2", {"start": v(-60.33, -52.9) * mm, "end": v(-22.23, -52.9) * mm});
            skLineSegment(sketch, "E301.0.3", {"start": v(-22.23, -52.9) * mm, "end": v(-22.23, -49.72) * mm});
            skLineSegment(sketch, "E302", {"start": v(-22.42, -49.37) * mm, "end": v(-20.88, -52.15) * mm});
            skPoint(sketch, "E302.endSnap0", {"position": v(-22.23, -51.3) * mm});
            skSolve(sketch);
        }
        {
            var Q0;
            Q0=makeQuery(id+"F12.opExtrude","SWEPT_FACE",FACE,{"disambiguationData":[OSD([sQuery(id+"F0.wireOp",EDGE,"E6"),sQuery(id+"F2.wireOp",EDGE,"E40")])]});
            var sketch = newSketch(context, id + "F80", { "sketchPlane" : qUnion([Q0])});
            skLineSegment(sketch, "E303.0.0", {"start": v(20.59, 0) * mm, "end": v(20.59, -7.14) * mm});
            skLineSegment(sketch, "E303.0.1", {"start": v(45.06, -7.14) * mm, "end": v(17.9, -7.14) * mm});
            skLineSegment(sketch, "E303.0.2", {"start": v(17.9, -7.14) * mm, "end": v(17.9, -13.5) * mm});
            skLineSegment(sketch, "E303.0.3", {"start": v(17.9, -13.5) * mm, "end": v(45.06, -13.5) * mm});
            skLineSegment(sketch, "E303.0.4", {"start": v(20.59, -13.5) * mm, "end": v(20.59, -20.64) * mm});
            skLineSegment(sketch, "E303.0.5", {"start": v(45.06, -20.64) * mm, "end": v(17.9, -20.64) * mm});
            skLineSegment(sketch, "E303.0.6", {"start": v(17.9, -20.64) * mm, "end": v(17.9, -26.99) * mm});
            skLineSegment(sketch, "E303.0.7", {"start": v(17.9, -26.99) * mm, "end": v(45.06, -26.99) * mm});
            skLineSegment(sketch, "E303.0.8", {"start": v(20.59, -26.99) * mm, "end": v(20.59, -34.13) * mm});
            skLineSegment(sketch, "E303.0.9", {"start": v(45.06, -34.13) * mm, "end": v(17.9, -34.13) * mm});
            skLineSegment(sketch, "E303.0.10", {"start": v(17.9, -34.13) * mm, "end": v(17.9, -40.48) * mm});
            skLineSegment(sketch, "E303.0.11", {"start": v(17.9, -40.48) * mm, "end": v(45.06, -40.48) * mm});
            skLineSegment(sketch, "E303.0.12", {"start": v(20.59, -40.48) * mm, "end": v(20.59, -47.62) * mm});
            skLineSegment(sketch, "E303.0.13", {"start": v(20.59, -47.63) * mm, "end": v(45.06, -47.63) * mm});
            skLineSegment(sketch, "E303.0.14", {"start": v(45.06, -47.62) * mm, "end": v(45.06, 0) * mm});
            skLineSegment(sketch, "E303.0.15", {"start": v(45.06, 0) * mm, "end": v(41.88, 0) * mm});
            skLineSegment(sketch, "E303.0.16", {"start": v(41.88, 0) * mm, "end": v(41.88, 3.18) * mm});
            skLineSegment(sketch, "E303.0.17", {"start": v(41.88, 3.18) * mm, "end": v(38.7, 3.18) * mm});
            skLineSegment(sketch, "E303.0.18", {"start": v(38.7, 3.18) * mm, "end": v(38.7, 0) * mm});
            skLineSegment(sketch, "E303.0.19", {"start": v(38.7, 0) * mm, "end": v(33.94, 0) * mm});
            skLineSegment(sketch, "E303.0.20", {"start": v(33.94, 0) * mm, "end": v(33.94, 3.18) * mm});
            skLineSegment(sketch, "E303.0.21", {"start": v(33.94, 3.18) * mm, "end": v(30.77, 3.18) * mm});
            skLineSegment(sketch, "E303.0.22", {"start": v(30.77, 3.18) * mm, "end": v(30.77, 0) * mm});
            skLineSegment(sketch, "E303.0.23", {"start": v(30.77, 0) * mm, "end": v(26, 0) * mm});
            skLineSegment(sketch, "E303.0.24", {"start": v(26, 0) * mm, "end": v(26, 3.18) * mm});
            skLineSegment(sketch, "E303.0.25", {"start": v(26, 3.18) * mm, "end": v(22.83, 3.18) * mm});
            skLineSegment(sketch, "E303.0.26", {"start": v(22.83, 3.18) * mm, "end": v(22.83, 0) * mm});
            skLineSegment(sketch, "E303.0.27", {"start": v(22.83, 0) * mm, "end": v(20.59, 0) * mm});
            skPoint(sketch, "E304.0", {"position": v(43.52, -47.62) * mm});
            skLineSegment(sketch, "E305", {"start": v(43.52, -47.62) * mm, "end": v(43.52, 0) * mm});
            skSolve(sketch);
        }
        {
            var Q0;
            {var subQ0=sQuery(id+"F80.wireOp",EDGE,"E303.0.14");var subQ1=sQuery(id+"F80.wireOp",EDGE,"E303.0.1");var subQ2=makeQuery(id+"F80.imprint","INTERSECT",VERTEX,{"derivedFrom":[subQ1,subQ0]});Q0=makeQuery(id+"F80.imprint","IMPRINT",FACE,{"disambiguationData":[TD([[makeQuery(id+"F80.imprint","IMPRINT",EDGE,{"disambiguationData":[TD([[subQ2,-1.0]])],"derivedFrom":subQ1}),1.0]])]});}
            var Q1;
            {var subQ0=sQuery(id+"F80.wireOp",EDGE,"E303.0.14");var subQ1=sQuery(id+"F80.wireOp",EDGE,"E303.0.5");var subQ2=makeQuery(id+"F80.imprint","INTERSECT",VERTEX,{"derivedFrom":[subQ1,subQ0]});Q1=makeQuery(id+"F80.imprint","IMPRINT",FACE,{"disambiguationData":[TD([[makeQuery(id+"F80.imprint","IMPRINT",EDGE,{"disambiguationData":[TD([[subQ2,-1.0]])],"derivedFrom":subQ1}),1.0]])]});}
            var Q2;
            {var subQ0=sQuery(id+"F80.wireOp",EDGE,"E303.0.14");var subQ1=sQuery(id+"F80.wireOp",EDGE,"E303.0.9");var subQ2=makeQuery(id+"F80.imprint","INTERSECT",VERTEX,{"derivedFrom":[subQ1,subQ0]});Q2=makeQuery(id+"F80.imprint","IMPRINT",FACE,{"disambiguationData":[TD([[makeQuery(id+"F80.imprint","IMPRINT",EDGE,{"disambiguationData":[TD([[subQ2,-1.0]])],"derivedFrom":subQ1}),1.0]])]});}
            extrude(context, id + "F81", {"entities" : qUnion([Q0, Q1, Q2]), "operationType" : NewBodyOperationType.REMOVE, "oppositeDirection" : true, "depth" : 25.4 * mm, "offsetDistance" : 25.4 * mm});
        }
        {
            var Q0;
            Q0=makeQuery(id+"F3.opExtrude","SWEPT_FACE",FACE,{"disambiguationData":[OSD([sQuery(id+"F0.wireOp",EDGE,"E7")])]});
            var sketch = newSketch(context, id + "F82", { "sketchPlane" : qUnion([Q0])});
            skLineSegment(sketch, "E306.bottom", {"start": v(22.23, 0) * mm, "end": v(23.77, 0) * mm});
            skLineSegment(sketch, "E306.top", {"start": v(22.23, -7.14) * mm, "end": v(23.77, -7.14) * mm});
            skLineSegment(sketch, "E306.left", {"start": v(22.23, 0) * mm, "end": v(22.23, -7.14) * mm});
            skLineSegment(sketch, "E306.right", {"start": v(23.77, 0) * mm, "end": v(23.77, -7.14) * mm});
            skLineSegment(sketch, "E307.bottom", {"start": v(22.23, -13.49) * mm, "end": v(23.77, -13.49) * mm});
            skLineSegment(sketch, "E307.top", {"start": v(22.23, -20.62) * mm, "end": v(23.77, -20.62) * mm});
            skLineSegment(sketch, "E307.left", {"start": v(22.23, -13.49) * mm, "end": v(22.23, -20.62) * mm});
            skLineSegment(sketch, "E307.right", {"start": v(23.77, -13.49) * mm, "end": v(23.77, -20.62) * mm});
            skLineSegment(sketch, "E308.bottom", {"start": v(22.23, -26.97) * mm, "end": v(23.77, -26.97) * mm});
            skLineSegment(sketch, "E308.top", {"start": v(22.23, -34.11) * mm, "end": v(23.77, -34.11) * mm});
            skLineSegment(sketch, "E308.left", {"start": v(22.23, -26.97) * mm, "end": v(22.23, -34.11) * mm});
            skLineSegment(sketch, "E308.right", {"start": v(23.77, -26.97) * mm, "end": v(23.77, -34.11) * mm});
            skLineSegment(sketch, "E309.bottom", {"start": v(22.23, -40.46) * mm, "end": v(23.77, -40.46) * mm});
            skLineSegment(sketch, "E309.top", {"start": v(22.23, -47.63) * mm, "end": v(23.77, -47.63) * mm});
            skLineSegment(sketch, "E309.left", {"start": v(22.23, -40.46) * mm, "end": v(22.23, -47.63) * mm});
            skLineSegment(sketch, "E309.right", {"start": v(23.77, -40.46) * mm, "end": v(23.77, -47.63) * mm});
            skLineSegment(sketch, "E310", {"start": v(41.28, 3.18) * mm, "end": v(41.28, -47.63) * mm, "construction": true});
            skLineSegment(sketch, "E311.MirrorCS", {"start": v(60.32, 0) * mm, "end": v(58.78, 0) * mm});
            skLineSegment(sketch, "E312.MirrorCS", {"start": v(58.78, 0) * mm, "end": v(58.78, -7.14) * mm});
            skLineSegment(sketch, "E313.MirrorCS", {"start": v(60.32, -7.14) * mm, "end": v(58.78, -7.14) * mm});
            skLineSegment(sketch, "E314.MirrorCS", {"start": v(60.32, 0) * mm, "end": v(60.32, -7.14) * mm});
            skLineSegment(sketch, "E315.MirrorCS", {"start": v(60.32, -13.49) * mm, "end": v(58.78, -13.49) * mm});
            skLineSegment(sketch, "E316.MirrorCS", {"start": v(58.78, -13.49) * mm, "end": v(58.78, -20.62) * mm});
            skLineSegment(sketch, "E317.MirrorCS", {"start": v(60.32, -20.62) * mm, "end": v(58.78, -20.62) * mm});
            skLineSegment(sketch, "E318.MirrorCS", {"start": v(60.32, -13.49) * mm, "end": v(60.32, -20.62) * mm});
            skLineSegment(sketch, "E319.MirrorCS", {"start": v(60.32, -26.97) * mm, "end": v(58.78, -26.97) * mm});
            skLineSegment(sketch, "E320.MirrorCS", {"start": v(58.78, -26.97) * mm, "end": v(58.78, -34.11) * mm});
            skLineSegment(sketch, "E321.MirrorCS", {"start": v(60.32, -34.11) * mm, "end": v(58.78, -34.11) * mm});
            skLineSegment(sketch, "E322.MirrorCS", {"start": v(60.32, -26.97) * mm, "end": v(60.32, -34.11) * mm});
            skLineSegment(sketch, "E323.MirrorCS", {"start": v(60.32, -40.46) * mm, "end": v(58.78, -40.46) * mm});
            skLineSegment(sketch, "E324.MirrorCS", {"start": v(58.78, -40.46) * mm, "end": v(58.78, -47.63) * mm});
            skLineSegment(sketch, "E325.MirrorCS", {"start": v(60.32, -47.63) * mm, "end": v(58.78, -47.63) * mm});
            skLineSegment(sketch, "E326.MirrorCS", {"start": v(60.32, -40.46) * mm, "end": v(60.32, -47.63) * mm});
            skSolve(sketch);
        }
        {
            var Q0;
            Q0=makeQuery(id+"F82.imprint","IMPRINT",FACE,{"disambiguationData":[TD([[makeQuery(id+"F82.imprint","IMPRINT",EDGE,{"derivedFrom":sQuery(id+"F82.wireOp",EDGE,"E306.bottom")}),-1.0]])]});
            var Q1;
            Q1=makeQuery(id+"F82.imprint","IMPRINT",FACE,{"disambiguationData":[TD([[makeQuery(id+"F82.imprint","IMPRINT",EDGE,{"derivedFrom":sQuery(id+"F82.wireOp",EDGE,"E307.bottom")}),-1.0]])]});
            var Q2;
            Q2=makeQuery(id+"F82.imprint","IMPRINT",FACE,{"disambiguationData":[TD([[makeQuery(id+"F82.imprint","IMPRINT",EDGE,{"derivedFrom":sQuery(id+"F82.wireOp",EDGE,"E308.bottom")}),-1.0]])]});
            var Q3;
            Q3=makeQuery(id+"F82.imprint","IMPRINT",FACE,{"disambiguationData":[TD([[makeQuery(id+"F82.imprint","IMPRINT",EDGE,{"derivedFrom":sQuery(id+"F82.wireOp",EDGE,"E309.bottom")}),-1.0]])]});
            var Q4;
            Q4=makeQuery(id+"F82.imprint","IMPRINT",FACE,{"disambiguationData":[TD([[makeQuery(id+"F82.imprint","IMPRINT",EDGE,{"derivedFrom":sQuery(id+"F82.wireOp",EDGE,"E311.MirrorCS")}),-1.0]])]});
            var Q5;
            Q5=makeQuery(id+"F82.imprint","IMPRINT",FACE,{"disambiguationData":[TD([[makeQuery(id+"F82.imprint","IMPRINT",EDGE,{"derivedFrom":sQuery(id+"F82.wireOp",EDGE,"E315.MirrorCS")}),1.0]])]});
            var Q6;
            Q6=makeQuery(id+"F82.imprint","IMPRINT",FACE,{"disambiguationData":[TD([[makeQuery(id+"F82.imprint","IMPRINT",EDGE,{"derivedFrom":sQuery(id+"F82.wireOp",EDGE,"E319.MirrorCS")}),1.0]])]});
            var Q7;
            Q7=makeQuery(id+"F82.imprint","IMPRINT",FACE,{"disambiguationData":[TD([[makeQuery(id+"F82.imprint","IMPRINT",EDGE,{"derivedFrom":sQuery(id+"F82.wireOp",EDGE,"E323.MirrorCS")}),1.0]])]});
            extrude(context, id + "F83", {"entities" : qUnion([Q0, Q1, Q2, Q3, Q4, Q5, Q6, Q7]), "operationType" : NewBodyOperationType.REMOVE, "oppositeDirection" : true, "depth" : 3.17 * mm, "offsetDistance" : 25.4 * mm});
        }
        {
            var Q0;
            Q0=makeQuery(id+"F4.opExtrude","SWEPT_FACE",FACE,{"disambiguationData":[OSD([sQuery(id+"F0.wireOp",EDGE,"E8")])]});
            var sketch = newSketch(context, id + "F84", { "sketchPlane" : qUnion([Q0])});
            skLineSegment(sketch, "E327.bottom", {"start": v(-15.65, -7.14) * mm, "end": v(-14.1, -7.14) * mm});
            skLineSegment(sketch, "E327.top", {"start": v(-15.65, -13.49) * mm, "end": v(-14.1, -13.49) * mm});
            skLineSegment(sketch, "E327.left", {"start": v(-15.65, -7.14) * mm, "end": v(-15.65, -13.49) * mm});
            skLineSegment(sketch, "E327.right", {"start": v(-14.1, -7.14) * mm, "end": v(-14.1, -13.49) * mm});
            skLineSegment(sketch, "E328.bottom", {"start": v(-15.65, -20.62) * mm, "end": v(-14.1, -20.62) * mm});
            skLineSegment(sketch, "E328.top", {"start": v(-15.65, -26.97) * mm, "end": v(-14.1, -26.97) * mm});
            skLineSegment(sketch, "E328.left", {"start": v(-15.65, -20.62) * mm, "end": v(-15.65, -26.97) * mm});
            skLineSegment(sketch, "E328.right", {"start": v(-14.1, -20.62) * mm, "end": v(-14.1, -26.97) * mm});
            skLineSegment(sketch, "E329.bottom", {"start": v(-15.65, -34.11) * mm, "end": v(-14.1, -34.11) * mm});
            skLineSegment(sketch, "E329.top", {"start": v(-15.65, -40.46) * mm, "end": v(-14.1, -40.46) * mm});
            skLineSegment(sketch, "E329.left", {"start": v(-15.65, -34.11) * mm, "end": v(-15.65, -40.46) * mm});
            skLineSegment(sketch, "E329.right", {"start": v(-14.1, -34.11) * mm, "end": v(-14.1, -40.46) * mm});
            skLineSegment(sketch, "E330", {"start": v(0.23, -47.63) * mm, "end": v(0.23, 3.18) * mm});
            skLineSegment(sketch, "E331.MirrorCS", {"start": v(16.1, -7.14) * mm, "end": v(14.55, -7.14) * mm});
            skLineSegment(sketch, "E332.MirrorCS", {"start": v(14.55, -7.14) * mm, "end": v(14.55, -13.49) * mm});
            skLineSegment(sketch, "E333.MirrorCS", {"start": v(16.1, -13.49) * mm, "end": v(14.55, -13.49) * mm});
            skLineSegment(sketch, "E334.MirrorCS", {"start": v(16.1, -7.14) * mm, "end": v(16.1, -13.49) * mm});
            skLineSegment(sketch, "E335.MirrorCS", {"start": v(16.1, -20.62) * mm, "end": v(14.55, -20.62) * mm});
            skLineSegment(sketch, "E336.MirrorCS", {"start": v(14.55, -20.62) * mm, "end": v(14.55, -26.97) * mm});
            skLineSegment(sketch, "E337.MirrorCS", {"start": v(16.1, -26.97) * mm, "end": v(14.55, -26.97) * mm});
            skLineSegment(sketch, "E338.MirrorCS", {"start": v(16.1, -20.62) * mm, "end": v(16.1, -26.97) * mm});
            skLineSegment(sketch, "E339.MirrorCS", {"start": v(16.1, -34.11) * mm, "end": v(14.55, -34.11) * mm});
            skLineSegment(sketch, "E340.MirrorCS", {"start": v(14.55, -34.11) * mm, "end": v(14.55, -40.46) * mm});
            skLineSegment(sketch, "E341.MirrorCS", {"start": v(16.1, -40.46) * mm, "end": v(14.55, -40.46) * mm});
            skLineSegment(sketch, "E342.MirrorCS", {"start": v(16.1, -34.11) * mm, "end": v(16.1, -40.46) * mm});
            skSolve(sketch);
        }
        {
            var Q0;
            Q0=makeQuery(id+"F84.imprint","IMPRINT",FACE,{"disambiguationData":[TD([[makeQuery(id+"F84.imprint","IMPRINT",EDGE,{"derivedFrom":sQuery(id+"F84.wireOp",EDGE,"E327.bottom")}),-1.0]])]});
            var Q1;
            Q1=makeQuery(id+"F84.imprint","IMPRINT",FACE,{"disambiguationData":[TD([[makeQuery(id+"F84.imprint","IMPRINT",EDGE,{"derivedFrom":sQuery(id+"F84.wireOp",EDGE,"E328.bottom")}),-1.0]])]});
            var Q2;
            Q2=makeQuery(id+"F84.imprint","IMPRINT",FACE,{"disambiguationData":[TD([[makeQuery(id+"F84.imprint","IMPRINT",EDGE,{"derivedFrom":sQuery(id+"F84.wireOp",EDGE,"E329.bottom")}),-1.0]])]});
            var Q3;
            Q3=makeQuery(id+"F84.imprint","IMPRINT",FACE,{"disambiguationData":[TD([[makeQuery(id+"F84.imprint","IMPRINT",EDGE,{"derivedFrom":sQuery(id+"F84.wireOp",EDGE,"E331.MirrorCS")}),1.0]])]});
            var Q4;
            Q4=makeQuery(id+"F84.imprint","IMPRINT",FACE,{"disambiguationData":[TD([[makeQuery(id+"F84.imprint","IMPRINT",EDGE,{"derivedFrom":sQuery(id+"F84.wireOp",EDGE,"E335.MirrorCS")}),1.0]])]});
            var Q5;
            Q5=makeQuery(id+"F84.imprint","IMPRINT",FACE,{"disambiguationData":[TD([[makeQuery(id+"F84.imprint","IMPRINT",EDGE,{"derivedFrom":sQuery(id+"F84.wireOp",EDGE,"E339.MirrorCS")}),1.0]])]});
            extrude(context, id + "F85", {"entities" : qUnion([Q0, Q1, Q2, Q3, Q4, Q5]), "operationType" : NewBodyOperationType.REMOVE, "oppositeDirection" : true, "depth" : 25.4 * mm, "offsetDistance" : 25.4 * mm});
        }
        {
            var Q0;
            Q0=makeQuery(id+"F5.opExtrude","SWEPT_FACE",FACE,{"disambiguationData":[OSD([sQuery(id+"F0.wireOp",EDGE,"E9")])]});
            var sketch = newSketch(context, id + "F86", { "sketchPlane" : qUnion([Q0])});
            skLineSegment(sketch, "E343.bottom", {"start": v(-25.4, 0) * mm, "end": v(-23.85, 0) * mm});
            skLineSegment(sketch, "E343.top", {"start": v(-25.4, -7.14) * mm, "end": v(-23.85, -7.14) * mm});
            skLineSegment(sketch, "E343.left", {"start": v(-25.4, 0) * mm, "end": v(-25.4, -7.14) * mm});
            skLineSegment(sketch, "E343.right", {"start": v(-23.85, 0) * mm, "end": v(-23.85, -7.14) * mm});
            skLineSegment(sketch, "E344.bottom", {"start": v(-25.4, -13.49) * mm, "end": v(-23.85, -13.49) * mm});
            skLineSegment(sketch, "E344.top", {"start": v(-25.4, -20.62) * mm, "end": v(-23.85, -20.62) * mm});
            skLineSegment(sketch, "E344.left", {"start": v(-25.4, -13.49) * mm, "end": v(-25.4, -20.62) * mm});
            skLineSegment(sketch, "E344.right", {"start": v(-23.85, -13.49) * mm, "end": v(-23.85, -20.62) * mm});
            skLineSegment(sketch, "E345.bottom", {"start": v(-25.4, -26.97) * mm, "end": v(-23.85, -26.97) * mm});
            skLineSegment(sketch, "E345.top", {"start": v(-25.4, -34.11) * mm, "end": v(-23.85, -34.11) * mm});
            skLineSegment(sketch, "E345.left", {"start": v(-25.4, -26.97) * mm, "end": v(-25.4, -34.11) * mm});
            skLineSegment(sketch, "E345.right", {"start": v(-23.85, -26.97) * mm, "end": v(-23.85, -34.11) * mm});
            skLineSegment(sketch, "E346.bottom", {"start": v(-25.4, -40.46) * mm, "end": v(-23.85, -40.46) * mm});
            skLineSegment(sketch, "E346.top", {"start": v(-25.4, -47.6) * mm, "end": v(-23.85, -47.6) * mm});
            skLineSegment(sketch, "E346.left", {"start": v(-25.4, -40.46) * mm, "end": v(-25.4, -47.6) * mm});
            skLineSegment(sketch, "E346.right", {"start": v(-23.85, -40.46) * mm, "end": v(-23.85, -47.6) * mm});
            skLineSegment(sketch, "E347", {"start": v(-12.7, 3.18) * mm, "end": v(-12.7, -47.63) * mm});
            skLineSegment(sketch, "E348.MirrorCS", {"start": v(0, 0) * mm, "end": v(-1.55, 0) * mm});
            skLineSegment(sketch, "E349.MirrorCS", {"start": v(-1.55, 0) * mm, "end": v(-1.55, -7.14) * mm});
            skLineSegment(sketch, "E350.MirrorCS", {"start": v(0, -7.14) * mm, "end": v(-1.55, -7.14) * mm});
            skLineSegment(sketch, "E351.MirrorCS", {"start": v(0, 0) * mm, "end": v(0, -7.14) * mm});
            skLineSegment(sketch, "E352.MirrorCS", {"start": v(0, -13.49) * mm, "end": v(-1.55, -13.49) * mm});
            skLineSegment(sketch, "E353.MirrorCS", {"start": v(-1.55, -13.49) * mm, "end": v(-1.55, -20.62) * mm});
            skLineSegment(sketch, "E354.MirrorCS", {"start": v(0, -20.62) * mm, "end": v(-1.55, -20.62) * mm});
            skLineSegment(sketch, "E355.MirrorCS", {"start": v(0, -13.49) * mm, "end": v(0, -20.62) * mm});
            skLineSegment(sketch, "E356.MirrorCS", {"start": v(0, -26.97) * mm, "end": v(-1.55, -26.97) * mm});
            skLineSegment(sketch, "E357.MirrorCS", {"start": v(-1.55, -26.97) * mm, "end": v(-1.55, -34.11) * mm});
            skLineSegment(sketch, "E358.MirrorCS", {"start": v(0, -34.11) * mm, "end": v(-1.55, -34.11) * mm});
            skLineSegment(sketch, "E359.MirrorCS", {"start": v(0, -26.97) * mm, "end": v(0, -34.11) * mm});
            skLineSegment(sketch, "E360.MirrorCS", {"start": v(0, -40.46) * mm, "end": v(-1.55, -40.46) * mm});
            skLineSegment(sketch, "E361.MirrorCS", {"start": v(-1.55, -40.46) * mm, "end": v(-1.55, -47.6) * mm});
            skLineSegment(sketch, "E362.MirrorCS", {"start": v(0, -47.6) * mm, "end": v(-1.55, -47.6) * mm});
            skLineSegment(sketch, "E363.MirrorCS", {"start": v(0, -40.46) * mm, "end": v(0, -47.6) * mm});
            skSolve(sketch);
        }
        {
            var Q0;
            Q0=makeQuery(id+"F86.imprint","IMPRINT",FACE,{"disambiguationData":[TD([[makeQuery(id+"F86.imprint","IMPRINT",EDGE,{"derivedFrom":sQuery(id+"F86.wireOp",EDGE,"E343.bottom")}),-1.0]])]});
            var Q1;
            Q1=makeQuery(id+"F86.imprint","IMPRINT",FACE,{"disambiguationData":[TD([[makeQuery(id+"F86.imprint","IMPRINT",EDGE,{"derivedFrom":sQuery(id+"F86.wireOp",EDGE,"E344.bottom")}),-1.0]])]});
            var Q2;
            Q2=makeQuery(id+"F86.imprint","IMPRINT",FACE,{"disambiguationData":[TD([[makeQuery(id+"F86.imprint","IMPRINT",EDGE,{"derivedFrom":sQuery(id+"F86.wireOp",EDGE,"E345.bottom")}),-1.0]])]});
            var Q3;
            Q3=makeQuery(id+"F86.imprint","IMPRINT",FACE,{"disambiguationData":[TD([[makeQuery(id+"F86.imprint","IMPRINT",EDGE,{"derivedFrom":sQuery(id+"F86.wireOp",EDGE,"E346.bottom")}),-1.0]])]});
            var Q4;
            Q4=makeQuery(id+"F86.imprint","IMPRINT",FACE,{"disambiguationData":[TD([[makeQuery(id+"F86.imprint","IMPRINT",EDGE,{"derivedFrom":sQuery(id+"F86.wireOp",EDGE,"E348.MirrorCS")}),-1.0]])]});
            var Q5;
            Q5=makeQuery(id+"F86.imprint","IMPRINT",FACE,{"disambiguationData":[TD([[makeQuery(id+"F86.imprint","IMPRINT",EDGE,{"derivedFrom":sQuery(id+"F86.wireOp",EDGE,"E352.MirrorCS")}),1.0]])]});
            var Q6;
            Q6=makeQuery(id+"F86.imprint","IMPRINT",FACE,{"disambiguationData":[TD([[makeQuery(id+"F86.imprint","IMPRINT",EDGE,{"derivedFrom":sQuery(id+"F86.wireOp",EDGE,"E356.MirrorCS")}),1.0]])]});
            var Q7;
            Q7=makeQuery(id+"F86.imprint","IMPRINT",FACE,{"disambiguationData":[TD([[makeQuery(id+"F86.imprint","IMPRINT",EDGE,{"derivedFrom":sQuery(id+"F86.wireOp",EDGE,"E360.MirrorCS")}),1.0]])]});
            extrude(context, id + "F87", {"entities" : qUnion([Q0, Q1, Q2, Q3, Q4, Q5, Q6, Q7]), "operationType" : NewBodyOperationType.REMOVE, "oppositeDirection" : true, "depth" : 25.4 * mm, "offsetDistance" : 25.4 * mm});
        }
        {
            var Q0;
            Q0=makeQuery(id+"F6.opExtrude","SWEPT_FACE",FACE,{"disambiguationData":[OSD([sQuery(id+"F0.wireOp",EDGE,"E0")])]});
            var sketch = newSketch(context, id + "F88", { "sketchPlane" : qUnion([Q0])});
            skLineSegment(sketch, "E364.bottom", {"start": v(-53.4, -7.14) * mm, "end": v(-51.86, -7.14) * mm});
            skLineSegment(sketch, "E364.top", {"start": v(-53.4, -13.49) * mm, "end": v(-51.86, -13.49) * mm});
            skLineSegment(sketch, "E364.left", {"start": v(-53.4, -7.14) * mm, "end": v(-53.4, -13.49) * mm});
            skLineSegment(sketch, "E364.right", {"start": v(-51.86, -7.14) * mm, "end": v(-51.86, -13.49) * mm});
            skLineSegment(sketch, "E365.bottom", {"start": v(-53.4, -20.62) * mm, "end": v(-51.86, -20.62) * mm});
            skLineSegment(sketch, "E365.top", {"start": v(-53.4, -26.97) * mm, "end": v(-51.86, -26.97) * mm});
            skLineSegment(sketch, "E365.left", {"start": v(-53.4, -20.62) * mm, "end": v(-53.4, -26.97) * mm});
            skLineSegment(sketch, "E365.right", {"start": v(-51.86, -20.62) * mm, "end": v(-51.86, -26.97) * mm});
            skLineSegment(sketch, "E366.bottom", {"start": v(-53.4, -34.11) * mm, "end": v(-51.86, -34.11) * mm});
            skLineSegment(sketch, "E366.top", {"start": v(-53.4, -40.46) * mm, "end": v(-51.86, -40.46) * mm});
            skLineSegment(sketch, "E366.left", {"start": v(-53.4, -34.11) * mm, "end": v(-53.4, -40.46) * mm});
            skLineSegment(sketch, "E366.right", {"start": v(-51.86, -34.11) * mm, "end": v(-51.86, -40.46) * mm});
            skSolve(sketch);
        }
        {
            var Q0;
            Q0=makeQuery(id+"F88.imprint","IMPRINT",FACE,{"disambiguationData":[TD([[makeQuery(id+"F88.imprint","IMPRINT",EDGE,{"derivedFrom":sQuery(id+"F88.wireOp",EDGE,"E364.bottom")}),-1.0]])]});
            var Q1;
            Q1=makeQuery(id+"F88.imprint","IMPRINT",FACE,{"disambiguationData":[TD([[makeQuery(id+"F88.imprint","IMPRINT",EDGE,{"derivedFrom":sQuery(id+"F88.wireOp",EDGE,"E365.bottom")}),-1.0]])]});
            var Q2;
            Q2=makeQuery(id+"F88.imprint","IMPRINT",FACE,{"disambiguationData":[TD([[makeQuery(id+"F88.imprint","IMPRINT",EDGE,{"derivedFrom":sQuery(id+"F88.wireOp",EDGE,"E366.bottom")}),-1.0]])]});
            extrude(context, id + "F89", {"entities" : qUnion([Q0, Q1, Q2]), "operationType" : NewBodyOperationType.REMOVE, "oppositeDirection" : true, "depth" : 25.4 * mm, "offsetDistance" : 25.4 * mm});
        }
    });
